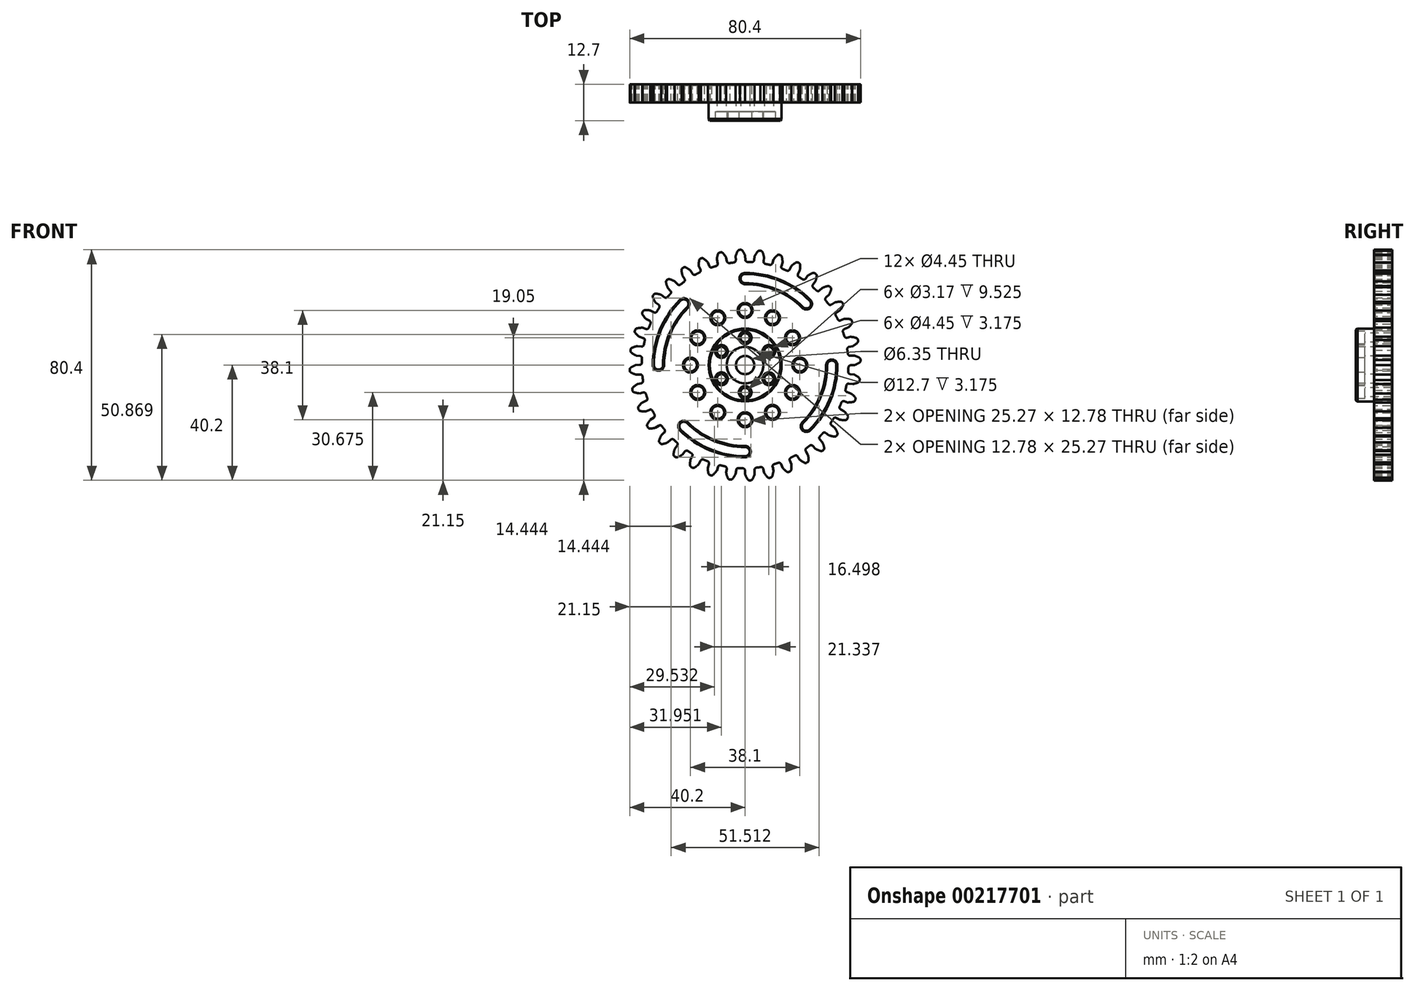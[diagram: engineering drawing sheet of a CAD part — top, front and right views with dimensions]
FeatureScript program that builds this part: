
annotation { "Feature Type Name" : "Feature", "Feature Type Description" : "" }
export const myFeature = defineFeature(function(context is Context, id is Id, definition is map)
    precondition{}
    {
        {
            var Q0;
            Q0=qCreatedBy(makeId("Front.planeOp"),FACE);
            var sketch = newSketch(context, id + "F0", { "sketchPlane" : qUnion([Q0])});
            skArc(sketch, "E0", {"start": v(-3.96, 35.76) * mm, "mid": v(-4.7, 35.68) * mm, "end": v(-5.43, 35.57) * mm});
            skArc(sketch, "E1.trimOffspring", {"start": v(0, 38.1) * mm, "mid": v(-0.4, 39) * mm, "end": v(-0.88, 39.84) * mm});
            skLineSegment(sketch, "E2", {"start": v(0, 38.1) * mm, "end": v(0.06, 36.73) * mm});
            skLineSegment(sketch, "E3", {"start": v(-1.55, 40.2) * mm, "end": v(-1.76, 40.2) * mm});
            skLineSegment(sketch, "E4.MirrorCS", {"start": v(-1.96, 40.18) * mm, "end": v(-1.76, 40.2) * mm});
            skArc(sketch, "E5.MirrorCS", {"start": v(-3.32, 37.96) * mm, "mid": v(-3, 38.88) * mm, "end": v(-2.6, 39.77) * mm});
            skLineSegment(sketch, "E6.MirrorCS", {"start": v(-3.32, 37.96) * mm, "end": v(-3.26, 36.58) * mm});
            skPoint(sketch, "E7.visualSharp", {"position": v(0.1, 35.98) * mm});
            skArc(sketch, "E7.filletArc", {"start": v(0.06, 36.73) * mm, "mid": v(0.3, 36.2) * mm, "end": v(0.83, 35.97) * mm});
            skPoint(sketch, "E8.visualSharp", {"position": v(-1.13, 40.2) * mm});
            skArc(sketch, "E8.filletArc", {"start": v(-0.88, 39.84) * mm, "mid": v(-1.17, 40.1) * mm, "end": v(-1.55, 40.2) * mm});
            skPoint(sketch, "E9.visualSharp", {"position": v(-2.38, 40.15) * mm});
            skArc(sketch, "E9.filletArc", {"start": v(-1.96, 40.18) * mm, "mid": v(-2.33, 40.05) * mm, "end": v(-2.6, 39.77) * mm});
            skPoint(sketch, "E10.visualSharp", {"position": v(-3.23, 35.84) * mm});
            skArc(sketch, "E10.filletArc", {"start": v(-3.96, 35.76) * mm, "mid": v(-3.45, 36.03) * mm, "end": v(-3.26, 36.58) * mm});
            skArc(sketch, "E11.1.0", {"start": v(-10.11, 34.53) * mm, "mid": v(-9.65, 34.89) * mm, "end": v(-9.56, 35.46) * mm});
            skLineSegment(sketch, "E11.1.1", {"start": v(-9.86, 36.8) * mm, "end": v(-9.56, 35.46) * mm});
            skArc(sketch, "E11.1.2", {"start": v(-9.86, 36.8) * mm, "mid": v(-9.7, 37.77) * mm, "end": v(-9.46, 38.71) * mm});
            skArc(sketch, "E11.1.3", {"start": v(-8.91, 39.23) * mm, "mid": v(-9.25, 39.04) * mm, "end": v(-9.46, 38.71) * mm});
            skLineSegment(sketch, "E11.1.4", {"start": v(-8.91, 39.23) * mm, "end": v(-8.7, 39.29) * mm});
            skLineSegment(sketch, "E11.1.5", {"start": v(-8.5, 39.32) * mm, "end": v(-8.7, 39.29) * mm});
            skArc(sketch, "E11.1.6", {"start": v(-7.79, 39.08) * mm, "mid": v(-8.11, 39.3) * mm, "end": v(-8.5, 39.32) * mm});
            skArc(sketch, "E11.1.7", {"start": v(-6.62, 37.52) * mm, "mid": v(-7.16, 38.33) * mm, "end": v(-7.79, 39.08) * mm});
            skLineSegment(sketch, "E11.1.8", {"start": v(-6.62, 37.52) * mm, "end": v(-6.32, 36.18) * mm});
            skArc(sketch, "E11.1.9", {"start": v(-6.32, 36.18) * mm, "mid": v(-6, 35.7) * mm, "end": v(-5.43, 35.57) * mm});
            skArc(sketch, "E11.2.0", {"start": v(-15.95, 32.25) * mm, "mid": v(-15.57, 32.68) * mm, "end": v(-15.58, 33.26) * mm});
            skLineSegment(sketch, "E11.2.1", {"start": v(-16.1, 34.53) * mm, "end": v(-15.58, 33.26) * mm});
            skArc(sketch, "E11.2.2", {"start": v(-16.1, 34.53) * mm, "mid": v(-16.12, 35.5) * mm, "end": v(-16.04, 36.48) * mm});
            skArc(sketch, "E11.2.3", {"start": v(-15.59, 37.09) * mm, "mid": v(-15.9, 36.84) * mm, "end": v(-16.04, 36.48) * mm});
            skLineSegment(sketch, "E11.2.4", {"start": v(-15.59, 37.09) * mm, "end": v(-15.4, 37.18) * mm});
            skLineSegment(sketch, "E11.2.5", {"start": v(-15.2, 37.25) * mm, "end": v(-15.4, 37.18) * mm});
            skArc(sketch, "E11.2.6", {"start": v(-14.46, 37.14) * mm, "mid": v(-14.81, 37.29) * mm, "end": v(-15.2, 37.25) * mm});
            skArc(sketch, "E11.2.7", {"start": v(-13.03, 35.8) * mm, "mid": v(-13.7, 36.5) * mm, "end": v(-14.46, 37.14) * mm});
            skLineSegment(sketch, "E11.2.8", {"start": v(-13.03, 35.8) * mm, "end": v(-12.5, 34.53) * mm});
            skArc(sketch, "E11.2.9", {"start": v(-12.5, 34.53) * mm, "mid": v(-12.1, 34.12) * mm, "end": v(-11.53, 34.09) * mm});
            skArc(sketch, "E12.2.3.0", {"start": v(-21.31, 29) * mm, "mid": v(-21, 29.48) * mm, "end": v(-21.11, 30.05) * mm});
            skLineSegment(sketch, "E12.4.3.0", {"start": v(-21.85, 31.2) * mm, "end": v(-21.11, 30.05) * mm});
            skArc(sketch, "E12.7.3.0", {"start": v(-21.85, 31.2) * mm, "mid": v(-22.04, 32.17) * mm, "end": v(-22.13, 33.14) * mm});
            skArc(sketch, "E12.11.3.0", {"start": v(-21.8, 33.82) * mm, "mid": v(-22.05, 33.52) * mm, "end": v(-22.13, 33.14) * mm});
            skLineSegment(sketch, "E12.15.3.0", {"start": v(-21.8, 33.82) * mm, "end": v(-21.62, 33.94) * mm});
            skLineSegment(sketch, "E12.18.3.0", {"start": v(-21.44, 34.04) * mm, "end": v(-21.62, 33.94) * mm});
            skArc(sketch, "E12.21.3.0", {"start": v(-20.68, 34.06) * mm, "mid": v(-21.06, 34.15) * mm, "end": v(-21.44, 34.04) * mm});
            skArc(sketch, "E12.25.3.0", {"start": v(-19.05, 33) * mm, "mid": v(-19.84, 33.57) * mm, "end": v(-20.68, 34.06) * mm});
            skLineSegment(sketch, "E12.29.3.0", {"start": v(-19.05, 33) * mm, "end": v(-18.31, 31.84) * mm});
            skArc(sketch, "E12.32.3.0", {"start": v(-18.31, 31.84) * mm, "mid": v(-17.84, 31.5) * mm, "end": v(-17.27, 31.57) * mm});
            skArc(sketch, "E12.2.4.0", {"start": v(-26.02, 24.85) * mm, "mid": v(-25.8, 25.39) * mm, "end": v(-26.01, 25.93) * mm});
            skLineSegment(sketch, "E12.4.4.0", {"start": v(-26.94, 26.94) * mm, "end": v(-26.01, 25.93) * mm});
            skArc(sketch, "E12.7.4.0", {"start": v(-26.94, 26.94) * mm, "mid": v(-27.3, 27.85) * mm, "end": v(-27.55, 28.8) * mm});
            skArc(sketch, "E12.11.4.0", {"start": v(-27.33, 29.52) * mm, "mid": v(-27.53, 29.18) * mm, "end": v(-27.55, 28.8) * mm});
            skLineSegment(sketch, "E12.15.4.0", {"start": v(-27.33, 29.52) * mm, "end": v(-27.19, 29.67) * mm});
            skLineSegment(sketch, "E12.18.4.0", {"start": v(-27.02, 29.8) * mm, "end": v(-27.19, 29.67) * mm});
            skArc(sketch, "E12.21.4.0", {"start": v(-26.29, 29.95) * mm, "mid": v(-26.67, 29.97) * mm, "end": v(-27.02, 29.8) * mm});
            skArc(sketch, "E12.25.4.0", {"start": v(-24.5, 29.19) * mm, "mid": v(-25.37, 29.61) * mm, "end": v(-26.29, 29.95) * mm});
            skLineSegment(sketch, "E12.29.4.0", {"start": v(-24.5, 29.19) * mm, "end": v(-23.56, 28.17) * mm});
            skArc(sketch, "E12.32.4.0", {"start": v(-23.56, 28.17) * mm, "mid": v(-23.04, 27.92) * mm, "end": v(-22.49, 28.1) * mm});
            skArc(sketch, "E12.2.5.0", {"start": v(-29.94, 19.96) * mm, "mid": v(-29.82, 20.52) * mm, "end": v(-30.12, 21.02) * mm});
            skLineSegment(sketch, "E12.4.5.0", {"start": v(-31.2, 21.85) * mm, "end": v(-30.12, 21.02) * mm});
            skArc(sketch, "E12.7.5.0", {"start": v(-31.2, 21.85) * mm, "mid": v(-31.71, 22.7) * mm, "end": v(-32.13, 23.57) * mm});
            skArc(sketch, "E12.11.5.0", {"start": v(-32.04, 24.32) * mm, "mid": v(-32.18, 23.96) * mm, "end": v(-32.13, 23.57) * mm});
            skLineSegment(sketch, "E12.15.5.0", {"start": v(-32.04, 24.32) * mm, "end": v(-31.92, 24.5) * mm});
            skLineSegment(sketch, "E12.18.5.0", {"start": v(-31.79, 24.66) * mm, "end": v(-31.92, 24.5) * mm});
            skArc(sketch, "E12.21.5.0", {"start": v(-31.09, 24.93) * mm, "mid": v(-31.47, 24.88) * mm, "end": v(-31.79, 24.66) * mm});
            skArc(sketch, "E12.25.5.0", {"start": v(-29.19, 24.5) * mm, "mid": v(-30.13, 24.76) * mm, "end": v(-31.09, 24.93) * mm});
            skLineSegment(sketch, "E12.29.5.0", {"start": v(-29.19, 24.5) * mm, "end": v(-28.1, 23.65) * mm});
            skArc(sketch, "E12.32.5.0", {"start": v(-28.1, 23.65) * mm, "mid": v(-27.54, 23.5) * mm, "end": v(-27.02, 23.76) * mm});
            skArc(sketch, "E12.2.6.0", {"start": v(-32.95, 14.45) * mm, "mid": v(-32.93, 15.03) * mm, "end": v(-33.31, 15.47) * mm});
            skLineSegment(sketch, "E12.4.6.0", {"start": v(-34.53, 16.1) * mm, "end": v(-33.31, 15.47) * mm});
            skArc(sketch, "E12.7.6.0", {"start": v(-34.53, 16.1) * mm, "mid": v(-35.17, 16.84) * mm, "end": v(-35.73, 17.64) * mm});
            skArc(sketch, "E12.11.6.0", {"start": v(-35.78, 18.4) * mm, "mid": v(-35.85, 18) * mm, "end": v(-35.73, 17.64) * mm});
            skLineSegment(sketch, "E12.15.6.0", {"start": v(-35.78, 18.4) * mm, "end": v(-35.7, 18.58) * mm});
            skLineSegment(sketch, "E12.18.6.0", {"start": v(-35.59, 18.76) * mm, "end": v(-35.7, 18.58) * mm});
            skArc(sketch, "E12.21.6.0", {"start": v(-34.94, 19.16) * mm, "mid": v(-35.32, 19.04) * mm, "end": v(-35.59, 18.76) * mm});
            skArc(sketch, "E12.25.6.0", {"start": v(-33, 19.05) * mm, "mid": v(-33.97, 19.15) * mm, "end": v(-34.94, 19.16) * mm});
            skLineSegment(sketch, "E12.29.6.0", {"start": v(-33, 19.05) * mm, "end": v(-31.78, 18.42) * mm});
            skArc(sketch, "E12.32.6.0", {"start": v(-31.78, 18.42) * mm, "mid": v(-31.2, 18.36) * mm, "end": v(-30.74, 18.7) * mm});
            skArc(sketch, "E12.2.7.0", {"start": v(-34.96, 8.51) * mm, "mid": v(-35.04, 9.08) * mm, "end": v(-35.5, 9.45) * mm});
            skLineSegment(sketch, "E12.4.7.0", {"start": v(-36.8, 9.86) * mm, "end": v(-35.5, 9.45) * mm});
            skArc(sketch, "E12.7.7.0", {"start": v(-36.8, 9.86) * mm, "mid": v(-37.56, 10.48) * mm, "end": v(-38.25, 11.16) * mm});
            skArc(sketch, "E12.11.7.0", {"start": v(-38.43, 11.9) * mm, "mid": v(-38.44, 11.5) * mm, "end": v(-38.25, 11.16) * mm});
            skLineSegment(sketch, "E12.15.7.0", {"start": v(-38.43, 11.9) * mm, "end": v(-38.38, 12.1) * mm});
            skLineSegment(sketch, "E12.18.7.0", {"start": v(-38.3, 12.3) * mm, "end": v(-38.38, 12.1) * mm});
            skArc(sketch, "E12.21.7.0", {"start": v(-37.74, 12.8) * mm, "mid": v(-38.09, 12.62) * mm, "end": v(-38.3, 12.3) * mm});
            skArc(sketch, "E12.25.7.0", {"start": v(-35.8, 13.03) * mm, "mid": v(-36.78, 12.96) * mm, "end": v(-37.74, 12.8) * mm});
            skLineSegment(sketch, "E12.29.7.0", {"start": v(-35.8, 13.03) * mm, "end": v(-34.5, 12.62) * mm});
            skArc(sketch, "E12.32.7.0", {"start": v(-34.5, 12.62) * mm, "mid": v(-33.91, 12.66) * mm, "end": v(-33.52, 13.08) * mm});
            skArc(sketch, "E12.2.8.0", {"start": v(-35.9, 2.3) * mm, "mid": v(-36.09, 2.86) * mm, "end": v(-36.6, 3.14) * mm});
            skLineSegment(sketch, "E12.4.8.0", {"start": v(-37.96, 3.32) * mm, "end": v(-36.6, 3.14) * mm});
            skArc(sketch, "E12.7.8.0", {"start": v(-37.96, 3.32) * mm, "mid": v(-38.8, 3.8) * mm, "end": v(-39.61, 4.35) * mm});
            skArc(sketch, "E12.11.8.0", {"start": v(-39.91, 5.04) * mm, "mid": v(-39.85, 4.66) * mm, "end": v(-39.61, 4.35) * mm});
            skLineSegment(sketch, "E12.15.8.0", {"start": v(-39.91, 5.04) * mm, "end": v(-39.9, 5.25) * mm});
            skLineSegment(sketch, "E12.18.8.0", {"start": v(-39.86, 5.46) * mm, "end": v(-39.9, 5.25) * mm});
            skArc(sketch, "E12.21.8.0", {"start": v(-39.39, 6.05) * mm, "mid": v(-39.7, 5.81) * mm, "end": v(-39.86, 5.46) * mm});
            skArc(sketch, "E12.25.8.0", {"start": v(-37.52, 6.62) * mm, "mid": v(-38.47, 6.38) * mm, "end": v(-39.39, 6.05) * mm});
            skLineSegment(sketch, "E12.29.8.0", {"start": v(-37.52, 6.62) * mm, "end": v(-36.16, 6.44) * mm});
            skArc(sketch, "E12.32.8.0", {"start": v(-36.16, 6.44) * mm, "mid": v(-35.6, 6.58) * mm, "end": v(-35.28, 7.06) * mm});
            skArc(sketch, "E12.2.9.0", {"start": v(-35.76, -3.96) * mm, "mid": v(-36.03, -3.45) * mm, "end": v(-36.58, -3.26) * mm});
            skLineSegment(sketch, "E12.4.9.0", {"start": v(-37.96, -3.32) * mm, "end": v(-36.58, -3.26) * mm});
            skArc(sketch, "E12.7.9.0", {"start": v(-37.96, -3.32) * mm, "mid": v(-38.88, -3) * mm, "end": v(-39.77, -2.6) * mm});
            skArc(sketch, "E12.11.9.0", {"start": v(-40.18, -1.96) * mm, "mid": v(-40.05, -2.33) * mm, "end": v(-39.77, -2.6) * mm});
            skLineSegment(sketch, "E12.15.9.0", {"start": v(-40.18, -1.96) * mm, "end": v(-40.2, -1.76) * mm});
            skLineSegment(sketch, "E12.18.9.0", {"start": v(-40.2, -1.55) * mm, "end": v(-40.2, -1.76) * mm});
            skArc(sketch, "E12.21.9.0", {"start": v(-39.84, -0.88) * mm, "mid": v(-40.1, -1.17) * mm, "end": v(-40.2, -1.55) * mm});
            skArc(sketch, "E12.25.9.0", {"start": v(-38.1, 0) * mm, "mid": v(-39, -0.4) * mm, "end": v(-39.84, -0.88) * mm});
            skLineSegment(sketch, "E12.29.9.0", {"start": v(-38.1, 0) * mm, "end": v(-36.73, 0.06) * mm});
            skArc(sketch, "E12.32.9.0", {"start": v(-36.73, 0.06) * mm, "mid": v(-36.2, 0.3) * mm, "end": v(-35.97, 0.83) * mm});
            skArc(sketch, "E12.2.10.0", {"start": v(-34.53, -10.11) * mm, "mid": v(-34.89, -9.65) * mm, "end": v(-35.46, -9.56) * mm});
            skLineSegment(sketch, "E12.4.10.0", {"start": v(-36.8, -9.86) * mm, "end": v(-35.46, -9.56) * mm});
            skArc(sketch, "E12.7.10.0", {"start": v(-36.8, -9.86) * mm, "mid": v(-37.77, -9.7) * mm, "end": v(-38.71, -9.46) * mm});
            skArc(sketch, "E12.11.10.0", {"start": v(-39.23, -8.91) * mm, "mid": v(-39.04, -9.25) * mm, "end": v(-38.71, -9.46) * mm});
            skLineSegment(sketch, "E12.15.10.0", {"start": v(-39.23, -8.91) * mm, "end": v(-39.29, -8.7) * mm});
            skLineSegment(sketch, "E12.18.10.0", {"start": v(-39.32, -8.5) * mm, "end": v(-39.29, -8.7) * mm});
            skArc(sketch, "E12.21.10.0", {"start": v(-39.08, -7.79) * mm, "mid": v(-39.3, -8.11) * mm, "end": v(-39.32, -8.5) * mm});
            skArc(sketch, "E12.25.10.0", {"start": v(-37.52, -6.62) * mm, "mid": v(-38.33, -7.16) * mm, "end": v(-39.08, -7.79) * mm});
            skLineSegment(sketch, "E12.29.10.0", {"start": v(-37.52, -6.62) * mm, "end": v(-36.18, -6.32) * mm});
            skArc(sketch, "E12.32.10.0", {"start": v(-36.18, -6.32) * mm, "mid": v(-35.7, -6) * mm, "end": v(-35.57, -5.43) * mm});
            skArc(sketch, "E12.2.11.0", {"start": v(-32.25, -15.95) * mm, "mid": v(-32.68, -15.57) * mm, "end": v(-33.26, -15.58) * mm});
            skLineSegment(sketch, "E12.4.11.0", {"start": v(-34.53, -16.1) * mm, "end": v(-33.26, -15.58) * mm});
            skArc(sketch, "E12.7.11.0", {"start": v(-34.53, -16.1) * mm, "mid": v(-35.5, -16.12) * mm, "end": v(-36.48, -16.04) * mm});
            skArc(sketch, "E12.11.11.0", {"start": v(-37.09, -15.59) * mm, "mid": v(-36.84, -15.9) * mm, "end": v(-36.48, -16.04) * mm});
            skLineSegment(sketch, "E12.15.11.0", {"start": v(-37.09, -15.59) * mm, "end": v(-37.18, -15.4) * mm});
            skLineSegment(sketch, "E12.18.11.0", {"start": v(-37.25, -15.2) * mm, "end": v(-37.18, -15.4) * mm});
            skArc(sketch, "E12.21.11.0", {"start": v(-37.14, -14.46) * mm, "mid": v(-37.29, -14.81) * mm, "end": v(-37.25, -15.2) * mm});
            skArc(sketch, "E12.25.11.0", {"start": v(-35.8, -13.03) * mm, "mid": v(-36.5, -13.7) * mm, "end": v(-37.14, -14.46) * mm});
            skLineSegment(sketch, "E12.29.11.0", {"start": v(-35.8, -13.03) * mm, "end": v(-34.53, -12.5) * mm});
            skArc(sketch, "E12.32.11.0", {"start": v(-34.53, -12.5) * mm, "mid": v(-34.12, -12.1) * mm, "end": v(-34.09, -11.53) * mm});
            skArc(sketch, "E12.2.12.0", {"start": v(-29, -21.31) * mm, "mid": v(-29.48, -21) * mm, "end": v(-30.05, -21.11) * mm});
            skLineSegment(sketch, "E12.4.12.0", {"start": v(-31.2, -21.85) * mm, "end": v(-30.05, -21.11) * mm});
            skArc(sketch, "E12.7.12.0", {"start": v(-31.2, -21.85) * mm, "mid": v(-32.17, -22.04) * mm, "end": v(-33.14, -22.13) * mm});
            skArc(sketch, "E12.11.12.0", {"start": v(-33.82, -21.8) * mm, "mid": v(-33.52, -22.05) * mm, "end": v(-33.14, -22.13) * mm});
            skLineSegment(sketch, "E12.15.12.0", {"start": v(-33.82, -21.8) * mm, "end": v(-33.94, -21.62) * mm});
            skLineSegment(sketch, "E12.18.12.0", {"start": v(-34.04, -21.44) * mm, "end": v(-33.94, -21.62) * mm});
            skArc(sketch, "E12.21.12.0", {"start": v(-34.06, -20.68) * mm, "mid": v(-34.15, -21.06) * mm, "end": v(-34.04, -21.44) * mm});
            skArc(sketch, "E12.25.12.0", {"start": v(-33, -19.05) * mm, "mid": v(-33.57, -19.84) * mm, "end": v(-34.06, -20.68) * mm});
            skLineSegment(sketch, "E12.29.12.0", {"start": v(-33, -19.05) * mm, "end": v(-31.84, -18.31) * mm});
            skArc(sketch, "E12.32.12.0", {"start": v(-31.84, -18.31) * mm, "mid": v(-31.5, -17.84) * mm, "end": v(-31.57, -17.27) * mm});
            skArc(sketch, "E12.2.13.0", {"start": v(-24.85, -26.02) * mm, "mid": v(-25.39, -25.8) * mm, "end": v(-25.93, -26.01) * mm});
            skLineSegment(sketch, "E12.4.13.0", {"start": v(-26.94, -26.94) * mm, "end": v(-25.93, -26.01) * mm});
            skArc(sketch, "E12.7.13.0", {"start": v(-26.94, -26.94) * mm, "mid": v(-27.85, -27.3) * mm, "end": v(-28.8, -27.55) * mm});
            skArc(sketch, "E12.11.13.0", {"start": v(-29.52, -27.33) * mm, "mid": v(-29.18, -27.53) * mm, "end": v(-28.8, -27.55) * mm});
            skLineSegment(sketch, "E12.15.13.0", {"start": v(-29.52, -27.33) * mm, "end": v(-29.67, -27.19) * mm});
            skLineSegment(sketch, "E12.18.13.0", {"start": v(-29.8, -27.02) * mm, "end": v(-29.67, -27.19) * mm});
            skArc(sketch, "E12.21.13.0", {"start": v(-29.95, -26.29) * mm, "mid": v(-29.97, -26.67) * mm, "end": v(-29.8, -27.02) * mm});
            skArc(sketch, "E12.25.13.0", {"start": v(-29.19, -24.5) * mm, "mid": v(-29.61, -25.37) * mm, "end": v(-29.95, -26.29) * mm});
            skLineSegment(sketch, "E12.29.13.0", {"start": v(-29.19, -24.5) * mm, "end": v(-28.17, -23.56) * mm});
            skArc(sketch, "E12.32.13.0", {"start": v(-28.17, -23.56) * mm, "mid": v(-27.92, -23.04) * mm, "end": v(-28.1, -22.49) * mm});
            skArc(sketch, "E12.2.14.0", {"start": v(-19.96, -29.94) * mm, "mid": v(-20.52, -29.82) * mm, "end": v(-21.02, -30.12) * mm});
            skLineSegment(sketch, "E12.4.14.0", {"start": v(-21.85, -31.2) * mm, "end": v(-21.02, -30.12) * mm});
            skArc(sketch, "E12.7.14.0", {"start": v(-21.85, -31.2) * mm, "mid": v(-22.7, -31.71) * mm, "end": v(-23.57, -32.13) * mm});
            skArc(sketch, "E12.11.14.0", {"start": v(-24.32, -32.04) * mm, "mid": v(-23.96, -32.18) * mm, "end": v(-23.57, -32.13) * mm});
            skLineSegment(sketch, "E12.15.14.0", {"start": v(-24.32, -32.04) * mm, "end": v(-24.5, -31.92) * mm});
            skLineSegment(sketch, "E12.18.14.0", {"start": v(-24.66, -31.79) * mm, "end": v(-24.5, -31.92) * mm});
            skArc(sketch, "E12.21.14.0", {"start": v(-24.93, -31.09) * mm, "mid": v(-24.88, -31.47) * mm, "end": v(-24.66, -31.79) * mm});
            skArc(sketch, "E12.25.14.0", {"start": v(-24.5, -29.19) * mm, "mid": v(-24.76, -30.13) * mm, "end": v(-24.93, -31.09) * mm});
            skLineSegment(sketch, "E12.29.14.0", {"start": v(-24.5, -29.19) * mm, "end": v(-23.65, -28.1) * mm});
            skArc(sketch, "E12.32.14.0", {"start": v(-23.65, -28.1) * mm, "mid": v(-23.5, -27.54) * mm, "end": v(-23.76, -27.02) * mm});
            skArc(sketch, "E12.2.15.0", {"start": v(-14.45, -32.95) * mm, "mid": v(-15.03, -32.93) * mm, "end": v(-15.47, -33.31) * mm});
            skLineSegment(sketch, "E12.4.15.0", {"start": v(-16.1, -34.53) * mm, "end": v(-15.47, -33.31) * mm});
            skArc(sketch, "E12.7.15.0", {"start": v(-16.1, -34.53) * mm, "mid": v(-16.84, -35.17) * mm, "end": v(-17.64, -35.73) * mm});
            skArc(sketch, "E12.11.15.0", {"start": v(-18.4, -35.78) * mm, "mid": v(-18, -35.85) * mm, "end": v(-17.64, -35.73) * mm});
            skLineSegment(sketch, "E12.15.15.0", {"start": v(-18.4, -35.78) * mm, "end": v(-18.58, -35.7) * mm});
            skLineSegment(sketch, "E12.18.15.0", {"start": v(-18.76, -35.59) * mm, "end": v(-18.58, -35.7) * mm});
            skArc(sketch, "E12.21.15.0", {"start": v(-19.16, -34.94) * mm, "mid": v(-19.04, -35.32) * mm, "end": v(-18.76, -35.59) * mm});
            skArc(sketch, "E12.25.15.0", {"start": v(-19.05, -33) * mm, "mid": v(-19.15, -33.97) * mm, "end": v(-19.16, -34.94) * mm});
            skLineSegment(sketch, "E12.29.15.0", {"start": v(-19.05, -33) * mm, "end": v(-18.42, -31.78) * mm});
            skArc(sketch, "E12.32.15.0", {"start": v(-18.42, -31.78) * mm, "mid": v(-18.36, -31.2) * mm, "end": v(-18.7, -30.74) * mm});
            skArc(sketch, "E12.2.16.0", {"start": v(-8.51, -34.96) * mm, "mid": v(-9.08, -35.04) * mm, "end": v(-9.45, -35.5) * mm});
            skLineSegment(sketch, "E12.4.16.0", {"start": v(-9.86, -36.8) * mm, "end": v(-9.45, -35.5) * mm});
            skArc(sketch, "E12.7.16.0", {"start": v(-9.86, -36.8) * mm, "mid": v(-10.48, -37.56) * mm, "end": v(-11.16, -38.25) * mm});
            skArc(sketch, "E12.11.16.0", {"start": v(-11.9, -38.43) * mm, "mid": v(-11.5, -38.44) * mm, "end": v(-11.16, -38.25) * mm});
            skLineSegment(sketch, "E12.15.16.0", {"start": v(-11.9, -38.43) * mm, "end": v(-12.1, -38.38) * mm});
            skLineSegment(sketch, "E12.18.16.0", {"start": v(-12.3, -38.3) * mm, "end": v(-12.1, -38.38) * mm});
            skArc(sketch, "E12.21.16.0", {"start": v(-12.8, -37.74) * mm, "mid": v(-12.62, -38.09) * mm, "end": v(-12.3, -38.3) * mm});
            skArc(sketch, "E12.25.16.0", {"start": v(-13.03, -35.8) * mm, "mid": v(-12.96, -36.78) * mm, "end": v(-12.8, -37.74) * mm});
            skLineSegment(sketch, "E12.29.16.0", {"start": v(-13.03, -35.8) * mm, "end": v(-12.62, -34.5) * mm});
            skArc(sketch, "E12.32.16.0", {"start": v(-12.62, -34.5) * mm, "mid": v(-12.66, -33.91) * mm, "end": v(-13.08, -33.52) * mm});
            skArc(sketch, "E12.2.17.0", {"start": v(-2.3, -35.9) * mm, "mid": v(-2.86, -36.09) * mm, "end": v(-3.14, -36.6) * mm});
            skLineSegment(sketch, "E12.4.17.0", {"start": v(-3.32, -37.96) * mm, "end": v(-3.14, -36.6) * mm});
            skArc(sketch, "E12.7.17.0", {"start": v(-3.32, -37.96) * mm, "mid": v(-3.8, -38.8) * mm, "end": v(-4.35, -39.61) * mm});
            skArc(sketch, "E12.11.17.0", {"start": v(-5.04, -39.91) * mm, "mid": v(-4.66, -39.85) * mm, "end": v(-4.35, -39.61) * mm});
            skLineSegment(sketch, "E12.15.17.0", {"start": v(-5.04, -39.91) * mm, "end": v(-5.25, -39.9) * mm});
            skLineSegment(sketch, "E12.18.17.0", {"start": v(-5.46, -39.86) * mm, "end": v(-5.25, -39.9) * mm});
            skArc(sketch, "E12.21.17.0", {"start": v(-6.05, -39.39) * mm, "mid": v(-5.81, -39.7) * mm, "end": v(-5.46, -39.86) * mm});
            skArc(sketch, "E12.25.17.0", {"start": v(-6.62, -37.52) * mm, "mid": v(-6.38, -38.47) * mm, "end": v(-6.05, -39.39) * mm});
            skLineSegment(sketch, "E12.29.17.0", {"start": v(-6.62, -37.52) * mm, "end": v(-6.44, -36.16) * mm});
            skArc(sketch, "E12.32.17.0", {"start": v(-6.44, -36.16) * mm, "mid": v(-6.58, -35.6) * mm, "end": v(-7.06, -35.28) * mm});
            skArc(sketch, "E12.2.18.0", {"start": v(3.96, -35.76) * mm, "mid": v(3.45, -36.03) * mm, "end": v(3.26, -36.58) * mm});
            skLineSegment(sketch, "E12.4.18.0", {"start": v(3.32, -37.96) * mm, "end": v(3.26, -36.58) * mm});
            skArc(sketch, "E12.7.18.0", {"start": v(3.32, -37.96) * mm, "mid": v(3, -38.88) * mm, "end": v(2.6, -39.77) * mm});
            skArc(sketch, "E12.11.18.0", {"start": v(1.96, -40.18) * mm, "mid": v(2.33, -40.05) * mm, "end": v(2.6, -39.77) * mm});
            skLineSegment(sketch, "E12.15.18.0", {"start": v(1.96, -40.18) * mm, "end": v(1.76, -40.2) * mm});
            skLineSegment(sketch, "E12.18.18.0", {"start": v(1.55, -40.2) * mm, "end": v(1.76, -40.2) * mm});
            skArc(sketch, "E12.21.18.0", {"start": v(0.88, -39.84) * mm, "mid": v(1.17, -40.1) * mm, "end": v(1.55, -40.2) * mm});
            skArc(sketch, "E12.25.18.0", {"start": v(0, -38.1) * mm, "mid": v(0.4, -39) * mm, "end": v(0.88, -39.84) * mm});
            skLineSegment(sketch, "E12.29.18.0", {"start": v(0, -38.1) * mm, "end": v(-0.06, -36.73) * mm});
            skArc(sketch, "E12.32.18.0", {"start": v(-0.06, -36.73) * mm, "mid": v(-0.3, -36.2) * mm, "end": v(-0.83, -35.97) * mm});
            skArc(sketch, "E12.2.19.0", {"start": v(10.11, -34.53) * mm, "mid": v(9.65, -34.89) * mm, "end": v(9.56, -35.46) * mm});
            skLineSegment(sketch, "E12.4.19.0", {"start": v(9.86, -36.8) * mm, "end": v(9.56, -35.46) * mm});
            skArc(sketch, "E12.7.19.0", {"start": v(9.86, -36.8) * mm, "mid": v(9.7, -37.77) * mm, "end": v(9.46, -38.71) * mm});
            skArc(sketch, "E12.11.19.0", {"start": v(8.91, -39.23) * mm, "mid": v(9.25, -39.04) * mm, "end": v(9.46, -38.71) * mm});
            skLineSegment(sketch, "E12.15.19.0", {"start": v(8.91, -39.23) * mm, "end": v(8.7, -39.29) * mm});
            skLineSegment(sketch, "E12.18.19.0", {"start": v(8.5, -39.32) * mm, "end": v(8.7, -39.29) * mm});
            skArc(sketch, "E12.21.19.0", {"start": v(7.79, -39.08) * mm, "mid": v(8.11, -39.3) * mm, "end": v(8.5, -39.32) * mm});
            skArc(sketch, "E12.25.19.0", {"start": v(6.62, -37.52) * mm, "mid": v(7.16, -38.33) * mm, "end": v(7.79, -39.08) * mm});
            skLineSegment(sketch, "E12.29.19.0", {"start": v(6.62, -37.52) * mm, "end": v(6.32, -36.18) * mm});
            skArc(sketch, "E12.32.19.0", {"start": v(6.32, -36.18) * mm, "mid": v(6, -35.7) * mm, "end": v(5.43, -35.57) * mm});
            skArc(sketch, "E12.2.20.0", {"start": v(15.95, -32.25) * mm, "mid": v(15.57, -32.68) * mm, "end": v(15.58, -33.26) * mm});
            skLineSegment(sketch, "E12.4.20.0", {"start": v(16.1, -34.53) * mm, "end": v(15.58, -33.26) * mm});
            skArc(sketch, "E12.7.20.0", {"start": v(16.1, -34.53) * mm, "mid": v(16.12, -35.5) * mm, "end": v(16.04, -36.48) * mm});
            skArc(sketch, "E12.11.20.0", {"start": v(15.59, -37.09) * mm, "mid": v(15.9, -36.84) * mm, "end": v(16.04, -36.48) * mm});
            skLineSegment(sketch, "E12.15.20.0", {"start": v(15.59, -37.09) * mm, "end": v(15.4, -37.18) * mm});
            skLineSegment(sketch, "E12.18.20.0", {"start": v(15.2, -37.25) * mm, "end": v(15.4, -37.18) * mm});
            skArc(sketch, "E12.21.20.0", {"start": v(14.46, -37.14) * mm, "mid": v(14.81, -37.29) * mm, "end": v(15.2, -37.25) * mm});
            skArc(sketch, "E12.25.20.0", {"start": v(13.03, -35.8) * mm, "mid": v(13.7, -36.5) * mm, "end": v(14.46, -37.14) * mm});
            skLineSegment(sketch, "E12.29.20.0", {"start": v(13.03, -35.8) * mm, "end": v(12.5, -34.53) * mm});
            skArc(sketch, "E12.32.20.0", {"start": v(12.5, -34.53) * mm, "mid": v(12.1, -34.12) * mm, "end": v(11.53, -34.09) * mm});
            skArc(sketch, "E12.2.21.0", {"start": v(21.31, -29) * mm, "mid": v(21, -29.48) * mm, "end": v(21.11, -30.05) * mm});
            skLineSegment(sketch, "E12.4.21.0", {"start": v(21.85, -31.2) * mm, "end": v(21.11, -30.05) * mm});
            skArc(sketch, "E12.7.21.0", {"start": v(21.85, -31.2) * mm, "mid": v(22.04, -32.17) * mm, "end": v(22.13, -33.14) * mm});
            skArc(sketch, "E12.11.21.0", {"start": v(21.8, -33.82) * mm, "mid": v(22.05, -33.52) * mm, "end": v(22.13, -33.14) * mm});
            skLineSegment(sketch, "E12.15.21.0", {"start": v(21.8, -33.82) * mm, "end": v(21.62, -33.94) * mm});
            skLineSegment(sketch, "E12.18.21.0", {"start": v(21.44, -34.04) * mm, "end": v(21.62, -33.94) * mm});
            skArc(sketch, "E12.21.21.0", {"start": v(20.68, -34.06) * mm, "mid": v(21.06, -34.15) * mm, "end": v(21.44, -34.04) * mm});
            skArc(sketch, "E12.25.21.0", {"start": v(19.05, -33) * mm, "mid": v(19.84, -33.57) * mm, "end": v(20.68, -34.06) * mm});
            skLineSegment(sketch, "E12.29.21.0", {"start": v(19.05, -33) * mm, "end": v(18.31, -31.84) * mm});
            skArc(sketch, "E12.32.21.0", {"start": v(18.31, -31.84) * mm, "mid": v(17.84, -31.5) * mm, "end": v(17.27, -31.57) * mm});
            skArc(sketch, "E12.2.22.0", {"start": v(26.02, -24.85) * mm, "mid": v(25.8, -25.39) * mm, "end": v(26.01, -25.93) * mm});
            skLineSegment(sketch, "E12.4.22.0", {"start": v(26.94, -26.94) * mm, "end": v(26.01, -25.93) * mm});
            skArc(sketch, "E12.7.22.0", {"start": v(26.94, -26.94) * mm, "mid": v(27.3, -27.85) * mm, "end": v(27.55, -28.8) * mm});
            skArc(sketch, "E12.11.22.0", {"start": v(27.33, -29.52) * mm, "mid": v(27.53, -29.18) * mm, "end": v(27.55, -28.8) * mm});
            skLineSegment(sketch, "E12.15.22.0", {"start": v(27.33, -29.52) * mm, "end": v(27.19, -29.67) * mm});
            skLineSegment(sketch, "E12.18.22.0", {"start": v(27.02, -29.8) * mm, "end": v(27.19, -29.67) * mm});
            skArc(sketch, "E12.21.22.0", {"start": v(26.29, -29.95) * mm, "mid": v(26.67, -29.97) * mm, "end": v(27.02, -29.8) * mm});
            skArc(sketch, "E12.25.22.0", {"start": v(24.5, -29.19) * mm, "mid": v(25.37, -29.61) * mm, "end": v(26.29, -29.95) * mm});
            skLineSegment(sketch, "E12.29.22.0", {"start": v(24.5, -29.19) * mm, "end": v(23.56, -28.17) * mm});
            skArc(sketch, "E12.32.22.0", {"start": v(23.56, -28.17) * mm, "mid": v(23.04, -27.92) * mm, "end": v(22.49, -28.1) * mm});
            skArc(sketch, "E12.2.23.0", {"start": v(29.94, -19.96) * mm, "mid": v(29.82, -20.52) * mm, "end": v(30.12, -21.02) * mm});
            skLineSegment(sketch, "E12.4.23.0", {"start": v(31.2, -21.85) * mm, "end": v(30.12, -21.02) * mm});
            skArc(sketch, "E12.7.23.0", {"start": v(31.2, -21.85) * mm, "mid": v(31.71, -22.7) * mm, "end": v(32.13, -23.57) * mm});
            skArc(sketch, "E12.11.23.0", {"start": v(32.04, -24.32) * mm, "mid": v(32.18, -23.96) * mm, "end": v(32.13, -23.57) * mm});
            skLineSegment(sketch, "E12.15.23.0", {"start": v(32.04, -24.32) * mm, "end": v(31.92, -24.5) * mm});
            skLineSegment(sketch, "E12.18.23.0", {"start": v(31.79, -24.66) * mm, "end": v(31.92, -24.5) * mm});
            skArc(sketch, "E12.21.23.0", {"start": v(31.09, -24.93) * mm, "mid": v(31.47, -24.88) * mm, "end": v(31.79, -24.66) * mm});
            skArc(sketch, "E12.25.23.0", {"start": v(29.19, -24.5) * mm, "mid": v(30.13, -24.76) * mm, "end": v(31.09, -24.93) * mm});
            skLineSegment(sketch, "E12.29.23.0", {"start": v(29.19, -24.5) * mm, "end": v(28.1, -23.65) * mm});
            skArc(sketch, "E12.32.23.0", {"start": v(28.1, -23.65) * mm, "mid": v(27.54, -23.5) * mm, "end": v(27.02, -23.76) * mm});
            skArc(sketch, "E12.2.24.0", {"start": v(32.95, -14.45) * mm, "mid": v(32.93, -15.03) * mm, "end": v(33.31, -15.47) * mm});
            skLineSegment(sketch, "E12.4.24.0", {"start": v(34.53, -16.1) * mm, "end": v(33.31, -15.47) * mm});
            skArc(sketch, "E12.7.24.0", {"start": v(34.53, -16.1) * mm, "mid": v(35.17, -16.84) * mm, "end": v(35.73, -17.64) * mm});
            skArc(sketch, "E12.11.24.0", {"start": v(35.78, -18.4) * mm, "mid": v(35.85, -18) * mm, "end": v(35.73, -17.64) * mm});
            skLineSegment(sketch, "E12.15.24.0", {"start": v(35.78, -18.4) * mm, "end": v(35.7, -18.58) * mm});
            skLineSegment(sketch, "E12.18.24.0", {"start": v(35.59, -18.76) * mm, "end": v(35.7, -18.58) * mm});
            skArc(sketch, "E12.21.24.0", {"start": v(34.94, -19.16) * mm, "mid": v(35.32, -19.04) * mm, "end": v(35.59, -18.76) * mm});
            skArc(sketch, "E12.25.24.0", {"start": v(33, -19.05) * mm, "mid": v(33.97, -19.15) * mm, "end": v(34.94, -19.16) * mm});
            skLineSegment(sketch, "E12.29.24.0", {"start": v(33, -19.05) * mm, "end": v(31.78, -18.42) * mm});
            skArc(sketch, "E12.32.24.0", {"start": v(31.78, -18.42) * mm, "mid": v(31.2, -18.36) * mm, "end": v(30.74, -18.7) * mm});
            skArc(sketch, "E12.2.25.0", {"start": v(34.96, -8.51) * mm, "mid": v(35.04, -9.08) * mm, "end": v(35.5, -9.45) * mm});
            skLineSegment(sketch, "E12.4.25.0", {"start": v(36.8, -9.86) * mm, "end": v(35.5, -9.45) * mm});
            skArc(sketch, "E12.7.25.0", {"start": v(36.8, -9.86) * mm, "mid": v(37.56, -10.48) * mm, "end": v(38.25, -11.16) * mm});
            skArc(sketch, "E12.11.25.0", {"start": v(38.43, -11.9) * mm, "mid": v(38.44, -11.5) * mm, "end": v(38.25, -11.16) * mm});
            skLineSegment(sketch, "E12.15.25.0", {"start": v(38.43, -11.9) * mm, "end": v(38.38, -12.1) * mm});
            skLineSegment(sketch, "E12.18.25.0", {"start": v(38.3, -12.3) * mm, "end": v(38.38, -12.1) * mm});
            skArc(sketch, "E12.21.25.0", {"start": v(37.74, -12.8) * mm, "mid": v(38.09, -12.62) * mm, "end": v(38.3, -12.3) * mm});
            skArc(sketch, "E12.25.25.0", {"start": v(35.8, -13.03) * mm, "mid": v(36.78, -12.96) * mm, "end": v(37.74, -12.8) * mm});
            skLineSegment(sketch, "E12.29.25.0", {"start": v(35.8, -13.03) * mm, "end": v(34.5, -12.62) * mm});
            skArc(sketch, "E12.32.25.0", {"start": v(34.5, -12.62) * mm, "mid": v(33.91, -12.66) * mm, "end": v(33.52, -13.08) * mm});
            skArc(sketch, "E12.2.26.0", {"start": v(35.9, -2.3) * mm, "mid": v(36.09, -2.86) * mm, "end": v(36.6, -3.14) * mm});
            skLineSegment(sketch, "E12.4.26.0", {"start": v(37.96, -3.32) * mm, "end": v(36.6, -3.14) * mm});
            skArc(sketch, "E12.7.26.0", {"start": v(37.96, -3.32) * mm, "mid": v(38.8, -3.8) * mm, "end": v(39.61, -4.35) * mm});
            skArc(sketch, "E12.11.26.0", {"start": v(39.91, -5.04) * mm, "mid": v(39.85, -4.66) * mm, "end": v(39.61, -4.35) * mm});
            skLineSegment(sketch, "E12.15.26.0", {"start": v(39.91, -5.04) * mm, "end": v(39.9, -5.25) * mm});
            skLineSegment(sketch, "E12.18.26.0", {"start": v(39.86, -5.46) * mm, "end": v(39.9, -5.25) * mm});
            skArc(sketch, "E12.21.26.0", {"start": v(39.39, -6.05) * mm, "mid": v(39.7, -5.81) * mm, "end": v(39.86, -5.46) * mm});
            skArc(sketch, "E12.25.26.0", {"start": v(37.52, -6.62) * mm, "mid": v(38.47, -6.38) * mm, "end": v(39.39, -6.05) * mm});
            skLineSegment(sketch, "E12.29.26.0", {"start": v(37.52, -6.62) * mm, "end": v(36.16, -6.44) * mm});
            skArc(sketch, "E12.32.26.0", {"start": v(36.16, -6.44) * mm, "mid": v(35.6, -6.58) * mm, "end": v(35.28, -7.06) * mm});
            skArc(sketch, "E12.2.27.0", {"start": v(35.76, 3.96) * mm, "mid": v(36.03, 3.45) * mm, "end": v(36.58, 3.26) * mm});
            skLineSegment(sketch, "E12.4.27.0", {"start": v(37.96, 3.32) * mm, "end": v(36.58, 3.26) * mm});
            skArc(sketch, "E12.7.27.0", {"start": v(37.96, 3.32) * mm, "mid": v(38.88, 3) * mm, "end": v(39.77, 2.6) * mm});
            skArc(sketch, "E12.11.27.0", {"start": v(40.18, 1.96) * mm, "mid": v(40.05, 2.33) * mm, "end": v(39.77, 2.6) * mm});
            skLineSegment(sketch, "E12.15.27.0", {"start": v(40.18, 1.96) * mm, "end": v(40.2, 1.76) * mm});
            skLineSegment(sketch, "E12.18.27.0", {"start": v(40.2, 1.55) * mm, "end": v(40.2, 1.76) * mm});
            skArc(sketch, "E12.21.27.0", {"start": v(39.84, 0.88) * mm, "mid": v(40.1, 1.17) * mm, "end": v(40.2, 1.55) * mm});
            skArc(sketch, "E12.25.27.0", {"start": v(38.1, 0) * mm, "mid": v(39, 0.4) * mm, "end": v(39.84, 0.88) * mm});
            skLineSegment(sketch, "E12.29.27.0", {"start": v(38.1, 0) * mm, "end": v(36.73, -0.06) * mm});
            skArc(sketch, "E12.32.27.0", {"start": v(36.73, -0.06) * mm, "mid": v(36.2, -0.3) * mm, "end": v(35.97, -0.83) * mm});
            skArc(sketch, "E12.2.28.0", {"start": v(34.53, 10.11) * mm, "mid": v(34.89, 9.65) * mm, "end": v(35.46, 9.56) * mm});
            skLineSegment(sketch, "E12.4.28.0", {"start": v(36.8, 9.86) * mm, "end": v(35.46, 9.56) * mm});
            skArc(sketch, "E12.7.28.0", {"start": v(36.8, 9.86) * mm, "mid": v(37.77, 9.7) * mm, "end": v(38.71, 9.46) * mm});
            skArc(sketch, "E12.11.28.0", {"start": v(39.23, 8.91) * mm, "mid": v(39.04, 9.25) * mm, "end": v(38.71, 9.46) * mm});
            skLineSegment(sketch, "E12.15.28.0", {"start": v(39.23, 8.91) * mm, "end": v(39.29, 8.7) * mm});
            skLineSegment(sketch, "E12.18.28.0", {"start": v(39.32, 8.5) * mm, "end": v(39.29, 8.7) * mm});
            skArc(sketch, "E12.21.28.0", {"start": v(39.08, 7.79) * mm, "mid": v(39.3, 8.11) * mm, "end": v(39.32, 8.5) * mm});
            skArc(sketch, "E12.25.28.0", {"start": v(37.52, 6.62) * mm, "mid": v(38.33, 7.16) * mm, "end": v(39.08, 7.79) * mm});
            skLineSegment(sketch, "E12.29.28.0", {"start": v(37.52, 6.62) * mm, "end": v(36.18, 6.32) * mm});
            skArc(sketch, "E12.32.28.0", {"start": v(36.18, 6.32) * mm, "mid": v(35.7, 6) * mm, "end": v(35.57, 5.43) * mm});
            skArc(sketch, "E12.2.29.0", {"start": v(32.25, 15.95) * mm, "mid": v(32.68, 15.57) * mm, "end": v(33.26, 15.58) * mm});
            skLineSegment(sketch, "E12.4.29.0", {"start": v(34.53, 16.1) * mm, "end": v(33.26, 15.58) * mm});
            skArc(sketch, "E12.7.29.0", {"start": v(34.53, 16.1) * mm, "mid": v(35.5, 16.12) * mm, "end": v(36.48, 16.04) * mm});
            skArc(sketch, "E12.11.29.0", {"start": v(37.09, 15.59) * mm, "mid": v(36.84, 15.9) * mm, "end": v(36.48, 16.04) * mm});
            skLineSegment(sketch, "E12.15.29.0", {"start": v(37.09, 15.59) * mm, "end": v(37.18, 15.4) * mm});
            skLineSegment(sketch, "E12.18.29.0", {"start": v(37.25, 15.2) * mm, "end": v(37.18, 15.4) * mm});
            skArc(sketch, "E12.21.29.0", {"start": v(37.14, 14.46) * mm, "mid": v(37.29, 14.81) * mm, "end": v(37.25, 15.2) * mm});
            skArc(sketch, "E12.25.29.0", {"start": v(35.8, 13.03) * mm, "mid": v(36.5, 13.7) * mm, "end": v(37.14, 14.46) * mm});
            skLineSegment(sketch, "E12.29.29.0", {"start": v(35.8, 13.03) * mm, "end": v(34.53, 12.5) * mm});
            skArc(sketch, "E12.32.29.0", {"start": v(34.53, 12.5) * mm, "mid": v(34.12, 12.1) * mm, "end": v(34.09, 11.53) * mm});
            skArc(sketch, "E12.2.30.0", {"start": v(29, 21.31) * mm, "mid": v(29.48, 21) * mm, "end": v(30.05, 21.11) * mm});
            skLineSegment(sketch, "E12.4.30.0", {"start": v(31.2, 21.85) * mm, "end": v(30.05, 21.11) * mm});
            skArc(sketch, "E12.7.30.0", {"start": v(31.2, 21.85) * mm, "mid": v(32.17, 22.04) * mm, "end": v(33.14, 22.13) * mm});
            skArc(sketch, "E12.11.30.0", {"start": v(33.82, 21.8) * mm, "mid": v(33.52, 22.05) * mm, "end": v(33.14, 22.13) * mm});
            skLineSegment(sketch, "E12.15.30.0", {"start": v(33.82, 21.8) * mm, "end": v(33.94, 21.62) * mm});
            skLineSegment(sketch, "E12.18.30.0", {"start": v(34.04, 21.44) * mm, "end": v(33.94, 21.62) * mm});
            skArc(sketch, "E12.21.30.0", {"start": v(34.06, 20.68) * mm, "mid": v(34.15, 21.06) * mm, "end": v(34.04, 21.44) * mm});
            skArc(sketch, "E12.25.30.0", {"start": v(33, 19.05) * mm, "mid": v(33.57, 19.84) * mm, "end": v(34.06, 20.68) * mm});
            skLineSegment(sketch, "E12.29.30.0", {"start": v(33, 19.05) * mm, "end": v(31.84, 18.31) * mm});
            skArc(sketch, "E12.32.30.0", {"start": v(31.84, 18.31) * mm, "mid": v(31.5, 17.84) * mm, "end": v(31.57, 17.27) * mm});
            skArc(sketch, "E12.2.31.0", {"start": v(24.85, 26.02) * mm, "mid": v(25.39, 25.8) * mm, "end": v(25.93, 26.01) * mm});
            skLineSegment(sketch, "E12.4.31.0", {"start": v(26.94, 26.94) * mm, "end": v(25.93, 26.01) * mm});
            skArc(sketch, "E12.7.31.0", {"start": v(26.94, 26.94) * mm, "mid": v(27.85, 27.3) * mm, "end": v(28.8, 27.55) * mm});
            skArc(sketch, "E12.11.31.0", {"start": v(29.52, 27.33) * mm, "mid": v(29.18, 27.53) * mm, "end": v(28.8, 27.55) * mm});
            skLineSegment(sketch, "E12.15.31.0", {"start": v(29.52, 27.33) * mm, "end": v(29.67, 27.19) * mm});
            skLineSegment(sketch, "E12.18.31.0", {"start": v(29.8, 27.02) * mm, "end": v(29.67, 27.19) * mm});
            skArc(sketch, "E12.21.31.0", {"start": v(29.95, 26.29) * mm, "mid": v(29.97, 26.67) * mm, "end": v(29.8, 27.02) * mm});
            skArc(sketch, "E12.25.31.0", {"start": v(29.19, 24.5) * mm, "mid": v(29.61, 25.37) * mm, "end": v(29.95, 26.29) * mm});
            skLineSegment(sketch, "E12.29.31.0", {"start": v(29.19, 24.5) * mm, "end": v(28.17, 23.56) * mm});
            skArc(sketch, "E12.32.31.0", {"start": v(28.17, 23.56) * mm, "mid": v(27.92, 23.04) * mm, "end": v(28.1, 22.49) * mm});
            skArc(sketch, "E12.2.32.0", {"start": v(19.96, 29.94) * mm, "mid": v(20.52, 29.82) * mm, "end": v(21.02, 30.12) * mm});
            skLineSegment(sketch, "E12.4.32.0", {"start": v(21.85, 31.2) * mm, "end": v(21.02, 30.12) * mm});
            skArc(sketch, "E12.7.32.0", {"start": v(21.85, 31.2) * mm, "mid": v(22.7, 31.71) * mm, "end": v(23.57, 32.13) * mm});
            skArc(sketch, "E12.11.32.0", {"start": v(24.32, 32.04) * mm, "mid": v(23.96, 32.18) * mm, "end": v(23.57, 32.13) * mm});
            skLineSegment(sketch, "E12.15.32.0", {"start": v(24.32, 32.04) * mm, "end": v(24.5, 31.92) * mm});
            skLineSegment(sketch, "E12.18.32.0", {"start": v(24.66, 31.79) * mm, "end": v(24.5, 31.92) * mm});
            skArc(sketch, "E12.21.32.0", {"start": v(24.93, 31.09) * mm, "mid": v(24.88, 31.47) * mm, "end": v(24.66, 31.79) * mm});
            skArc(sketch, "E12.25.32.0", {"start": v(24.5, 29.19) * mm, "mid": v(24.76, 30.13) * mm, "end": v(24.93, 31.09) * mm});
            skLineSegment(sketch, "E12.29.32.0", {"start": v(24.5, 29.19) * mm, "end": v(23.65, 28.1) * mm});
            skArc(sketch, "E12.32.32.0", {"start": v(23.65, 28.1) * mm, "mid": v(23.5, 27.54) * mm, "end": v(23.76, 27.02) * mm});
            skArc(sketch, "E12.2.33.0", {"start": v(14.45, 32.95) * mm, "mid": v(15.03, 32.93) * mm, "end": v(15.47, 33.31) * mm});
            skLineSegment(sketch, "E12.4.33.0", {"start": v(16.1, 34.53) * mm, "end": v(15.47, 33.31) * mm});
            skArc(sketch, "E12.7.33.0", {"start": v(16.1, 34.53) * mm, "mid": v(16.84, 35.17) * mm, "end": v(17.64, 35.73) * mm});
            skArc(sketch, "E12.11.33.0", {"start": v(18.4, 35.78) * mm, "mid": v(18, 35.85) * mm, "end": v(17.64, 35.73) * mm});
            skLineSegment(sketch, "E12.15.33.0", {"start": v(18.4, 35.78) * mm, "end": v(18.58, 35.7) * mm});
            skLineSegment(sketch, "E12.18.33.0", {"start": v(18.76, 35.59) * mm, "end": v(18.58, 35.7) * mm});
            skArc(sketch, "E12.21.33.0", {"start": v(19.16, 34.94) * mm, "mid": v(19.04, 35.32) * mm, "end": v(18.76, 35.59) * mm});
            skArc(sketch, "E12.25.33.0", {"start": v(19.05, 33) * mm, "mid": v(19.15, 33.97) * mm, "end": v(19.16, 34.94) * mm});
            skLineSegment(sketch, "E12.29.33.0", {"start": v(19.05, 33) * mm, "end": v(18.42, 31.78) * mm});
            skArc(sketch, "E12.32.33.0", {"start": v(18.42, 31.78) * mm, "mid": v(18.36, 31.2) * mm, "end": v(18.7, 30.74) * mm});
            skArc(sketch, "E12.2.34.0", {"start": v(8.51, 34.96) * mm, "mid": v(9.08, 35.04) * mm, "end": v(9.45, 35.5) * mm});
            skLineSegment(sketch, "E12.4.34.0", {"start": v(9.86, 36.8) * mm, "end": v(9.45, 35.5) * mm});
            skArc(sketch, "E12.7.34.0", {"start": v(9.86, 36.8) * mm, "mid": v(10.48, 37.56) * mm, "end": v(11.16, 38.25) * mm});
            skArc(sketch, "E12.11.34.0", {"start": v(11.9, 38.43) * mm, "mid": v(11.5, 38.44) * mm, "end": v(11.16, 38.25) * mm});
            skLineSegment(sketch, "E12.15.34.0", {"start": v(11.9, 38.43) * mm, "end": v(12.1, 38.38) * mm});
            skLineSegment(sketch, "E12.18.34.0", {"start": v(12.3, 38.3) * mm, "end": v(12.1, 38.38) * mm});
            skArc(sketch, "E12.21.34.0", {"start": v(12.8, 37.74) * mm, "mid": v(12.62, 38.09) * mm, "end": v(12.3, 38.3) * mm});
            skArc(sketch, "E12.25.34.0", {"start": v(13.03, 35.8) * mm, "mid": v(12.96, 36.78) * mm, "end": v(12.8, 37.74) * mm});
            skLineSegment(sketch, "E12.29.34.0", {"start": v(13.03, 35.8) * mm, "end": v(12.62, 34.5) * mm});
            skArc(sketch, "E12.32.34.0", {"start": v(12.62, 34.5) * mm, "mid": v(12.66, 33.91) * mm, "end": v(13.08, 33.52) * mm});
            skArc(sketch, "E12.2.35.0", {"start": v(2.3, 35.9) * mm, "mid": v(2.86, 36.09) * mm, "end": v(3.14, 36.6) * mm});
            skLineSegment(sketch, "E12.4.35.0", {"start": v(3.32, 37.96) * mm, "end": v(3.14, 36.6) * mm});
            skArc(sketch, "E12.7.35.0", {"start": v(3.32, 37.96) * mm, "mid": v(3.8, 38.8) * mm, "end": v(4.35, 39.61) * mm});
            skArc(sketch, "E12.11.35.0", {"start": v(5.04, 39.91) * mm, "mid": v(4.66, 39.85) * mm, "end": v(4.35, 39.61) * mm});
            skLineSegment(sketch, "E12.15.35.0", {"start": v(5.04, 39.91) * mm, "end": v(5.25, 39.9) * mm});
            skLineSegment(sketch, "E12.18.35.0", {"start": v(5.46, 39.86) * mm, "end": v(5.25, 39.9) * mm});
            skArc(sketch, "E12.21.35.0", {"start": v(6.05, 39.39) * mm, "mid": v(5.81, 39.7) * mm, "end": v(5.46, 39.86) * mm});
            skArc(sketch, "E12.25.35.0", {"start": v(6.62, 37.52) * mm, "mid": v(6.38, 38.47) * mm, "end": v(6.05, 39.39) * mm});
            skLineSegment(sketch, "E12.29.35.0", {"start": v(6.62, 37.52) * mm, "end": v(6.44, 36.16) * mm});
            skArc(sketch, "E12.32.35.0", {"start": v(6.44, 36.16) * mm, "mid": v(6.58, 35.6) * mm, "end": v(7.06, 35.28) * mm});
            skArc(sketch, "E13.trimOffspring", {"start": v(-10.11, 34.53) * mm, "mid": v(-10.82, 34.32) * mm, "end": v(-11.53, 34.09) * mm});
            skArc(sketch, "E14.trimOffspring", {"start": v(-15.95, 32.25) * mm, "mid": v(-16.62, 31.92) * mm, "end": v(-17.27, 31.57) * mm});
            skArc(sketch, "E15.trimOffspring", {"start": v(2.3, 35.9) * mm, "mid": v(1.57, 35.95) * mm, "end": v(0.83, 35.97) * mm});
            skArc(sketch, "E16.trimOffspring", {"start": v(8.51, 34.96) * mm, "mid": v(7.79, 35.13) * mm, "end": v(7.06, 35.28) * mm});
            skArc(sketch, "E17.trimOffspring", {"start": v(14.45, 32.95) * mm, "mid": v(13.77, 33.24) * mm, "end": v(13.08, 33.52) * mm});
            skArc(sketch, "E18.trimOffspring", {"start": v(19.96, 29.94) * mm, "mid": v(19.33, 30.35) * mm, "end": v(18.7, 30.74) * mm});
            skArc(sketch, "E19.trimOffspring", {"start": v(24.85, 26.02) * mm, "mid": v(24.3, 26.53) * mm, "end": v(23.76, 27.02) * mm});
            skArc(sketch, "E20.trimOffspring", {"start": v(29, 21.31) * mm, "mid": v(28.55, 21.9) * mm, "end": v(28.1, 22.49) * mm});
            skArc(sketch, "E21.trimOffspring", {"start": v(32.25, 15.95) * mm, "mid": v(31.92, 16.62) * mm, "end": v(31.57, 17.27) * mm});
            skArc(sketch, "E22.trimOffspring", {"start": v(34.53, 10.11) * mm, "mid": v(34.32, 10.82) * mm, "end": v(34.09, 11.53) * mm});
            skArc(sketch, "E23.trimOffspring", {"start": v(35.76, 3.96) * mm, "mid": v(35.68, 4.7) * mm, "end": v(35.57, 5.43) * mm});
            skArc(sketch, "E24.trimOffspring", {"start": v(-21.31, 29) * mm, "mid": v(-21.9, 28.55) * mm, "end": v(-22.49, 28.1) * mm});
            skArc(sketch, "E25.trimOffspring", {"start": v(-26.02, 24.85) * mm, "mid": v(-26.53, 24.3) * mm, "end": v(-27.02, 23.76) * mm});
            skArc(sketch, "E26.trimOffspring", {"start": v(-29.94, 19.96) * mm, "mid": v(-30.35, 19.33) * mm, "end": v(-30.74, 18.7) * mm});
            skArc(sketch, "E27.trimOffspring", {"start": v(-32.95, 14.45) * mm, "mid": v(-33.24, 13.77) * mm, "end": v(-33.52, 13.08) * mm});
            skArc(sketch, "E28.trimOffspring", {"start": v(-34.96, 8.51) * mm, "mid": v(-35.13, 7.79) * mm, "end": v(-35.28, 7.06) * mm});
            skArc(sketch, "E29.trimOffspring", {"start": v(-35.9, 2.3) * mm, "mid": v(-35.95, 1.57) * mm, "end": v(-35.97, 0.83) * mm});
            skArc(sketch, "E30.trimOffspring", {"start": v(-35.76, -3.96) * mm, "mid": v(-35.68, -4.7) * mm, "end": v(-35.57, -5.43) * mm});
            skArc(sketch, "E31.trimOffspring", {"start": v(-34.53, -10.11) * mm, "mid": v(-34.32, -10.82) * mm, "end": v(-34.09, -11.53) * mm});
            skArc(sketch, "E32.trimOffspring", {"start": v(-32.25, -15.95) * mm, "mid": v(-31.92, -16.62) * mm, "end": v(-31.57, -17.27) * mm});
            skArc(sketch, "E33.trimOffspring", {"start": v(-29, -21.31) * mm, "mid": v(-28.55, -21.9) * mm, "end": v(-28.1, -22.49) * mm});
            skArc(sketch, "E34.trimOffspring", {"start": v(-24.85, -26.02) * mm, "mid": v(-24.3, -26.53) * mm, "end": v(-23.76, -27.02) * mm});
            skArc(sketch, "E35.trimOffspring", {"start": v(-19.96, -29.94) * mm, "mid": v(-19.33, -30.35) * mm, "end": v(-18.7, -30.74) * mm});
            skArc(sketch, "E36.trimOffspring", {"start": v(-14.45, -32.95) * mm, "mid": v(-13.77, -33.24) * mm, "end": v(-13.08, -33.52) * mm});
            skArc(sketch, "E37.trimOffspring", {"start": v(-8.51, -34.96) * mm, "mid": v(-7.79, -35.13) * mm, "end": v(-7.06, -35.28) * mm});
            skArc(sketch, "E38.trimOffspring", {"start": v(-2.3, -35.9) * mm, "mid": v(-1.57, -35.95) * mm, "end": v(-0.83, -35.97) * mm});
            skArc(sketch, "E39.trimOffspring", {"start": v(3.96, -35.76) * mm, "mid": v(4.7, -35.68) * mm, "end": v(5.43, -35.57) * mm});
            skArc(sketch, "E40.trimOffspring", {"start": v(10.11, -34.53) * mm, "mid": v(10.82, -34.32) * mm, "end": v(11.53, -34.09) * mm});
            skArc(sketch, "E41.trimOffspring", {"start": v(15.95, -32.25) * mm, "mid": v(16.62, -31.92) * mm, "end": v(17.27, -31.57) * mm});
            skArc(sketch, "E42.trimOffspring", {"start": v(21.31, -29) * mm, "mid": v(21.9, -28.55) * mm, "end": v(22.49, -28.1) * mm});
            skArc(sketch, "E43.trimOffspring", {"start": v(26.02, -24.85) * mm, "mid": v(26.53, -24.3) * mm, "end": v(27.02, -23.76) * mm});
            skArc(sketch, "E44.trimOffspring", {"start": v(29.94, -19.96) * mm, "mid": v(30.35, -19.33) * mm, "end": v(30.74, -18.7) * mm});
            skArc(sketch, "E45.trimOffspring", {"start": v(32.95, -14.45) * mm, "mid": v(33.24, -13.77) * mm, "end": v(33.52, -13.08) * mm});
            skArc(sketch, "E46.trimOffspring", {"start": v(34.96, -8.51) * mm, "mid": v(35.13, -7.79) * mm, "end": v(35.28, -7.06) * mm});
            skArc(sketch, "E47.trimOffspring", {"start": v(35.9, -2.3) * mm, "mid": v(35.95, -1.57) * mm, "end": v(35.97, -0.83) * mm});
            skSolve(sketch);
        }
        {
            var Q0;
            Q0=makeQuery(id+"F0.imprint","IMPRINT",FACE,{"disambiguationData":[TD([[makeQuery(id+"F0.imprint","IMPRINT",EDGE,{"derivedFrom":sQuery(id+"F0.wireOp",EDGE,"E0")}),1.0]])]});
            extrude(context, id + "F1", {"entities" : qUnion([Q0]), "depth" : 6.35 * mm});
        }
        {
            var Q0;
            Q0=makeQuery(id+"F1.opExtrude","CAP_FACE",FACE,{"disambiguationData":[OSD([sQuery(id+"F0.wireOp",EDGE,"E0"),sQuery(id+"F0.wireOp",EDGE,"E1.trimOffspring"),sQuery(id+"F0.wireOp",EDGE,"E2"),sQuery(id+"F0.wireOp",EDGE,"E3"),sQuery(id+"F0.wireOp",EDGE,"E4.MirrorCS"),sQuery(id+"F0.wireOp",EDGE,"E5.MirrorCS"),sQuery(id+"F0.wireOp",EDGE,"E6.MirrorCS"),sQuery(id+"F0.wireOp",EDGE,"E7.filletArc"),sQuery(id+"F0.wireOp",EDGE,"E8.filletArc"),sQuery(id+"F0.wireOp",EDGE,"E9.filletArc"),sQuery(id+"F0.wireOp",EDGE,"E10.filletArc"),sQuery(id+"F0.wireOp",EDGE,"E11.1.0"),sQuery(id+"F0.wireOp",EDGE,"E11.1.1"),sQuery(id+"F0.wireOp",EDGE,"E11.1.2"),sQuery(id+"F0.wireOp",EDGE,"E11.1.3"),sQuery(id+"F0.wireOp",EDGE,"E11.1.4"),sQuery(id+"F0.wireOp",EDGE,"E11.1.5"),sQuery(id+"F0.wireOp",EDGE,"E11.1.6"),sQuery(id+"F0.wireOp",EDGE,"E11.1.7"),sQuery(id+"F0.wireOp",EDGE,"E11.1.8"),sQuery(id+"F0.wireOp",EDGE,"E11.1.9"),sQuery(id+"F0.wireOp",EDGE,"E11.2.0"),sQuery(id+"F0.wireOp",EDGE,"E11.2.1"),sQuery(id+"F0.wireOp",EDGE,"E11.2.2"),sQuery(id+"F0.wireOp",EDGE,"E11.2.3"),sQuery(id+"F0.wireOp",EDGE,"E11.2.4"),sQuery(id+"F0.wireOp",EDGE,"E11.2.5"),sQuery(id+"F0.wireOp",EDGE,"E11.2.6"),sQuery(id+"F0.wireOp",EDGE,"E11.2.7"),sQuery(id+"F0.wireOp",EDGE,"E11.2.8"),sQuery(id+"F0.wireOp",EDGE,"E11.2.9"),sQuery(id+"F0.wireOp",EDGE,"E12.2.3.0"),sQuery(id+"F0.wireOp",EDGE,"E12.4.3.0"),sQuery(id+"F0.wireOp",EDGE,"E12.7.3.0"),sQuery(id+"F0.wireOp",EDGE,"E12.11.3.0"),sQuery(id+"F0.wireOp",EDGE,"E12.15.3.0"),sQuery(id+"F0.wireOp",EDGE,"E12.18.3.0"),sQuery(id+"F0.wireOp",EDGE,"E12.21.3.0"),sQuery(id+"F0.wireOp",EDGE,"E12.25.3.0"),sQuery(id+"F0.wireOp",EDGE,"E12.29.3.0"),sQuery(id+"F0.wireOp",EDGE,"E12.32.3.0"),sQuery(id+"F0.wireOp",EDGE,"E12.2.4.0"),sQuery(id+"F0.wireOp",EDGE,"E12.4.4.0"),sQuery(id+"F0.wireOp",EDGE,"E12.7.4.0"),sQuery(id+"F0.wireOp",EDGE,"E12.11.4.0"),sQuery(id+"F0.wireOp",EDGE,"E12.15.4.0"),sQuery(id+"F0.wireOp",EDGE,"E12.18.4.0"),sQuery(id+"F0.wireOp",EDGE,"E12.21.4.0"),sQuery(id+"F0.wireOp",EDGE,"E12.25.4.0"),sQuery(id+"F0.wireOp",EDGE,"E12.29.4.0"),sQuery(id+"F0.wireOp",EDGE,"E12.32.4.0"),sQuery(id+"F0.wireOp",EDGE,"E12.2.5.0"),sQuery(id+"F0.wireOp",EDGE,"E12.4.5.0"),sQuery(id+"F0.wireOp",EDGE,"E12.7.5.0"),sQuery(id+"F0.wireOp",EDGE,"E12.11.5.0"),sQuery(id+"F0.wireOp",EDGE,"E12.15.5.0"),sQuery(id+"F0.wireOp",EDGE,"E12.18.5.0"),sQuery(id+"F0.wireOp",EDGE,"E12.21.5.0"),sQuery(id+"F0.wireOp",EDGE,"E12.25.5.0"),sQuery(id+"F0.wireOp",EDGE,"E12.29.5.0"),sQuery(id+"F0.wireOp",EDGE,"E12.32.5.0"),sQuery(id+"F0.wireOp",EDGE,"E12.2.6.0"),sQuery(id+"F0.wireOp",EDGE,"E12.4.6.0"),sQuery(id+"F0.wireOp",EDGE,"E12.7.6.0"),sQuery(id+"F0.wireOp",EDGE,"E12.11.6.0"),sQuery(id+"F0.wireOp",EDGE,"E12.15.6.0"),sQuery(id+"F0.wireOp",EDGE,"E12.18.6.0"),sQuery(id+"F0.wireOp",EDGE,"E12.21.6.0"),sQuery(id+"F0.wireOp",EDGE,"E12.25.6.0"),sQuery(id+"F0.wireOp",EDGE,"E12.29.6.0"),sQuery(id+"F0.wireOp",EDGE,"E12.32.6.0"),sQuery(id+"F0.wireOp",EDGE,"E12.2.7.0"),sQuery(id+"F0.wireOp",EDGE,"E12.4.7.0"),sQuery(id+"F0.wireOp",EDGE,"E12.7.7.0"),sQuery(id+"F0.wireOp",EDGE,"E12.11.7.0"),sQuery(id+"F0.wireOp",EDGE,"E12.15.7.0"),sQuery(id+"F0.wireOp",EDGE,"E12.18.7.0"),sQuery(id+"F0.wireOp",EDGE,"E12.21.7.0"),sQuery(id+"F0.wireOp",EDGE,"E12.25.7.0"),sQuery(id+"F0.wireOp",EDGE,"E12.29.7.0"),sQuery(id+"F0.wireOp",EDGE,"E12.32.7.0"),sQuery(id+"F0.wireOp",EDGE,"E12.2.8.0"),sQuery(id+"F0.wireOp",EDGE,"E12.4.8.0"),sQuery(id+"F0.wireOp",EDGE,"E12.7.8.0"),sQuery(id+"F0.wireOp",EDGE,"E12.11.8.0"),sQuery(id+"F0.wireOp",EDGE,"E12.15.8.0"),sQuery(id+"F0.wireOp",EDGE,"E12.18.8.0"),sQuery(id+"F0.wireOp",EDGE,"E12.21.8.0"),sQuery(id+"F0.wireOp",EDGE,"E12.25.8.0"),sQuery(id+"F0.wireOp",EDGE,"E12.29.8.0"),sQuery(id+"F0.wireOp",EDGE,"E12.32.8.0"),sQuery(id+"F0.wireOp",EDGE,"E12.2.9.0"),sQuery(id+"F0.wireOp",EDGE,"E12.4.9.0"),sQuery(id+"F0.wireOp",EDGE,"E12.7.9.0"),sQuery(id+"F0.wireOp",EDGE,"E12.11.9.0"),sQuery(id+"F0.wireOp",EDGE,"E12.15.9.0"),sQuery(id+"F0.wireOp",EDGE,"E12.18.9.0"),sQuery(id+"F0.wireOp",EDGE,"E12.21.9.0"),sQuery(id+"F0.wireOp",EDGE,"E12.25.9.0"),sQuery(id+"F0.wireOp",EDGE,"E12.29.9.0"),sQuery(id+"F0.wireOp",EDGE,"E12.32.9.0"),sQuery(id+"F0.wireOp",EDGE,"E12.2.10.0"),sQuery(id+"F0.wireOp",EDGE,"E12.4.10.0"),sQuery(id+"F0.wireOp",EDGE,"E12.7.10.0"),sQuery(id+"F0.wireOp",EDGE,"E12.11.10.0"),sQuery(id+"F0.wireOp",EDGE,"E12.15.10.0"),sQuery(id+"F0.wireOp",EDGE,"E12.18.10.0"),sQuery(id+"F0.wireOp",EDGE,"E12.21.10.0"),sQuery(id+"F0.wireOp",EDGE,"E12.25.10.0"),sQuery(id+"F0.wireOp",EDGE,"E12.29.10.0"),sQuery(id+"F0.wireOp",EDGE,"E12.32.10.0"),sQuery(id+"F0.wireOp",EDGE,"E12.2.11.0"),sQuery(id+"F0.wireOp",EDGE,"E12.4.11.0"),sQuery(id+"F0.wireOp",EDGE,"E12.7.11.0"),sQuery(id+"F0.wireOp",EDGE,"E12.11.11.0"),sQuery(id+"F0.wireOp",EDGE,"E12.15.11.0"),sQuery(id+"F0.wireOp",EDGE,"E12.18.11.0"),sQuery(id+"F0.wireOp",EDGE,"E12.21.11.0"),sQuery(id+"F0.wireOp",EDGE,"E12.25.11.0"),sQuery(id+"F0.wireOp",EDGE,"E12.29.11.0"),sQuery(id+"F0.wireOp",EDGE,"E12.32.11.0"),sQuery(id+"F0.wireOp",EDGE,"E12.2.12.0"),sQuery(id+"F0.wireOp",EDGE,"E12.4.12.0"),sQuery(id+"F0.wireOp",EDGE,"E12.7.12.0"),sQuery(id+"F0.wireOp",EDGE,"E12.11.12.0"),sQuery(id+"F0.wireOp",EDGE,"E12.15.12.0"),sQuery(id+"F0.wireOp",EDGE,"E12.18.12.0"),sQuery(id+"F0.wireOp",EDGE,"E12.21.12.0"),sQuery(id+"F0.wireOp",EDGE,"E12.25.12.0"),sQuery(id+"F0.wireOp",EDGE,"E12.29.12.0"),sQuery(id+"F0.wireOp",EDGE,"E12.32.12.0"),sQuery(id+"F0.wireOp",EDGE,"E12.2.13.0"),sQuery(id+"F0.wireOp",EDGE,"E12.4.13.0"),sQuery(id+"F0.wireOp",EDGE,"E12.7.13.0"),sQuery(id+"F0.wireOp",EDGE,"E12.11.13.0"),sQuery(id+"F0.wireOp",EDGE,"E12.15.13.0"),sQuery(id+"F0.wireOp",EDGE,"E12.18.13.0"),sQuery(id+"F0.wireOp",EDGE,"E12.21.13.0"),sQuery(id+"F0.wireOp",EDGE,"E12.25.13.0"),sQuery(id+"F0.wireOp",EDGE,"E12.29.13.0"),sQuery(id+"F0.wireOp",EDGE,"E12.32.13.0"),sQuery(id+"F0.wireOp",EDGE,"E12.2.14.0"),sQuery(id+"F0.wireOp",EDGE,"E12.4.14.0"),sQuery(id+"F0.wireOp",EDGE,"E12.7.14.0"),sQuery(id+"F0.wireOp",EDGE,"E12.11.14.0"),sQuery(id+"F0.wireOp",EDGE,"E12.15.14.0"),sQuery(id+"F0.wireOp",EDGE,"E12.18.14.0"),sQuery(id+"F0.wireOp",EDGE,"E12.21.14.0"),sQuery(id+"F0.wireOp",EDGE,"E12.25.14.0"),sQuery(id+"F0.wireOp",EDGE,"E12.29.14.0"),sQuery(id+"F0.wireOp",EDGE,"E12.32.14.0"),sQuery(id+"F0.wireOp",EDGE,"E12.2.15.0"),sQuery(id+"F0.wireOp",EDGE,"E12.4.15.0"),sQuery(id+"F0.wireOp",EDGE,"E12.7.15.0"),sQuery(id+"F0.wireOp",EDGE,"E12.11.15.0"),sQuery(id+"F0.wireOp",EDGE,"E12.15.15.0"),sQuery(id+"F0.wireOp",EDGE,"E12.18.15.0"),sQuery(id+"F0.wireOp",EDGE,"E12.21.15.0"),sQuery(id+"F0.wireOp",EDGE,"E12.25.15.0"),sQuery(id+"F0.wireOp",EDGE,"E12.29.15.0"),sQuery(id+"F0.wireOp",EDGE,"E12.32.15.0"),sQuery(id+"F0.wireOp",EDGE,"E12.2.16.0"),sQuery(id+"F0.wireOp",EDGE,"E12.4.16.0"),sQuery(id+"F0.wireOp",EDGE,"E12.7.16.0"),sQuery(id+"F0.wireOp",EDGE,"E12.11.16.0"),sQuery(id+"F0.wireOp",EDGE,"E12.15.16.0"),sQuery(id+"F0.wireOp",EDGE,"E12.18.16.0"),sQuery(id+"F0.wireOp",EDGE,"E12.21.16.0"),sQuery(id+"F0.wireOp",EDGE,"E12.25.16.0"),sQuery(id+"F0.wireOp",EDGE,"E12.29.16.0"),sQuery(id+"F0.wireOp",EDGE,"E12.32.16.0"),sQuery(id+"F0.wireOp",EDGE,"E12.2.17.0"),sQuery(id+"F0.wireOp",EDGE,"E12.4.17.0"),sQuery(id+"F0.wireOp",EDGE,"E12.7.17.0"),sQuery(id+"F0.wireOp",EDGE,"E12.11.17.0"),sQuery(id+"F0.wireOp",EDGE,"E12.15.17.0"),sQuery(id+"F0.wireOp",EDGE,"E12.18.17.0"),sQuery(id+"F0.wireOp",EDGE,"E12.21.17.0"),sQuery(id+"F0.wireOp",EDGE,"E12.25.17.0"),sQuery(id+"F0.wireOp",EDGE,"E12.29.17.0"),sQuery(id+"F0.wireOp",EDGE,"E12.32.17.0"),sQuery(id+"F0.wireOp",EDGE,"E12.2.18.0"),sQuery(id+"F0.wireOp",EDGE,"E12.4.18.0"),sQuery(id+"F0.wireOp",EDGE,"E12.7.18.0"),sQuery(id+"F0.wireOp",EDGE,"E12.11.18.0"),sQuery(id+"F0.wireOp",EDGE,"E12.15.18.0"),sQuery(id+"F0.wireOp",EDGE,"E12.18.18.0"),sQuery(id+"F0.wireOp",EDGE,"E12.21.18.0"),sQuery(id+"F0.wireOp",EDGE,"E12.25.18.0"),sQuery(id+"F0.wireOp",EDGE,"E12.29.18.0"),sQuery(id+"F0.wireOp",EDGE,"E12.32.18.0"),sQuery(id+"F0.wireOp",EDGE,"E12.2.19.0"),sQuery(id+"F0.wireOp",EDGE,"E12.4.19.0"),sQuery(id+"F0.wireOp",EDGE,"E12.7.19.0"),sQuery(id+"F0.wireOp",EDGE,"E12.11.19.0"),sQuery(id+"F0.wireOp",EDGE,"E12.15.19.0"),sQuery(id+"F0.wireOp",EDGE,"E12.18.19.0"),sQuery(id+"F0.wireOp",EDGE,"E12.21.19.0"),sQuery(id+"F0.wireOp",EDGE,"E12.25.19.0"),sQuery(id+"F0.wireOp",EDGE,"E12.29.19.0"),sQuery(id+"F0.wireOp",EDGE,"E12.32.19.0"),sQuery(id+"F0.wireOp",EDGE,"E12.2.20.0"),sQuery(id+"F0.wireOp",EDGE,"E12.4.20.0"),sQuery(id+"F0.wireOp",EDGE,"E12.7.20.0"),sQuery(id+"F0.wireOp",EDGE,"E12.11.20.0"),sQuery(id+"F0.wireOp",EDGE,"E12.15.20.0"),sQuery(id+"F0.wireOp",EDGE,"E12.18.20.0"),sQuery(id+"F0.wireOp",EDGE,"E12.21.20.0"),sQuery(id+"F0.wireOp",EDGE,"E12.25.20.0"),sQuery(id+"F0.wireOp",EDGE,"E12.29.20.0"),sQuery(id+"F0.wireOp",EDGE,"E12.32.20.0"),sQuery(id+"F0.wireOp",EDGE,"E12.2.21.0"),sQuery(id+"F0.wireOp",EDGE,"E12.4.21.0"),sQuery(id+"F0.wireOp",EDGE,"E12.7.21.0"),sQuery(id+"F0.wireOp",EDGE,"E12.11.21.0"),sQuery(id+"F0.wireOp",EDGE,"E12.15.21.0"),sQuery(id+"F0.wireOp",EDGE,"E12.18.21.0"),sQuery(id+"F0.wireOp",EDGE,"E12.21.21.0"),sQuery(id+"F0.wireOp",EDGE,"E12.25.21.0"),sQuery(id+"F0.wireOp",EDGE,"E12.29.21.0"),sQuery(id+"F0.wireOp",EDGE,"E12.32.21.0"),sQuery(id+"F0.wireOp",EDGE,"E12.2.22.0"),sQuery(id+"F0.wireOp",EDGE,"E12.4.22.0"),sQuery(id+"F0.wireOp",EDGE,"E12.7.22.0"),sQuery(id+"F0.wireOp",EDGE,"E12.11.22.0"),sQuery(id+"F0.wireOp",EDGE,"E12.15.22.0"),sQuery(id+"F0.wireOp",EDGE,"E12.18.22.0"),sQuery(id+"F0.wireOp",EDGE,"E12.21.22.0"),sQuery(id+"F0.wireOp",EDGE,"E12.25.22.0"),sQuery(id+"F0.wireOp",EDGE,"E12.29.22.0"),sQuery(id+"F0.wireOp",EDGE,"E12.32.22.0"),sQuery(id+"F0.wireOp",EDGE,"E12.2.23.0"),sQuery(id+"F0.wireOp",EDGE,"E12.4.23.0"),sQuery(id+"F0.wireOp",EDGE,"E12.7.23.0"),sQuery(id+"F0.wireOp",EDGE,"E12.11.23.0"),sQuery(id+"F0.wireOp",EDGE,"E12.15.23.0"),sQuery(id+"F0.wireOp",EDGE,"E12.18.23.0"),sQuery(id+"F0.wireOp",EDGE,"E12.21.23.0"),sQuery(id+"F0.wireOp",EDGE,"E12.25.23.0"),sQuery(id+"F0.wireOp",EDGE,"E12.29.23.0"),sQuery(id+"F0.wireOp",EDGE,"E12.32.23.0"),sQuery(id+"F0.wireOp",EDGE,"E12.2.24.0"),sQuery(id+"F0.wireOp",EDGE,"E12.4.24.0"),sQuery(id+"F0.wireOp",EDGE,"E12.7.24.0"),sQuery(id+"F0.wireOp",EDGE,"E12.11.24.0"),sQuery(id+"F0.wireOp",EDGE,"E12.15.24.0"),sQuery(id+"F0.wireOp",EDGE,"E12.18.24.0"),sQuery(id+"F0.wireOp",EDGE,"E12.21.24.0"),sQuery(id+"F0.wireOp",EDGE,"E12.25.24.0"),sQuery(id+"F0.wireOp",EDGE,"E12.29.24.0"),sQuery(id+"F0.wireOp",EDGE,"E12.32.24.0"),sQuery(id+"F0.wireOp",EDGE,"E12.2.25.0"),sQuery(id+"F0.wireOp",EDGE,"E12.4.25.0"),sQuery(id+"F0.wireOp",EDGE,"E12.7.25.0"),sQuery(id+"F0.wireOp",EDGE,"E12.11.25.0"),sQuery(id+"F0.wireOp",EDGE,"E12.15.25.0"),sQuery(id+"F0.wireOp",EDGE,"E12.18.25.0"),sQuery(id+"F0.wireOp",EDGE,"E12.21.25.0"),sQuery(id+"F0.wireOp",EDGE,"E12.25.25.0"),sQuery(id+"F0.wireOp",EDGE,"E12.29.25.0"),sQuery(id+"F0.wireOp",EDGE,"E12.32.25.0"),sQuery(id+"F0.wireOp",EDGE,"E12.2.26.0"),sQuery(id+"F0.wireOp",EDGE,"E12.4.26.0"),sQuery(id+"F0.wireOp",EDGE,"E12.7.26.0"),sQuery(id+"F0.wireOp",EDGE,"E12.11.26.0"),sQuery(id+"F0.wireOp",EDGE,"E12.15.26.0"),sQuery(id+"F0.wireOp",EDGE,"E12.18.26.0"),sQuery(id+"F0.wireOp",EDGE,"E12.21.26.0"),sQuery(id+"F0.wireOp",EDGE,"E12.25.26.0"),sQuery(id+"F0.wireOp",EDGE,"E12.29.26.0"),sQuery(id+"F0.wireOp",EDGE,"E12.32.26.0"),sQuery(id+"F0.wireOp",EDGE,"E12.2.27.0"),sQuery(id+"F0.wireOp",EDGE,"E12.4.27.0"),sQuery(id+"F0.wireOp",EDGE,"E12.7.27.0"),sQuery(id+"F0.wireOp",EDGE,"E12.11.27.0"),sQuery(id+"F0.wireOp",EDGE,"E12.15.27.0"),sQuery(id+"F0.wireOp",EDGE,"E12.18.27.0"),sQuery(id+"F0.wireOp",EDGE,"E12.21.27.0"),sQuery(id+"F0.wireOp",EDGE,"E12.25.27.0"),sQuery(id+"F0.wireOp",EDGE,"E12.29.27.0"),sQuery(id+"F0.wireOp",EDGE,"E12.32.27.0"),sQuery(id+"F0.wireOp",EDGE,"E12.2.28.0"),sQuery(id+"F0.wireOp",EDGE,"E12.4.28.0"),sQuery(id+"F0.wireOp",EDGE,"E12.7.28.0"),sQuery(id+"F0.wireOp",EDGE,"E12.11.28.0"),sQuery(id+"F0.wireOp",EDGE,"E12.15.28.0"),sQuery(id+"F0.wireOp",EDGE,"E12.18.28.0"),sQuery(id+"F0.wireOp",EDGE,"E12.21.28.0"),sQuery(id+"F0.wireOp",EDGE,"E12.25.28.0"),sQuery(id+"F0.wireOp",EDGE,"E12.29.28.0"),sQuery(id+"F0.wireOp",EDGE,"E12.32.28.0"),sQuery(id+"F0.wireOp",EDGE,"E12.2.29.0"),sQuery(id+"F0.wireOp",EDGE,"E12.4.29.0"),sQuery(id+"F0.wireOp",EDGE,"E12.7.29.0"),sQuery(id+"F0.wireOp",EDGE,"E12.11.29.0"),sQuery(id+"F0.wireOp",EDGE,"E12.15.29.0"),sQuery(id+"F0.wireOp",EDGE,"E12.18.29.0"),sQuery(id+"F0.wireOp",EDGE,"E12.21.29.0"),sQuery(id+"F0.wireOp",EDGE,"E12.25.29.0"),sQuery(id+"F0.wireOp",EDGE,"E12.29.29.0"),sQuery(id+"F0.wireOp",EDGE,"E12.32.29.0"),sQuery(id+"F0.wireOp",EDGE,"E12.2.30.0"),sQuery(id+"F0.wireOp",EDGE,"E12.4.30.0"),sQuery(id+"F0.wireOp",EDGE,"E12.7.30.0"),sQuery(id+"F0.wireOp",EDGE,"E12.11.30.0"),sQuery(id+"F0.wireOp",EDGE,"E12.15.30.0"),sQuery(id+"F0.wireOp",EDGE,"E12.18.30.0"),sQuery(id+"F0.wireOp",EDGE,"E12.21.30.0"),sQuery(id+"F0.wireOp",EDGE,"E12.25.30.0"),sQuery(id+"F0.wireOp",EDGE,"E12.29.30.0"),sQuery(id+"F0.wireOp",EDGE,"E12.32.30.0"),sQuery(id+"F0.wireOp",EDGE,"E12.2.31.0"),sQuery(id+"F0.wireOp",EDGE,"E12.4.31.0"),sQuery(id+"F0.wireOp",EDGE,"E12.7.31.0"),sQuery(id+"F0.wireOp",EDGE,"E12.11.31.0"),sQuery(id+"F0.wireOp",EDGE,"E12.15.31.0"),sQuery(id+"F0.wireOp",EDGE,"E12.18.31.0"),sQuery(id+"F0.wireOp",EDGE,"E12.21.31.0"),sQuery(id+"F0.wireOp",EDGE,"E12.25.31.0"),sQuery(id+"F0.wireOp",EDGE,"E12.29.31.0"),sQuery(id+"F0.wireOp",EDGE,"E12.32.31.0"),sQuery(id+"F0.wireOp",EDGE,"E12.2.32.0"),sQuery(id+"F0.wireOp",EDGE,"E12.4.32.0"),sQuery(id+"F0.wireOp",EDGE,"E12.7.32.0"),sQuery(id+"F0.wireOp",EDGE,"E12.11.32.0"),sQuery(id+"F0.wireOp",EDGE,"E12.15.32.0"),sQuery(id+"F0.wireOp",EDGE,"E12.18.32.0"),sQuery(id+"F0.wireOp",EDGE,"E12.21.32.0"),sQuery(id+"F0.wireOp",EDGE,"E12.25.32.0"),sQuery(id+"F0.wireOp",EDGE,"E12.29.32.0"),sQuery(id+"F0.wireOp",EDGE,"E12.32.32.0"),sQuery(id+"F0.wireOp",EDGE,"E12.2.33.0"),sQuery(id+"F0.wireOp",EDGE,"E12.4.33.0"),sQuery(id+"F0.wireOp",EDGE,"E12.7.33.0"),sQuery(id+"F0.wireOp",EDGE,"E12.11.33.0"),sQuery(id+"F0.wireOp",EDGE,"E12.15.33.0"),sQuery(id+"F0.wireOp",EDGE,"E12.18.33.0"),sQuery(id+"F0.wireOp",EDGE,"E12.21.33.0"),sQuery(id+"F0.wireOp",EDGE,"E12.25.33.0"),sQuery(id+"F0.wireOp",EDGE,"E12.29.33.0"),sQuery(id+"F0.wireOp",EDGE,"E12.32.33.0"),sQuery(id+"F0.wireOp",EDGE,"E12.2.34.0"),sQuery(id+"F0.wireOp",EDGE,"E12.4.34.0"),sQuery(id+"F0.wireOp",EDGE,"E12.7.34.0"),sQuery(id+"F0.wireOp",EDGE,"E12.11.34.0"),sQuery(id+"F0.wireOp",EDGE,"E12.15.34.0"),sQuery(id+"F0.wireOp",EDGE,"E12.18.34.0"),sQuery(id+"F0.wireOp",EDGE,"E12.21.34.0"),sQuery(id+"F0.wireOp",EDGE,"E12.25.34.0"),sQuery(id+"F0.wireOp",EDGE,"E12.29.34.0"),sQuery(id+"F0.wireOp",EDGE,"E12.32.34.0"),sQuery(id+"F0.wireOp",EDGE,"E12.2.35.0"),sQuery(id+"F0.wireOp",EDGE,"E12.4.35.0"),sQuery(id+"F0.wireOp",EDGE,"E12.7.35.0"),sQuery(id+"F0.wireOp",EDGE,"E12.11.35.0"),sQuery(id+"F0.wireOp",EDGE,"E12.15.35.0"),sQuery(id+"F0.wireOp",EDGE,"E12.18.35.0"),sQuery(id+"F0.wireOp",EDGE,"E12.21.35.0"),sQuery(id+"F0.wireOp",EDGE,"E12.25.35.0"),sQuery(id+"F0.wireOp",EDGE,"E12.29.35.0"),sQuery(id+"F0.wireOp",EDGE,"E12.32.35.0"),sQuery(id+"F0.wireOp",EDGE,"E13.trimOffspring"),sQuery(id+"F0.wireOp",EDGE,"E14.trimOffspring"),sQuery(id+"F0.wireOp",EDGE,"E15.trimOffspring"),sQuery(id+"F0.wireOp",EDGE,"E16.trimOffspring"),sQuery(id+"F0.wireOp",EDGE,"E17.trimOffspring"),sQuery(id+"F0.wireOp",EDGE,"E18.trimOffspring"),sQuery(id+"F0.wireOp",EDGE,"E19.trimOffspring"),sQuery(id+"F0.wireOp",EDGE,"E20.trimOffspring"),sQuery(id+"F0.wireOp",EDGE,"E21.trimOffspring"),sQuery(id+"F0.wireOp",EDGE,"E22.trimOffspring"),sQuery(id+"F0.wireOp",EDGE,"E23.trimOffspring"),sQuery(id+"F0.wireOp",EDGE,"E24.trimOffspring"),sQuery(id+"F0.wireOp",EDGE,"E25.trimOffspring"),sQuery(id+"F0.wireOp",EDGE,"E26.trimOffspring"),sQuery(id+"F0.wireOp",EDGE,"E27.trimOffspring"),sQuery(id+"F0.wireOp",EDGE,"E28.trimOffspring"),sQuery(id+"F0.wireOp",EDGE,"E29.trimOffspring"),sQuery(id+"F0.wireOp",EDGE,"E30.trimOffspring"),sQuery(id+"F0.wireOp",EDGE,"E31.trimOffspring"),sQuery(id+"F0.wireOp",EDGE,"E32.trimOffspring"),sQuery(id+"F0.wireOp",EDGE,"E33.trimOffspring"),sQuery(id+"F0.wireOp",EDGE,"E34.trimOffspring"),sQuery(id+"F0.wireOp",EDGE,"E35.trimOffspring"),sQuery(id+"F0.wireOp",EDGE,"E36.trimOffspring"),sQuery(id+"F0.wireOp",EDGE,"E37.trimOffspring"),sQuery(id+"F0.wireOp",EDGE,"E38.trimOffspring"),sQuery(id+"F0.wireOp",EDGE,"E39.trimOffspring"),sQuery(id+"F0.wireOp",EDGE,"E40.trimOffspring"),sQuery(id+"F0.wireOp",EDGE,"E41.trimOffspring"),sQuery(id+"F0.wireOp",EDGE,"E42.trimOffspring"),sQuery(id+"F0.wireOp",EDGE,"E43.trimOffspring"),sQuery(id+"F0.wireOp",EDGE,"E44.trimOffspring"),sQuery(id+"F0.wireOp",EDGE,"E45.trimOffspring"),sQuery(id+"F0.wireOp",EDGE,"E46.trimOffspring"),sQuery(id+"F0.wireOp",EDGE,"E47.trimOffspring")])],"isStart":false});
            var sketch = newSketch(context, id + "F2", { "sketchPlane" : qUnion([Q0])});
            skPoint(sketch, "E48", {"position": v(0, 0) * mm});
            skPoint(sketch, "E49", {"position": v(0, 9.53) * mm});
            skPoint(sketch, "E50", {"position": v(0, 30.18) * mm});
            skPoint(sketch, "E51", {"position": v(0, 12.7) * mm});
            skPoint(sketch, "E52", {"position": v(0, 19.05) * mm});
            skArc(sketch, "E53", {"start": v(0, 31.76) * mm, "mid": v(-1.59, 30.18) * mm, "end": v(0, 28.59) * mm});
            skArc(sketch, "E54.1.0", {"start": v(-20.21, 20.21) * mm, "mid": v(-20.21, 22.46) * mm, "end": v(-22.46, 22.46) * mm});
            skArc(sketch, "E54.2.0", {"start": v(-31.76, 0) * mm, "mid": v(-30.18, -1.59) * mm, "end": v(-28.59, 0) * mm});
            skArc(sketch, "E54.3.0", {"start": v(-20.21, -20.21) * mm, "mid": v(-22.46, -20.21) * mm, "end": v(-22.46, -22.46) * mm});
            skArc(sketch, "E54.4.0", {"start": v(0, -31.76) * mm, "mid": v(1.59, -30.18) * mm, "end": v(0, -28.59) * mm});
            skArc(sketch, "E54.5.0", {"start": v(20.21, -20.21) * mm, "mid": v(20.21, -22.46) * mm, "end": v(22.46, -22.46) * mm});
            skArc(sketch, "E54.6.0", {"start": v(31.76, 0) * mm, "mid": v(30.18, 1.59) * mm, "end": v(28.59, 0) * mm});
            skArc(sketch, "E54.7.0", {"start": v(20.21, 20.21) * mm, "mid": v(22.46, 20.21) * mm, "end": v(22.46, 22.46) * mm});
            skArc(sketch, "E55", {"start": v(-22.46, 22.46) * mm, "mid": v(-29.34, 12.16) * mm, "end": v(-31.76, 0) * mm});
            skArc(sketch, "E56", {"start": v(-20.21, 20.21) * mm, "mid": v(-26.41, 10.94) * mm, "end": v(-28.59, 0) * mm});
            skArc(sketch, "E57.trimOffspring", {"start": v(20.21, 20.21) * mm, "mid": v(10.94, 26.41) * mm, "end": v(0, 28.59) * mm});
            skArc(sketch, "E58.trimOffspring", {"start": v(22.46, 22.46) * mm, "mid": v(12.16, 29.34) * mm, "end": v(0, 31.76) * mm});
            skArc(sketch, "E59.trimOffspring", {"start": v(-20.21, -20.21) * mm, "mid": v(-10.94, -26.41) * mm, "end": v(0, -28.59) * mm});
            skArc(sketch, "E60.trimOffspring", {"start": v(-22.46, -22.46) * mm, "mid": v(-12.16, -29.34) * mm, "end": v(0, -31.76) * mm});
            skArc(sketch, "E61.trimOffspring", {"start": v(20.21, -20.21) * mm, "mid": v(26.41, -10.94) * mm, "end": v(28.59, 0) * mm});
            skArc(sketch, "E62.trimOffspring", {"start": v(22.46, -22.46) * mm, "mid": v(29.34, -12.16) * mm, "end": v(31.76, 0) * mm});
            skLineSegment(sketch, "E63", {"start": v(0, 0) * mm, "end": v(0.03, 47.97) * mm, "construction": true});
            skPoint(sketch, "E63.endSnap0", {"position": v(0.03, 37.41) * mm});
            skCircle(sketch, "E64", {"center": v(0, 19.05) * mm, "radius": 2.22 * mm});
            skCircle(sketch, "E65.1.0", {"center": v(-9.52, 16.5) * mm, "radius": 2.22 * mm});
            skCircle(sketch, "E65.2.0", {"center": v(-16.5, 9.53) * mm, "radius": 2.22 * mm});
            skCircle(sketch, "E65.3.0", {"center": v(-19.05, 0) * mm, "radius": 2.22 * mm});
            skCircle(sketch, "E65.4.0", {"center": v(-16.5, -9.52) * mm, "radius": 2.22 * mm});
            skCircle(sketch, "E65.5.0", {"center": v(-9.52, -16.5) * mm, "radius": 2.22 * mm});
            skCircle(sketch, "E65.6.0", {"center": v(0, -19.05) * mm, "radius": 2.22 * mm});
            skCircle(sketch, "E65.7.0", {"center": v(9.52, -16.5) * mm, "radius": 2.22 * mm});
            skCircle(sketch, "E65.8.0", {"center": v(16.5, -9.53) * mm, "radius": 2.22 * mm});
            skCircle(sketch, "E65.9.0", {"center": v(19.05, 0) * mm, "radius": 2.22 * mm});
            skCircle(sketch, "E65.10.0", {"center": v(16.5, 9.53) * mm, "radius": 2.22 * mm});
            skCircle(sketch, "E65.11.0", {"center": v(9.53, 16.5) * mm, "radius": 2.22 * mm});
            skSolve(sketch);
        }
        {
            var Q0;
            Q0 = qSketchRegion(id + "F2", true);
            extrude(context, id + "F3", {"entities" : qUnion([Q0]), "operationType" : NewBodyOperationType.REMOVE, "oppositeDirection" : true, "depth" : 25.4 * mm});
        }
        {
            var Q0;
            Q0=makeQuery(id+"F2.imprint","IMPRINT",FACE,{"disambiguationData":[TD([[makeQuery(id+"F2.imprint","IMPRINT",EDGE,{"derivedFrom":sQuery(id+"F2.wireOp",EDGE,"E53")}),-1.0]])]});
            var sketch = newSketch(context, id + "F4", { "sketchPlane" : qUnion([Q0])});
            skCircle(sketch, "E66", {"center": v(0, 0) * mm, "radius": 12.7 * mm});
            skSolve(sketch);
        }
        {
            var Q0;
            Q0 = qSketchRegion(id + "F4", true);
            extrude(context, id + "F5", {"entities" : qUnion([Q0]), "operationType" : NewBodyOperationType.ADD, "depth" : 6.35 * mm});
        }
        {
            var Q0;
            Q0=makeQuery(id+"F5.opExtrude","CAP_FACE",FACE,{"disambiguationData":[OSD([sQuery(id+"F4.wireOp",EDGE,"E66")])],"isStart":false});
            var sketch = newSketch(context, id + "F6", { "sketchPlane" : qUnion([Q0])});
            skPoint(sketch, "E67", {"position": v(0, 9.53) * mm});
            skPoint(sketch, "E68.1.0", {"position": v(-8.25, 4.76) * mm});
            skPoint(sketch, "E68.2.0", {"position": v(-8.25, -4.76) * mm});
            skPoint(sketch, "E68.3.0", {"position": v(0, -9.53) * mm});
            skPoint(sketch, "E68.4.0", {"position": v(8.25, -4.76) * mm});
            skPoint(sketch, "E68.5.0", {"position": v(8.25, 4.76) * mm});
            skPoint(sketch, "E68.center", {"position": v(0, 0) * mm});
            skSolve(sketch);
        }
        {
            var Q0;
            Q0=sQuery(id+"F6.wireOp",VERTEX,"E67");
            var Q1;
            Q1=sQuery(id+"F6.wireOp",VERTEX,"E68.5.0");
            var Q2;
            Q2=sQuery(id+"F6.wireOp",VERTEX,"E68.4.0");
            var Q3;
            Q3=sQuery(id+"F6.wireOp",VERTEX,"E68.3.0");
            var Q4;
            Q4=sQuery(id+"F6.wireOp",VERTEX,"E68.2.0");
            var Q5;
            Q5=sQuery(id+"F6.wireOp",VERTEX,"E68.1.0");
            var Q6;
            Q6=makeQuery(id+"F1.opExtrude","SWEPT_BODY",BODY,{"disambiguationData":[OSD([sQuery(id+"F0.wireOp",EDGE,"E0"),sQuery(id+"F0.wireOp",EDGE,"E1.trimOffspring"),sQuery(id+"F0.wireOp",EDGE,"E2"),sQuery(id+"F0.wireOp",EDGE,"E3"),sQuery(id+"F0.wireOp",EDGE,"E4.MirrorCS"),sQuery(id+"F0.wireOp",EDGE,"E5.MirrorCS"),sQuery(id+"F0.wireOp",EDGE,"E6.MirrorCS"),sQuery(id+"F0.wireOp",EDGE,"E7.filletArc"),sQuery(id+"F0.wireOp",EDGE,"E8.filletArc"),sQuery(id+"F0.wireOp",EDGE,"E9.filletArc"),sQuery(id+"F0.wireOp",EDGE,"E10.filletArc"),sQuery(id+"F0.wireOp",EDGE,"E11.1.0"),sQuery(id+"F0.wireOp",EDGE,"E11.1.1"),sQuery(id+"F0.wireOp",EDGE,"E11.1.2"),sQuery(id+"F0.wireOp",EDGE,"E11.1.3"),sQuery(id+"F0.wireOp",EDGE,"E11.1.4"),sQuery(id+"F0.wireOp",EDGE,"E11.1.5"),sQuery(id+"F0.wireOp",EDGE,"E11.1.6"),sQuery(id+"F0.wireOp",EDGE,"E11.1.7"),sQuery(id+"F0.wireOp",EDGE,"E11.1.8"),sQuery(id+"F0.wireOp",EDGE,"E11.1.9"),sQuery(id+"F0.wireOp",EDGE,"E11.2.0"),sQuery(id+"F0.wireOp",EDGE,"E11.2.1"),sQuery(id+"F0.wireOp",EDGE,"E11.2.2"),sQuery(id+"F0.wireOp",EDGE,"E11.2.3"),sQuery(id+"F0.wireOp",EDGE,"E11.2.4"),sQuery(id+"F0.wireOp",EDGE,"E11.2.5"),sQuery(id+"F0.wireOp",EDGE,"E11.2.6"),sQuery(id+"F0.wireOp",EDGE,"E11.2.7"),sQuery(id+"F0.wireOp",EDGE,"E11.2.8"),sQuery(id+"F0.wireOp",EDGE,"E11.2.9"),sQuery(id+"F0.wireOp",EDGE,"E12.2.3.0"),sQuery(id+"F0.wireOp",EDGE,"E12.4.3.0"),sQuery(id+"F0.wireOp",EDGE,"E12.7.3.0"),sQuery(id+"F0.wireOp",EDGE,"E12.11.3.0"),sQuery(id+"F0.wireOp",EDGE,"E12.15.3.0"),sQuery(id+"F0.wireOp",EDGE,"E12.18.3.0"),sQuery(id+"F0.wireOp",EDGE,"E12.21.3.0"),sQuery(id+"F0.wireOp",EDGE,"E12.25.3.0"),sQuery(id+"F0.wireOp",EDGE,"E12.29.3.0"),sQuery(id+"F0.wireOp",EDGE,"E12.32.3.0"),sQuery(id+"F0.wireOp",EDGE,"E12.2.4.0"),sQuery(id+"F0.wireOp",EDGE,"E12.4.4.0"),sQuery(id+"F0.wireOp",EDGE,"E12.7.4.0"),sQuery(id+"F0.wireOp",EDGE,"E12.11.4.0"),sQuery(id+"F0.wireOp",EDGE,"E12.15.4.0"),sQuery(id+"F0.wireOp",EDGE,"E12.18.4.0"),sQuery(id+"F0.wireOp",EDGE,"E12.21.4.0"),sQuery(id+"F0.wireOp",EDGE,"E12.25.4.0"),sQuery(id+"F0.wireOp",EDGE,"E12.29.4.0"),sQuery(id+"F0.wireOp",EDGE,"E12.32.4.0"),sQuery(id+"F0.wireOp",EDGE,"E12.2.5.0"),sQuery(id+"F0.wireOp",EDGE,"E12.4.5.0"),sQuery(id+"F0.wireOp",EDGE,"E12.7.5.0"),sQuery(id+"F0.wireOp",EDGE,"E12.11.5.0"),sQuery(id+"F0.wireOp",EDGE,"E12.15.5.0"),sQuery(id+"F0.wireOp",EDGE,"E12.18.5.0"),sQuery(id+"F0.wireOp",EDGE,"E12.21.5.0"),sQuery(id+"F0.wireOp",EDGE,"E12.25.5.0"),sQuery(id+"F0.wireOp",EDGE,"E12.29.5.0"),sQuery(id+"F0.wireOp",EDGE,"E12.32.5.0"),sQuery(id+"F0.wireOp",EDGE,"E12.2.6.0"),sQuery(id+"F0.wireOp",EDGE,"E12.4.6.0"),sQuery(id+"F0.wireOp",EDGE,"E12.7.6.0"),sQuery(id+"F0.wireOp",EDGE,"E12.11.6.0"),sQuery(id+"F0.wireOp",EDGE,"E12.15.6.0"),sQuery(id+"F0.wireOp",EDGE,"E12.18.6.0"),sQuery(id+"F0.wireOp",EDGE,"E12.21.6.0"),sQuery(id+"F0.wireOp",EDGE,"E12.25.6.0"),sQuery(id+"F0.wireOp",EDGE,"E12.29.6.0"),sQuery(id+"F0.wireOp",EDGE,"E12.32.6.0"),sQuery(id+"F0.wireOp",EDGE,"E12.2.7.0"),sQuery(id+"F0.wireOp",EDGE,"E12.4.7.0"),sQuery(id+"F0.wireOp",EDGE,"E12.7.7.0"),sQuery(id+"F0.wireOp",EDGE,"E12.11.7.0"),sQuery(id+"F0.wireOp",EDGE,"E12.15.7.0"),sQuery(id+"F0.wireOp",EDGE,"E12.18.7.0"),sQuery(id+"F0.wireOp",EDGE,"E12.21.7.0"),sQuery(id+"F0.wireOp",EDGE,"E12.25.7.0"),sQuery(id+"F0.wireOp",EDGE,"E12.29.7.0"),sQuery(id+"F0.wireOp",EDGE,"E12.32.7.0"),sQuery(id+"F0.wireOp",EDGE,"E12.2.8.0"),sQuery(id+"F0.wireOp",EDGE,"E12.4.8.0"),sQuery(id+"F0.wireOp",EDGE,"E12.7.8.0"),sQuery(id+"F0.wireOp",EDGE,"E12.11.8.0"),sQuery(id+"F0.wireOp",EDGE,"E12.15.8.0"),sQuery(id+"F0.wireOp",EDGE,"E12.18.8.0"),sQuery(id+"F0.wireOp",EDGE,"E12.21.8.0"),sQuery(id+"F0.wireOp",EDGE,"E12.25.8.0"),sQuery(id+"F0.wireOp",EDGE,"E12.29.8.0"),sQuery(id+"F0.wireOp",EDGE,"E12.32.8.0"),sQuery(id+"F0.wireOp",EDGE,"E12.2.9.0"),sQuery(id+"F0.wireOp",EDGE,"E12.4.9.0"),sQuery(id+"F0.wireOp",EDGE,"E12.7.9.0"),sQuery(id+"F0.wireOp",EDGE,"E12.11.9.0"),sQuery(id+"F0.wireOp",EDGE,"E12.15.9.0"),sQuery(id+"F0.wireOp",EDGE,"E12.18.9.0"),sQuery(id+"F0.wireOp",EDGE,"E12.21.9.0"),sQuery(id+"F0.wireOp",EDGE,"E12.25.9.0"),sQuery(id+"F0.wireOp",EDGE,"E12.29.9.0"),sQuery(id+"F0.wireOp",EDGE,"E12.32.9.0"),sQuery(id+"F0.wireOp",EDGE,"E12.2.10.0"),sQuery(id+"F0.wireOp",EDGE,"E12.4.10.0"),sQuery(id+"F0.wireOp",EDGE,"E12.7.10.0"),sQuery(id+"F0.wireOp",EDGE,"E12.11.10.0"),sQuery(id+"F0.wireOp",EDGE,"E12.15.10.0"),sQuery(id+"F0.wireOp",EDGE,"E12.18.10.0"),sQuery(id+"F0.wireOp",EDGE,"E12.21.10.0"),sQuery(id+"F0.wireOp",EDGE,"E12.25.10.0"),sQuery(id+"F0.wireOp",EDGE,"E12.29.10.0"),sQuery(id+"F0.wireOp",EDGE,"E12.32.10.0"),sQuery(id+"F0.wireOp",EDGE,"E12.2.11.0"),sQuery(id+"F0.wireOp",EDGE,"E12.4.11.0"),sQuery(id+"F0.wireOp",EDGE,"E12.7.11.0"),sQuery(id+"F0.wireOp",EDGE,"E12.11.11.0"),sQuery(id+"F0.wireOp",EDGE,"E12.15.11.0"),sQuery(id+"F0.wireOp",EDGE,"E12.18.11.0"),sQuery(id+"F0.wireOp",EDGE,"E12.21.11.0"),sQuery(id+"F0.wireOp",EDGE,"E12.25.11.0"),sQuery(id+"F0.wireOp",EDGE,"E12.29.11.0"),sQuery(id+"F0.wireOp",EDGE,"E12.32.11.0"),sQuery(id+"F0.wireOp",EDGE,"E12.2.12.0"),sQuery(id+"F0.wireOp",EDGE,"E12.4.12.0"),sQuery(id+"F0.wireOp",EDGE,"E12.7.12.0"),sQuery(id+"F0.wireOp",EDGE,"E12.11.12.0"),sQuery(id+"F0.wireOp",EDGE,"E12.15.12.0"),sQuery(id+"F0.wireOp",EDGE,"E12.18.12.0"),sQuery(id+"F0.wireOp",EDGE,"E12.21.12.0"),sQuery(id+"F0.wireOp",EDGE,"E12.25.12.0"),sQuery(id+"F0.wireOp",EDGE,"E12.29.12.0"),sQuery(id+"F0.wireOp",EDGE,"E12.32.12.0"),sQuery(id+"F0.wireOp",EDGE,"E12.2.13.0"),sQuery(id+"F0.wireOp",EDGE,"E12.4.13.0"),sQuery(id+"F0.wireOp",EDGE,"E12.7.13.0"),sQuery(id+"F0.wireOp",EDGE,"E12.11.13.0"),sQuery(id+"F0.wireOp",EDGE,"E12.15.13.0"),sQuery(id+"F0.wireOp",EDGE,"E12.18.13.0"),sQuery(id+"F0.wireOp",EDGE,"E12.21.13.0"),sQuery(id+"F0.wireOp",EDGE,"E12.25.13.0"),sQuery(id+"F0.wireOp",EDGE,"E12.29.13.0"),sQuery(id+"F0.wireOp",EDGE,"E12.32.13.0"),sQuery(id+"F0.wireOp",EDGE,"E12.2.14.0"),sQuery(id+"F0.wireOp",EDGE,"E12.4.14.0"),sQuery(id+"F0.wireOp",EDGE,"E12.7.14.0"),sQuery(id+"F0.wireOp",EDGE,"E12.11.14.0"),sQuery(id+"F0.wireOp",EDGE,"E12.15.14.0"),sQuery(id+"F0.wireOp",EDGE,"E12.18.14.0"),sQuery(id+"F0.wireOp",EDGE,"E12.21.14.0"),sQuery(id+"F0.wireOp",EDGE,"E12.25.14.0"),sQuery(id+"F0.wireOp",EDGE,"E12.29.14.0"),sQuery(id+"F0.wireOp",EDGE,"E12.32.14.0"),sQuery(id+"F0.wireOp",EDGE,"E12.2.15.0"),sQuery(id+"F0.wireOp",EDGE,"E12.4.15.0"),sQuery(id+"F0.wireOp",EDGE,"E12.7.15.0"),sQuery(id+"F0.wireOp",EDGE,"E12.11.15.0"),sQuery(id+"F0.wireOp",EDGE,"E12.15.15.0"),sQuery(id+"F0.wireOp",EDGE,"E12.18.15.0"),sQuery(id+"F0.wireOp",EDGE,"E12.21.15.0"),sQuery(id+"F0.wireOp",EDGE,"E12.25.15.0"),sQuery(id+"F0.wireOp",EDGE,"E12.29.15.0"),sQuery(id+"F0.wireOp",EDGE,"E12.32.15.0"),sQuery(id+"F0.wireOp",EDGE,"E12.2.16.0"),sQuery(id+"F0.wireOp",EDGE,"E12.4.16.0"),sQuery(id+"F0.wireOp",EDGE,"E12.7.16.0"),sQuery(id+"F0.wireOp",EDGE,"E12.11.16.0"),sQuery(id+"F0.wireOp",EDGE,"E12.15.16.0"),sQuery(id+"F0.wireOp",EDGE,"E12.18.16.0"),sQuery(id+"F0.wireOp",EDGE,"E12.21.16.0"),sQuery(id+"F0.wireOp",EDGE,"E12.25.16.0"),sQuery(id+"F0.wireOp",EDGE,"E12.29.16.0"),sQuery(id+"F0.wireOp",EDGE,"E12.32.16.0"),sQuery(id+"F0.wireOp",EDGE,"E12.2.17.0"),sQuery(id+"F0.wireOp",EDGE,"E12.4.17.0"),sQuery(id+"F0.wireOp",EDGE,"E12.7.17.0"),sQuery(id+"F0.wireOp",EDGE,"E12.11.17.0"),sQuery(id+"F0.wireOp",EDGE,"E12.15.17.0"),sQuery(id+"F0.wireOp",EDGE,"E12.18.17.0"),sQuery(id+"F0.wireOp",EDGE,"E12.21.17.0"),sQuery(id+"F0.wireOp",EDGE,"E12.25.17.0"),sQuery(id+"F0.wireOp",EDGE,"E12.29.17.0"),sQuery(id+"F0.wireOp",EDGE,"E12.32.17.0"),sQuery(id+"F0.wireOp",EDGE,"E12.2.18.0"),sQuery(id+"F0.wireOp",EDGE,"E12.4.18.0"),sQuery(id+"F0.wireOp",EDGE,"E12.7.18.0"),sQuery(id+"F0.wireOp",EDGE,"E12.11.18.0"),sQuery(id+"F0.wireOp",EDGE,"E12.15.18.0"),sQuery(id+"F0.wireOp",EDGE,"E12.18.18.0"),sQuery(id+"F0.wireOp",EDGE,"E12.21.18.0"),sQuery(id+"F0.wireOp",EDGE,"E12.25.18.0"),sQuery(id+"F0.wireOp",EDGE,"E12.29.18.0"),sQuery(id+"F0.wireOp",EDGE,"E12.32.18.0"),sQuery(id+"F0.wireOp",EDGE,"E12.2.19.0"),sQuery(id+"F0.wireOp",EDGE,"E12.4.19.0"),sQuery(id+"F0.wireOp",EDGE,"E12.7.19.0"),sQuery(id+"F0.wireOp",EDGE,"E12.11.19.0"),sQuery(id+"F0.wireOp",EDGE,"E12.15.19.0"),sQuery(id+"F0.wireOp",EDGE,"E12.18.19.0"),sQuery(id+"F0.wireOp",EDGE,"E12.21.19.0"),sQuery(id+"F0.wireOp",EDGE,"E12.25.19.0"),sQuery(id+"F0.wireOp",EDGE,"E12.29.19.0"),sQuery(id+"F0.wireOp",EDGE,"E12.32.19.0"),sQuery(id+"F0.wireOp",EDGE,"E12.2.20.0"),sQuery(id+"F0.wireOp",EDGE,"E12.4.20.0"),sQuery(id+"F0.wireOp",EDGE,"E12.7.20.0"),sQuery(id+"F0.wireOp",EDGE,"E12.11.20.0"),sQuery(id+"F0.wireOp",EDGE,"E12.15.20.0"),sQuery(id+"F0.wireOp",EDGE,"E12.18.20.0"),sQuery(id+"F0.wireOp",EDGE,"E12.21.20.0"),sQuery(id+"F0.wireOp",EDGE,"E12.25.20.0"),sQuery(id+"F0.wireOp",EDGE,"E12.29.20.0"),sQuery(id+"F0.wireOp",EDGE,"E12.32.20.0"),sQuery(id+"F0.wireOp",EDGE,"E12.2.21.0"),sQuery(id+"F0.wireOp",EDGE,"E12.4.21.0"),sQuery(id+"F0.wireOp",EDGE,"E12.7.21.0"),sQuery(id+"F0.wireOp",EDGE,"E12.11.21.0"),sQuery(id+"F0.wireOp",EDGE,"E12.15.21.0"),sQuery(id+"F0.wireOp",EDGE,"E12.18.21.0"),sQuery(id+"F0.wireOp",EDGE,"E12.21.21.0"),sQuery(id+"F0.wireOp",EDGE,"E12.25.21.0"),sQuery(id+"F0.wireOp",EDGE,"E12.29.21.0"),sQuery(id+"F0.wireOp",EDGE,"E12.32.21.0"),sQuery(id+"F0.wireOp",EDGE,"E12.2.22.0"),sQuery(id+"F0.wireOp",EDGE,"E12.4.22.0"),sQuery(id+"F0.wireOp",EDGE,"E12.7.22.0"),sQuery(id+"F0.wireOp",EDGE,"E12.11.22.0"),sQuery(id+"F0.wireOp",EDGE,"E12.15.22.0"),sQuery(id+"F0.wireOp",EDGE,"E12.18.22.0"),sQuery(id+"F0.wireOp",EDGE,"E12.21.22.0"),sQuery(id+"F0.wireOp",EDGE,"E12.25.22.0"),sQuery(id+"F0.wireOp",EDGE,"E12.29.22.0"),sQuery(id+"F0.wireOp",EDGE,"E12.32.22.0"),sQuery(id+"F0.wireOp",EDGE,"E12.2.23.0"),sQuery(id+"F0.wireOp",EDGE,"E12.4.23.0"),sQuery(id+"F0.wireOp",EDGE,"E12.7.23.0"),sQuery(id+"F0.wireOp",EDGE,"E12.11.23.0"),sQuery(id+"F0.wireOp",EDGE,"E12.15.23.0"),sQuery(id+"F0.wireOp",EDGE,"E12.18.23.0"),sQuery(id+"F0.wireOp",EDGE,"E12.21.23.0"),sQuery(id+"F0.wireOp",EDGE,"E12.25.23.0"),sQuery(id+"F0.wireOp",EDGE,"E12.29.23.0"),sQuery(id+"F0.wireOp",EDGE,"E12.32.23.0"),sQuery(id+"F0.wireOp",EDGE,"E12.2.24.0"),sQuery(id+"F0.wireOp",EDGE,"E12.4.24.0"),sQuery(id+"F0.wireOp",EDGE,"E12.7.24.0"),sQuery(id+"F0.wireOp",EDGE,"E12.11.24.0"),sQuery(id+"F0.wireOp",EDGE,"E12.15.24.0"),sQuery(id+"F0.wireOp",EDGE,"E12.18.24.0"),sQuery(id+"F0.wireOp",EDGE,"E12.21.24.0"),sQuery(id+"F0.wireOp",EDGE,"E12.25.24.0"),sQuery(id+"F0.wireOp",EDGE,"E12.29.24.0"),sQuery(id+"F0.wireOp",EDGE,"E12.32.24.0"),sQuery(id+"F0.wireOp",EDGE,"E12.2.25.0"),sQuery(id+"F0.wireOp",EDGE,"E12.4.25.0"),sQuery(id+"F0.wireOp",EDGE,"E12.7.25.0"),sQuery(id+"F0.wireOp",EDGE,"E12.11.25.0"),sQuery(id+"F0.wireOp",EDGE,"E12.15.25.0"),sQuery(id+"F0.wireOp",EDGE,"E12.18.25.0"),sQuery(id+"F0.wireOp",EDGE,"E12.21.25.0"),sQuery(id+"F0.wireOp",EDGE,"E12.25.25.0"),sQuery(id+"F0.wireOp",EDGE,"E12.29.25.0"),sQuery(id+"F0.wireOp",EDGE,"E12.32.25.0"),sQuery(id+"F0.wireOp",EDGE,"E12.2.26.0"),sQuery(id+"F0.wireOp",EDGE,"E12.4.26.0"),sQuery(id+"F0.wireOp",EDGE,"E12.7.26.0"),sQuery(id+"F0.wireOp",EDGE,"E12.11.26.0"),sQuery(id+"F0.wireOp",EDGE,"E12.15.26.0"),sQuery(id+"F0.wireOp",EDGE,"E12.18.26.0"),sQuery(id+"F0.wireOp",EDGE,"E12.21.26.0"),sQuery(id+"F0.wireOp",EDGE,"E12.25.26.0"),sQuery(id+"F0.wireOp",EDGE,"E12.29.26.0"),sQuery(id+"F0.wireOp",EDGE,"E12.32.26.0"),sQuery(id+"F0.wireOp",EDGE,"E12.2.27.0"),sQuery(id+"F0.wireOp",EDGE,"E12.4.27.0"),sQuery(id+"F0.wireOp",EDGE,"E12.7.27.0"),sQuery(id+"F0.wireOp",EDGE,"E12.11.27.0"),sQuery(id+"F0.wireOp",EDGE,"E12.15.27.0"),sQuery(id+"F0.wireOp",EDGE,"E12.18.27.0"),sQuery(id+"F0.wireOp",EDGE,"E12.21.27.0"),sQuery(id+"F0.wireOp",EDGE,"E12.25.27.0"),sQuery(id+"F0.wireOp",EDGE,"E12.29.27.0"),sQuery(id+"F0.wireOp",EDGE,"E12.32.27.0"),sQuery(id+"F0.wireOp",EDGE,"E12.2.28.0"),sQuery(id+"F0.wireOp",EDGE,"E12.4.28.0"),sQuery(id+"F0.wireOp",EDGE,"E12.7.28.0"),sQuery(id+"F0.wireOp",EDGE,"E12.11.28.0"),sQuery(id+"F0.wireOp",EDGE,"E12.15.28.0"),sQuery(id+"F0.wireOp",EDGE,"E12.18.28.0"),sQuery(id+"F0.wireOp",EDGE,"E12.21.28.0"),sQuery(id+"F0.wireOp",EDGE,"E12.25.28.0"),sQuery(id+"F0.wireOp",EDGE,"E12.29.28.0"),sQuery(id+"F0.wireOp",EDGE,"E12.32.28.0"),sQuery(id+"F0.wireOp",EDGE,"E12.2.29.0"),sQuery(id+"F0.wireOp",EDGE,"E12.4.29.0"),sQuery(id+"F0.wireOp",EDGE,"E12.7.29.0"),sQuery(id+"F0.wireOp",EDGE,"E12.11.29.0"),sQuery(id+"F0.wireOp",EDGE,"E12.15.29.0"),sQuery(id+"F0.wireOp",EDGE,"E12.18.29.0"),sQuery(id+"F0.wireOp",EDGE,"E12.21.29.0"),sQuery(id+"F0.wireOp",EDGE,"E12.25.29.0"),sQuery(id+"F0.wireOp",EDGE,"E12.29.29.0"),sQuery(id+"F0.wireOp",EDGE,"E12.32.29.0"),sQuery(id+"F0.wireOp",EDGE,"E12.2.30.0"),sQuery(id+"F0.wireOp",EDGE,"E12.4.30.0"),sQuery(id+"F0.wireOp",EDGE,"E12.7.30.0"),sQuery(id+"F0.wireOp",EDGE,"E12.11.30.0"),sQuery(id+"F0.wireOp",EDGE,"E12.15.30.0"),sQuery(id+"F0.wireOp",EDGE,"E12.18.30.0"),sQuery(id+"F0.wireOp",EDGE,"E12.21.30.0"),sQuery(id+"F0.wireOp",EDGE,"E12.25.30.0"),sQuery(id+"F0.wireOp",EDGE,"E12.29.30.0"),sQuery(id+"F0.wireOp",EDGE,"E12.32.30.0"),sQuery(id+"F0.wireOp",EDGE,"E12.2.31.0"),sQuery(id+"F0.wireOp",EDGE,"E12.4.31.0"),sQuery(id+"F0.wireOp",EDGE,"E12.7.31.0"),sQuery(id+"F0.wireOp",EDGE,"E12.11.31.0"),sQuery(id+"F0.wireOp",EDGE,"E12.15.31.0"),sQuery(id+"F0.wireOp",EDGE,"E12.18.31.0"),sQuery(id+"F0.wireOp",EDGE,"E12.21.31.0"),sQuery(id+"F0.wireOp",EDGE,"E12.25.31.0"),sQuery(id+"F0.wireOp",EDGE,"E12.29.31.0"),sQuery(id+"F0.wireOp",EDGE,"E12.32.31.0"),sQuery(id+"F0.wireOp",EDGE,"E12.2.32.0"),sQuery(id+"F0.wireOp",EDGE,"E12.4.32.0"),sQuery(id+"F0.wireOp",EDGE,"E12.7.32.0"),sQuery(id+"F0.wireOp",EDGE,"E12.11.32.0"),sQuery(id+"F0.wireOp",EDGE,"E12.15.32.0"),sQuery(id+"F0.wireOp",EDGE,"E12.18.32.0"),sQuery(id+"F0.wireOp",EDGE,"E12.21.32.0"),sQuery(id+"F0.wireOp",EDGE,"E12.25.32.0"),sQuery(id+"F0.wireOp",EDGE,"E12.29.32.0"),sQuery(id+"F0.wireOp",EDGE,"E12.32.32.0"),sQuery(id+"F0.wireOp",EDGE,"E12.2.33.0"),sQuery(id+"F0.wireOp",EDGE,"E12.4.33.0"),sQuery(id+"F0.wireOp",EDGE,"E12.7.33.0"),sQuery(id+"F0.wireOp",EDGE,"E12.11.33.0"),sQuery(id+"F0.wireOp",EDGE,"E12.15.33.0"),sQuery(id+"F0.wireOp",EDGE,"E12.18.33.0"),sQuery(id+"F0.wireOp",EDGE,"E12.21.33.0"),sQuery(id+"F0.wireOp",EDGE,"E12.25.33.0"),sQuery(id+"F0.wireOp",EDGE,"E12.29.33.0"),sQuery(id+"F0.wireOp",EDGE,"E12.32.33.0"),sQuery(id+"F0.wireOp",EDGE,"E12.2.34.0"),sQuery(id+"F0.wireOp",EDGE,"E12.4.34.0"),sQuery(id+"F0.wireOp",EDGE,"E12.7.34.0"),sQuery(id+"F0.wireOp",EDGE,"E12.11.34.0"),sQuery(id+"F0.wireOp",EDGE,"E12.15.34.0"),sQuery(id+"F0.wireOp",EDGE,"E12.18.34.0"),sQuery(id+"F0.wireOp",EDGE,"E12.21.34.0"),sQuery(id+"F0.wireOp",EDGE,"E12.25.34.0"),sQuery(id+"F0.wireOp",EDGE,"E12.29.34.0"),sQuery(id+"F0.wireOp",EDGE,"E12.32.34.0"),sQuery(id+"F0.wireOp",EDGE,"E12.2.35.0"),sQuery(id+"F0.wireOp",EDGE,"E12.4.35.0"),sQuery(id+"F0.wireOp",EDGE,"E12.7.35.0"),sQuery(id+"F0.wireOp",EDGE,"E12.11.35.0"),sQuery(id+"F0.wireOp",EDGE,"E12.15.35.0"),sQuery(id+"F0.wireOp",EDGE,"E12.18.35.0"),sQuery(id+"F0.wireOp",EDGE,"E12.21.35.0"),sQuery(id+"F0.wireOp",EDGE,"E12.25.35.0"),sQuery(id+"F0.wireOp",EDGE,"E12.29.35.0"),sQuery(id+"F0.wireOp",EDGE,"E12.32.35.0"),sQuery(id+"F0.wireOp",EDGE,"E13.trimOffspring"),sQuery(id+"F0.wireOp",EDGE,"E14.trimOffspring"),sQuery(id+"F0.wireOp",EDGE,"E15.trimOffspring"),sQuery(id+"F0.wireOp",EDGE,"E16.trimOffspring"),sQuery(id+"F0.wireOp",EDGE,"E17.trimOffspring"),sQuery(id+"F0.wireOp",EDGE,"E18.trimOffspring"),sQuery(id+"F0.wireOp",EDGE,"E19.trimOffspring"),sQuery(id+"F0.wireOp",EDGE,"E20.trimOffspring"),sQuery(id+"F0.wireOp",EDGE,"E21.trimOffspring"),sQuery(id+"F0.wireOp",EDGE,"E22.trimOffspring"),sQuery(id+"F0.wireOp",EDGE,"E23.trimOffspring"),sQuery(id+"F0.wireOp",EDGE,"E24.trimOffspring"),sQuery(id+"F0.wireOp",EDGE,"E25.trimOffspring"),sQuery(id+"F0.wireOp",EDGE,"E26.trimOffspring"),sQuery(id+"F0.wireOp",EDGE,"E27.trimOffspring"),sQuery(id+"F0.wireOp",EDGE,"E28.trimOffspring"),sQuery(id+"F0.wireOp",EDGE,"E29.trimOffspring"),sQuery(id+"F0.wireOp",EDGE,"E30.trimOffspring"),sQuery(id+"F0.wireOp",EDGE,"E31.trimOffspring"),sQuery(id+"F0.wireOp",EDGE,"E32.trimOffspring"),sQuery(id+"F0.wireOp",EDGE,"E33.trimOffspring"),sQuery(id+"F0.wireOp",EDGE,"E34.trimOffspring"),sQuery(id+"F0.wireOp",EDGE,"E35.trimOffspring"),sQuery(id+"F0.wireOp",EDGE,"E36.trimOffspring"),sQuery(id+"F0.wireOp",EDGE,"E37.trimOffspring"),sQuery(id+"F0.wireOp",EDGE,"E38.trimOffspring"),sQuery(id+"F0.wireOp",EDGE,"E39.trimOffspring"),sQuery(id+"F0.wireOp",EDGE,"E40.trimOffspring"),sQuery(id+"F0.wireOp",EDGE,"E41.trimOffspring"),sQuery(id+"F0.wireOp",EDGE,"E42.trimOffspring"),sQuery(id+"F0.wireOp",EDGE,"E43.trimOffspring"),sQuery(id+"F0.wireOp",EDGE,"E44.trimOffspring"),sQuery(id+"F0.wireOp",EDGE,"E45.trimOffspring"),sQuery(id+"F0.wireOp",EDGE,"E46.trimOffspring"),sQuery(id+"F0.wireOp",EDGE,"E47.trimOffspring")])]});
            hole(context, id + "F7", {"style" : HoleStyle.C_BORE, "endStyle" : HoleEndStyle.THROUGH, "holeDiameter" : 3.17 * mm, "cBoreDiameter" : 4.44 * mm, "cBoreDepth" : 3.17 * mm, "locations" : qUnion([Q0, Q1, Q2, Q3, Q4, Q5]), "scope" : qUnion([Q6]), "isTappedThrough" : true});
        }
        {
            var Q0;
            Q0=sQuery(id+"F6.wireOp",VERTEX,"E68.center");
            var Q1;
            Q1=makeQuery(id+"F1.opExtrude","SWEPT_BODY",BODY,{"disambiguationData":[OSD([sQuery(id+"F0.wireOp",EDGE,"E0"),sQuery(id+"F0.wireOp",EDGE,"E1.trimOffspring"),sQuery(id+"F0.wireOp",EDGE,"E2"),sQuery(id+"F0.wireOp",EDGE,"E3"),sQuery(id+"F0.wireOp",EDGE,"E4.MirrorCS"),sQuery(id+"F0.wireOp",EDGE,"E5.MirrorCS"),sQuery(id+"F0.wireOp",EDGE,"E6.MirrorCS"),sQuery(id+"F0.wireOp",EDGE,"E7.filletArc"),sQuery(id+"F0.wireOp",EDGE,"E8.filletArc"),sQuery(id+"F0.wireOp",EDGE,"E9.filletArc"),sQuery(id+"F0.wireOp",EDGE,"E10.filletArc"),sQuery(id+"F0.wireOp",EDGE,"E11.1.0"),sQuery(id+"F0.wireOp",EDGE,"E11.1.1"),sQuery(id+"F0.wireOp",EDGE,"E11.1.2"),sQuery(id+"F0.wireOp",EDGE,"E11.1.3"),sQuery(id+"F0.wireOp",EDGE,"E11.1.4"),sQuery(id+"F0.wireOp",EDGE,"E11.1.5"),sQuery(id+"F0.wireOp",EDGE,"E11.1.6"),sQuery(id+"F0.wireOp",EDGE,"E11.1.7"),sQuery(id+"F0.wireOp",EDGE,"E11.1.8"),sQuery(id+"F0.wireOp",EDGE,"E11.1.9"),sQuery(id+"F0.wireOp",EDGE,"E11.2.0"),sQuery(id+"F0.wireOp",EDGE,"E11.2.1"),sQuery(id+"F0.wireOp",EDGE,"E11.2.2"),sQuery(id+"F0.wireOp",EDGE,"E11.2.3"),sQuery(id+"F0.wireOp",EDGE,"E11.2.4"),sQuery(id+"F0.wireOp",EDGE,"E11.2.5"),sQuery(id+"F0.wireOp",EDGE,"E11.2.6"),sQuery(id+"F0.wireOp",EDGE,"E11.2.7"),sQuery(id+"F0.wireOp",EDGE,"E11.2.8"),sQuery(id+"F0.wireOp",EDGE,"E11.2.9"),sQuery(id+"F0.wireOp",EDGE,"E12.2.3.0"),sQuery(id+"F0.wireOp",EDGE,"E12.4.3.0"),sQuery(id+"F0.wireOp",EDGE,"E12.7.3.0"),sQuery(id+"F0.wireOp",EDGE,"E12.11.3.0"),sQuery(id+"F0.wireOp",EDGE,"E12.15.3.0"),sQuery(id+"F0.wireOp",EDGE,"E12.18.3.0"),sQuery(id+"F0.wireOp",EDGE,"E12.21.3.0"),sQuery(id+"F0.wireOp",EDGE,"E12.25.3.0"),sQuery(id+"F0.wireOp",EDGE,"E12.29.3.0"),sQuery(id+"F0.wireOp",EDGE,"E12.32.3.0"),sQuery(id+"F0.wireOp",EDGE,"E12.2.4.0"),sQuery(id+"F0.wireOp",EDGE,"E12.4.4.0"),sQuery(id+"F0.wireOp",EDGE,"E12.7.4.0"),sQuery(id+"F0.wireOp",EDGE,"E12.11.4.0"),sQuery(id+"F0.wireOp",EDGE,"E12.15.4.0"),sQuery(id+"F0.wireOp",EDGE,"E12.18.4.0"),sQuery(id+"F0.wireOp",EDGE,"E12.21.4.0"),sQuery(id+"F0.wireOp",EDGE,"E12.25.4.0"),sQuery(id+"F0.wireOp",EDGE,"E12.29.4.0"),sQuery(id+"F0.wireOp",EDGE,"E12.32.4.0"),sQuery(id+"F0.wireOp",EDGE,"E12.2.5.0"),sQuery(id+"F0.wireOp",EDGE,"E12.4.5.0"),sQuery(id+"F0.wireOp",EDGE,"E12.7.5.0"),sQuery(id+"F0.wireOp",EDGE,"E12.11.5.0"),sQuery(id+"F0.wireOp",EDGE,"E12.15.5.0"),sQuery(id+"F0.wireOp",EDGE,"E12.18.5.0"),sQuery(id+"F0.wireOp",EDGE,"E12.21.5.0"),sQuery(id+"F0.wireOp",EDGE,"E12.25.5.0"),sQuery(id+"F0.wireOp",EDGE,"E12.29.5.0"),sQuery(id+"F0.wireOp",EDGE,"E12.32.5.0"),sQuery(id+"F0.wireOp",EDGE,"E12.2.6.0"),sQuery(id+"F0.wireOp",EDGE,"E12.4.6.0"),sQuery(id+"F0.wireOp",EDGE,"E12.7.6.0"),sQuery(id+"F0.wireOp",EDGE,"E12.11.6.0"),sQuery(id+"F0.wireOp",EDGE,"E12.15.6.0"),sQuery(id+"F0.wireOp",EDGE,"E12.18.6.0"),sQuery(id+"F0.wireOp",EDGE,"E12.21.6.0"),sQuery(id+"F0.wireOp",EDGE,"E12.25.6.0"),sQuery(id+"F0.wireOp",EDGE,"E12.29.6.0"),sQuery(id+"F0.wireOp",EDGE,"E12.32.6.0"),sQuery(id+"F0.wireOp",EDGE,"E12.2.7.0"),sQuery(id+"F0.wireOp",EDGE,"E12.4.7.0"),sQuery(id+"F0.wireOp",EDGE,"E12.7.7.0"),sQuery(id+"F0.wireOp",EDGE,"E12.11.7.0"),sQuery(id+"F0.wireOp",EDGE,"E12.15.7.0"),sQuery(id+"F0.wireOp",EDGE,"E12.18.7.0"),sQuery(id+"F0.wireOp",EDGE,"E12.21.7.0"),sQuery(id+"F0.wireOp",EDGE,"E12.25.7.0"),sQuery(id+"F0.wireOp",EDGE,"E12.29.7.0"),sQuery(id+"F0.wireOp",EDGE,"E12.32.7.0"),sQuery(id+"F0.wireOp",EDGE,"E12.2.8.0"),sQuery(id+"F0.wireOp",EDGE,"E12.4.8.0"),sQuery(id+"F0.wireOp",EDGE,"E12.7.8.0"),sQuery(id+"F0.wireOp",EDGE,"E12.11.8.0"),sQuery(id+"F0.wireOp",EDGE,"E12.15.8.0"),sQuery(id+"F0.wireOp",EDGE,"E12.18.8.0"),sQuery(id+"F0.wireOp",EDGE,"E12.21.8.0"),sQuery(id+"F0.wireOp",EDGE,"E12.25.8.0"),sQuery(id+"F0.wireOp",EDGE,"E12.29.8.0"),sQuery(id+"F0.wireOp",EDGE,"E12.32.8.0"),sQuery(id+"F0.wireOp",EDGE,"E12.2.9.0"),sQuery(id+"F0.wireOp",EDGE,"E12.4.9.0"),sQuery(id+"F0.wireOp",EDGE,"E12.7.9.0"),sQuery(id+"F0.wireOp",EDGE,"E12.11.9.0"),sQuery(id+"F0.wireOp",EDGE,"E12.15.9.0"),sQuery(id+"F0.wireOp",EDGE,"E12.18.9.0"),sQuery(id+"F0.wireOp",EDGE,"E12.21.9.0"),sQuery(id+"F0.wireOp",EDGE,"E12.25.9.0"),sQuery(id+"F0.wireOp",EDGE,"E12.29.9.0"),sQuery(id+"F0.wireOp",EDGE,"E12.32.9.0"),sQuery(id+"F0.wireOp",EDGE,"E12.2.10.0"),sQuery(id+"F0.wireOp",EDGE,"E12.4.10.0"),sQuery(id+"F0.wireOp",EDGE,"E12.7.10.0"),sQuery(id+"F0.wireOp",EDGE,"E12.11.10.0"),sQuery(id+"F0.wireOp",EDGE,"E12.15.10.0"),sQuery(id+"F0.wireOp",EDGE,"E12.18.10.0"),sQuery(id+"F0.wireOp",EDGE,"E12.21.10.0"),sQuery(id+"F0.wireOp",EDGE,"E12.25.10.0"),sQuery(id+"F0.wireOp",EDGE,"E12.29.10.0"),sQuery(id+"F0.wireOp",EDGE,"E12.32.10.0"),sQuery(id+"F0.wireOp",EDGE,"E12.2.11.0"),sQuery(id+"F0.wireOp",EDGE,"E12.4.11.0"),sQuery(id+"F0.wireOp",EDGE,"E12.7.11.0"),sQuery(id+"F0.wireOp",EDGE,"E12.11.11.0"),sQuery(id+"F0.wireOp",EDGE,"E12.15.11.0"),sQuery(id+"F0.wireOp",EDGE,"E12.18.11.0"),sQuery(id+"F0.wireOp",EDGE,"E12.21.11.0"),sQuery(id+"F0.wireOp",EDGE,"E12.25.11.0"),sQuery(id+"F0.wireOp",EDGE,"E12.29.11.0"),sQuery(id+"F0.wireOp",EDGE,"E12.32.11.0"),sQuery(id+"F0.wireOp",EDGE,"E12.2.12.0"),sQuery(id+"F0.wireOp",EDGE,"E12.4.12.0"),sQuery(id+"F0.wireOp",EDGE,"E12.7.12.0"),sQuery(id+"F0.wireOp",EDGE,"E12.11.12.0"),sQuery(id+"F0.wireOp",EDGE,"E12.15.12.0"),sQuery(id+"F0.wireOp",EDGE,"E12.18.12.0"),sQuery(id+"F0.wireOp",EDGE,"E12.21.12.0"),sQuery(id+"F0.wireOp",EDGE,"E12.25.12.0"),sQuery(id+"F0.wireOp",EDGE,"E12.29.12.0"),sQuery(id+"F0.wireOp",EDGE,"E12.32.12.0"),sQuery(id+"F0.wireOp",EDGE,"E12.2.13.0"),sQuery(id+"F0.wireOp",EDGE,"E12.4.13.0"),sQuery(id+"F0.wireOp",EDGE,"E12.7.13.0"),sQuery(id+"F0.wireOp",EDGE,"E12.11.13.0"),sQuery(id+"F0.wireOp",EDGE,"E12.15.13.0"),sQuery(id+"F0.wireOp",EDGE,"E12.18.13.0"),sQuery(id+"F0.wireOp",EDGE,"E12.21.13.0"),sQuery(id+"F0.wireOp",EDGE,"E12.25.13.0"),sQuery(id+"F0.wireOp",EDGE,"E12.29.13.0"),sQuery(id+"F0.wireOp",EDGE,"E12.32.13.0"),sQuery(id+"F0.wireOp",EDGE,"E12.2.14.0"),sQuery(id+"F0.wireOp",EDGE,"E12.4.14.0"),sQuery(id+"F0.wireOp",EDGE,"E12.7.14.0"),sQuery(id+"F0.wireOp",EDGE,"E12.11.14.0"),sQuery(id+"F0.wireOp",EDGE,"E12.15.14.0"),sQuery(id+"F0.wireOp",EDGE,"E12.18.14.0"),sQuery(id+"F0.wireOp",EDGE,"E12.21.14.0"),sQuery(id+"F0.wireOp",EDGE,"E12.25.14.0"),sQuery(id+"F0.wireOp",EDGE,"E12.29.14.0"),sQuery(id+"F0.wireOp",EDGE,"E12.32.14.0"),sQuery(id+"F0.wireOp",EDGE,"E12.2.15.0"),sQuery(id+"F0.wireOp",EDGE,"E12.4.15.0"),sQuery(id+"F0.wireOp",EDGE,"E12.7.15.0"),sQuery(id+"F0.wireOp",EDGE,"E12.11.15.0"),sQuery(id+"F0.wireOp",EDGE,"E12.15.15.0"),sQuery(id+"F0.wireOp",EDGE,"E12.18.15.0"),sQuery(id+"F0.wireOp",EDGE,"E12.21.15.0"),sQuery(id+"F0.wireOp",EDGE,"E12.25.15.0"),sQuery(id+"F0.wireOp",EDGE,"E12.29.15.0"),sQuery(id+"F0.wireOp",EDGE,"E12.32.15.0"),sQuery(id+"F0.wireOp",EDGE,"E12.2.16.0"),sQuery(id+"F0.wireOp",EDGE,"E12.4.16.0"),sQuery(id+"F0.wireOp",EDGE,"E12.7.16.0"),sQuery(id+"F0.wireOp",EDGE,"E12.11.16.0"),sQuery(id+"F0.wireOp",EDGE,"E12.15.16.0"),sQuery(id+"F0.wireOp",EDGE,"E12.18.16.0"),sQuery(id+"F0.wireOp",EDGE,"E12.21.16.0"),sQuery(id+"F0.wireOp",EDGE,"E12.25.16.0"),sQuery(id+"F0.wireOp",EDGE,"E12.29.16.0"),sQuery(id+"F0.wireOp",EDGE,"E12.32.16.0"),sQuery(id+"F0.wireOp",EDGE,"E12.2.17.0"),sQuery(id+"F0.wireOp",EDGE,"E12.4.17.0"),sQuery(id+"F0.wireOp",EDGE,"E12.7.17.0"),sQuery(id+"F0.wireOp",EDGE,"E12.11.17.0"),sQuery(id+"F0.wireOp",EDGE,"E12.15.17.0"),sQuery(id+"F0.wireOp",EDGE,"E12.18.17.0"),sQuery(id+"F0.wireOp",EDGE,"E12.21.17.0"),sQuery(id+"F0.wireOp",EDGE,"E12.25.17.0"),sQuery(id+"F0.wireOp",EDGE,"E12.29.17.0"),sQuery(id+"F0.wireOp",EDGE,"E12.32.17.0"),sQuery(id+"F0.wireOp",EDGE,"E12.2.18.0"),sQuery(id+"F0.wireOp",EDGE,"E12.4.18.0"),sQuery(id+"F0.wireOp",EDGE,"E12.7.18.0"),sQuery(id+"F0.wireOp",EDGE,"E12.11.18.0"),sQuery(id+"F0.wireOp",EDGE,"E12.15.18.0"),sQuery(id+"F0.wireOp",EDGE,"E12.18.18.0"),sQuery(id+"F0.wireOp",EDGE,"E12.21.18.0"),sQuery(id+"F0.wireOp",EDGE,"E12.25.18.0"),sQuery(id+"F0.wireOp",EDGE,"E12.29.18.0"),sQuery(id+"F0.wireOp",EDGE,"E12.32.18.0"),sQuery(id+"F0.wireOp",EDGE,"E12.2.19.0"),sQuery(id+"F0.wireOp",EDGE,"E12.4.19.0"),sQuery(id+"F0.wireOp",EDGE,"E12.7.19.0"),sQuery(id+"F0.wireOp",EDGE,"E12.11.19.0"),sQuery(id+"F0.wireOp",EDGE,"E12.15.19.0"),sQuery(id+"F0.wireOp",EDGE,"E12.18.19.0"),sQuery(id+"F0.wireOp",EDGE,"E12.21.19.0"),sQuery(id+"F0.wireOp",EDGE,"E12.25.19.0"),sQuery(id+"F0.wireOp",EDGE,"E12.29.19.0"),sQuery(id+"F0.wireOp",EDGE,"E12.32.19.0"),sQuery(id+"F0.wireOp",EDGE,"E12.2.20.0"),sQuery(id+"F0.wireOp",EDGE,"E12.4.20.0"),sQuery(id+"F0.wireOp",EDGE,"E12.7.20.0"),sQuery(id+"F0.wireOp",EDGE,"E12.11.20.0"),sQuery(id+"F0.wireOp",EDGE,"E12.15.20.0"),sQuery(id+"F0.wireOp",EDGE,"E12.18.20.0"),sQuery(id+"F0.wireOp",EDGE,"E12.21.20.0"),sQuery(id+"F0.wireOp",EDGE,"E12.25.20.0"),sQuery(id+"F0.wireOp",EDGE,"E12.29.20.0"),sQuery(id+"F0.wireOp",EDGE,"E12.32.20.0"),sQuery(id+"F0.wireOp",EDGE,"E12.2.21.0"),sQuery(id+"F0.wireOp",EDGE,"E12.4.21.0"),sQuery(id+"F0.wireOp",EDGE,"E12.7.21.0"),sQuery(id+"F0.wireOp",EDGE,"E12.11.21.0"),sQuery(id+"F0.wireOp",EDGE,"E12.15.21.0"),sQuery(id+"F0.wireOp",EDGE,"E12.18.21.0"),sQuery(id+"F0.wireOp",EDGE,"E12.21.21.0"),sQuery(id+"F0.wireOp",EDGE,"E12.25.21.0"),sQuery(id+"F0.wireOp",EDGE,"E12.29.21.0"),sQuery(id+"F0.wireOp",EDGE,"E12.32.21.0"),sQuery(id+"F0.wireOp",EDGE,"E12.2.22.0"),sQuery(id+"F0.wireOp",EDGE,"E12.4.22.0"),sQuery(id+"F0.wireOp",EDGE,"E12.7.22.0"),sQuery(id+"F0.wireOp",EDGE,"E12.11.22.0"),sQuery(id+"F0.wireOp",EDGE,"E12.15.22.0"),sQuery(id+"F0.wireOp",EDGE,"E12.18.22.0"),sQuery(id+"F0.wireOp",EDGE,"E12.21.22.0"),sQuery(id+"F0.wireOp",EDGE,"E12.25.22.0"),sQuery(id+"F0.wireOp",EDGE,"E12.29.22.0"),sQuery(id+"F0.wireOp",EDGE,"E12.32.22.0"),sQuery(id+"F0.wireOp",EDGE,"E12.2.23.0"),sQuery(id+"F0.wireOp",EDGE,"E12.4.23.0"),sQuery(id+"F0.wireOp",EDGE,"E12.7.23.0"),sQuery(id+"F0.wireOp",EDGE,"E12.11.23.0"),sQuery(id+"F0.wireOp",EDGE,"E12.15.23.0"),sQuery(id+"F0.wireOp",EDGE,"E12.18.23.0"),sQuery(id+"F0.wireOp",EDGE,"E12.21.23.0"),sQuery(id+"F0.wireOp",EDGE,"E12.25.23.0"),sQuery(id+"F0.wireOp",EDGE,"E12.29.23.0"),sQuery(id+"F0.wireOp",EDGE,"E12.32.23.0"),sQuery(id+"F0.wireOp",EDGE,"E12.2.24.0"),sQuery(id+"F0.wireOp",EDGE,"E12.4.24.0"),sQuery(id+"F0.wireOp",EDGE,"E12.7.24.0"),sQuery(id+"F0.wireOp",EDGE,"E12.11.24.0"),sQuery(id+"F0.wireOp",EDGE,"E12.15.24.0"),sQuery(id+"F0.wireOp",EDGE,"E12.18.24.0"),sQuery(id+"F0.wireOp",EDGE,"E12.21.24.0"),sQuery(id+"F0.wireOp",EDGE,"E12.25.24.0"),sQuery(id+"F0.wireOp",EDGE,"E12.29.24.0"),sQuery(id+"F0.wireOp",EDGE,"E12.32.24.0"),sQuery(id+"F0.wireOp",EDGE,"E12.2.25.0"),sQuery(id+"F0.wireOp",EDGE,"E12.4.25.0"),sQuery(id+"F0.wireOp",EDGE,"E12.7.25.0"),sQuery(id+"F0.wireOp",EDGE,"E12.11.25.0"),sQuery(id+"F0.wireOp",EDGE,"E12.15.25.0"),sQuery(id+"F0.wireOp",EDGE,"E12.18.25.0"),sQuery(id+"F0.wireOp",EDGE,"E12.21.25.0"),sQuery(id+"F0.wireOp",EDGE,"E12.25.25.0"),sQuery(id+"F0.wireOp",EDGE,"E12.29.25.0"),sQuery(id+"F0.wireOp",EDGE,"E12.32.25.0"),sQuery(id+"F0.wireOp",EDGE,"E12.2.26.0"),sQuery(id+"F0.wireOp",EDGE,"E12.4.26.0"),sQuery(id+"F0.wireOp",EDGE,"E12.7.26.0"),sQuery(id+"F0.wireOp",EDGE,"E12.11.26.0"),sQuery(id+"F0.wireOp",EDGE,"E12.15.26.0"),sQuery(id+"F0.wireOp",EDGE,"E12.18.26.0"),sQuery(id+"F0.wireOp",EDGE,"E12.21.26.0"),sQuery(id+"F0.wireOp",EDGE,"E12.25.26.0"),sQuery(id+"F0.wireOp",EDGE,"E12.29.26.0"),sQuery(id+"F0.wireOp",EDGE,"E12.32.26.0"),sQuery(id+"F0.wireOp",EDGE,"E12.2.27.0"),sQuery(id+"F0.wireOp",EDGE,"E12.4.27.0"),sQuery(id+"F0.wireOp",EDGE,"E12.7.27.0"),sQuery(id+"F0.wireOp",EDGE,"E12.11.27.0"),sQuery(id+"F0.wireOp",EDGE,"E12.15.27.0"),sQuery(id+"F0.wireOp",EDGE,"E12.18.27.0"),sQuery(id+"F0.wireOp",EDGE,"E12.21.27.0"),sQuery(id+"F0.wireOp",EDGE,"E12.25.27.0"),sQuery(id+"F0.wireOp",EDGE,"E12.29.27.0"),sQuery(id+"F0.wireOp",EDGE,"E12.32.27.0"),sQuery(id+"F0.wireOp",EDGE,"E12.2.28.0"),sQuery(id+"F0.wireOp",EDGE,"E12.4.28.0"),sQuery(id+"F0.wireOp",EDGE,"E12.7.28.0"),sQuery(id+"F0.wireOp",EDGE,"E12.11.28.0"),sQuery(id+"F0.wireOp",EDGE,"E12.15.28.0"),sQuery(id+"F0.wireOp",EDGE,"E12.18.28.0"),sQuery(id+"F0.wireOp",EDGE,"E12.21.28.0"),sQuery(id+"F0.wireOp",EDGE,"E12.25.28.0"),sQuery(id+"F0.wireOp",EDGE,"E12.29.28.0"),sQuery(id+"F0.wireOp",EDGE,"E12.32.28.0"),sQuery(id+"F0.wireOp",EDGE,"E12.2.29.0"),sQuery(id+"F0.wireOp",EDGE,"E12.4.29.0"),sQuery(id+"F0.wireOp",EDGE,"E12.7.29.0"),sQuery(id+"F0.wireOp",EDGE,"E12.11.29.0"),sQuery(id+"F0.wireOp",EDGE,"E12.15.29.0"),sQuery(id+"F0.wireOp",EDGE,"E12.18.29.0"),sQuery(id+"F0.wireOp",EDGE,"E12.21.29.0"),sQuery(id+"F0.wireOp",EDGE,"E12.25.29.0"),sQuery(id+"F0.wireOp",EDGE,"E12.29.29.0"),sQuery(id+"F0.wireOp",EDGE,"E12.32.29.0"),sQuery(id+"F0.wireOp",EDGE,"E12.2.30.0"),sQuery(id+"F0.wireOp",EDGE,"E12.4.30.0"),sQuery(id+"F0.wireOp",EDGE,"E12.7.30.0"),sQuery(id+"F0.wireOp",EDGE,"E12.11.30.0"),sQuery(id+"F0.wireOp",EDGE,"E12.15.30.0"),sQuery(id+"F0.wireOp",EDGE,"E12.18.30.0"),sQuery(id+"F0.wireOp",EDGE,"E12.21.30.0"),sQuery(id+"F0.wireOp",EDGE,"E12.25.30.0"),sQuery(id+"F0.wireOp",EDGE,"E12.29.30.0"),sQuery(id+"F0.wireOp",EDGE,"E12.32.30.0"),sQuery(id+"F0.wireOp",EDGE,"E12.2.31.0"),sQuery(id+"F0.wireOp",EDGE,"E12.4.31.0"),sQuery(id+"F0.wireOp",EDGE,"E12.7.31.0"),sQuery(id+"F0.wireOp",EDGE,"E12.11.31.0"),sQuery(id+"F0.wireOp",EDGE,"E12.15.31.0"),sQuery(id+"F0.wireOp",EDGE,"E12.18.31.0"),sQuery(id+"F0.wireOp",EDGE,"E12.21.31.0"),sQuery(id+"F0.wireOp",EDGE,"E12.25.31.0"),sQuery(id+"F0.wireOp",EDGE,"E12.29.31.0"),sQuery(id+"F0.wireOp",EDGE,"E12.32.31.0"),sQuery(id+"F0.wireOp",EDGE,"E12.2.32.0"),sQuery(id+"F0.wireOp",EDGE,"E12.4.32.0"),sQuery(id+"F0.wireOp",EDGE,"E12.7.32.0"),sQuery(id+"F0.wireOp",EDGE,"E12.11.32.0"),sQuery(id+"F0.wireOp",EDGE,"E12.15.32.0"),sQuery(id+"F0.wireOp",EDGE,"E12.18.32.0"),sQuery(id+"F0.wireOp",EDGE,"E12.21.32.0"),sQuery(id+"F0.wireOp",EDGE,"E12.25.32.0"),sQuery(id+"F0.wireOp",EDGE,"E12.29.32.0"),sQuery(id+"F0.wireOp",EDGE,"E12.32.32.0"),sQuery(id+"F0.wireOp",EDGE,"E12.2.33.0"),sQuery(id+"F0.wireOp",EDGE,"E12.4.33.0"),sQuery(id+"F0.wireOp",EDGE,"E12.7.33.0"),sQuery(id+"F0.wireOp",EDGE,"E12.11.33.0"),sQuery(id+"F0.wireOp",EDGE,"E12.15.33.0"),sQuery(id+"F0.wireOp",EDGE,"E12.18.33.0"),sQuery(id+"F0.wireOp",EDGE,"E12.21.33.0"),sQuery(id+"F0.wireOp",EDGE,"E12.25.33.0"),sQuery(id+"F0.wireOp",EDGE,"E12.29.33.0"),sQuery(id+"F0.wireOp",EDGE,"E12.32.33.0"),sQuery(id+"F0.wireOp",EDGE,"E12.2.34.0"),sQuery(id+"F0.wireOp",EDGE,"E12.4.34.0"),sQuery(id+"F0.wireOp",EDGE,"E12.7.34.0"),sQuery(id+"F0.wireOp",EDGE,"E12.11.34.0"),sQuery(id+"F0.wireOp",EDGE,"E12.15.34.0"),sQuery(id+"F0.wireOp",EDGE,"E12.18.34.0"),sQuery(id+"F0.wireOp",EDGE,"E12.21.34.0"),sQuery(id+"F0.wireOp",EDGE,"E12.25.34.0"),sQuery(id+"F0.wireOp",EDGE,"E12.29.34.0"),sQuery(id+"F0.wireOp",EDGE,"E12.32.34.0"),sQuery(id+"F0.wireOp",EDGE,"E12.2.35.0"),sQuery(id+"F0.wireOp",EDGE,"E12.4.35.0"),sQuery(id+"F0.wireOp",EDGE,"E12.7.35.0"),sQuery(id+"F0.wireOp",EDGE,"E12.11.35.0"),sQuery(id+"F0.wireOp",EDGE,"E12.15.35.0"),sQuery(id+"F0.wireOp",EDGE,"E12.18.35.0"),sQuery(id+"F0.wireOp",EDGE,"E12.21.35.0"),sQuery(id+"F0.wireOp",EDGE,"E12.25.35.0"),sQuery(id+"F0.wireOp",EDGE,"E12.29.35.0"),sQuery(id+"F0.wireOp",EDGE,"E12.32.35.0"),sQuery(id+"F0.wireOp",EDGE,"E13.trimOffspring"),sQuery(id+"F0.wireOp",EDGE,"E14.trimOffspring"),sQuery(id+"F0.wireOp",EDGE,"E15.trimOffspring"),sQuery(id+"F0.wireOp",EDGE,"E16.trimOffspring"),sQuery(id+"F0.wireOp",EDGE,"E17.trimOffspring"),sQuery(id+"F0.wireOp",EDGE,"E18.trimOffspring"),sQuery(id+"F0.wireOp",EDGE,"E19.trimOffspring"),sQuery(id+"F0.wireOp",EDGE,"E20.trimOffspring"),sQuery(id+"F0.wireOp",EDGE,"E21.trimOffspring"),sQuery(id+"F0.wireOp",EDGE,"E22.trimOffspring"),sQuery(id+"F0.wireOp",EDGE,"E23.trimOffspring"),sQuery(id+"F0.wireOp",EDGE,"E24.trimOffspring"),sQuery(id+"F0.wireOp",EDGE,"E25.trimOffspring"),sQuery(id+"F0.wireOp",EDGE,"E26.trimOffspring"),sQuery(id+"F0.wireOp",EDGE,"E27.trimOffspring"),sQuery(id+"F0.wireOp",EDGE,"E28.trimOffspring"),sQuery(id+"F0.wireOp",EDGE,"E29.trimOffspring"),sQuery(id+"F0.wireOp",EDGE,"E30.trimOffspring"),sQuery(id+"F0.wireOp",EDGE,"E31.trimOffspring"),sQuery(id+"F0.wireOp",EDGE,"E32.trimOffspring"),sQuery(id+"F0.wireOp",EDGE,"E33.trimOffspring"),sQuery(id+"F0.wireOp",EDGE,"E34.trimOffspring"),sQuery(id+"F0.wireOp",EDGE,"E35.trimOffspring"),sQuery(id+"F0.wireOp",EDGE,"E36.trimOffspring"),sQuery(id+"F0.wireOp",EDGE,"E37.trimOffspring"),sQuery(id+"F0.wireOp",EDGE,"E38.trimOffspring"),sQuery(id+"F0.wireOp",EDGE,"E39.trimOffspring"),sQuery(id+"F0.wireOp",EDGE,"E40.trimOffspring"),sQuery(id+"F0.wireOp",EDGE,"E41.trimOffspring"),sQuery(id+"F0.wireOp",EDGE,"E42.trimOffspring"),sQuery(id+"F0.wireOp",EDGE,"E43.trimOffspring"),sQuery(id+"F0.wireOp",EDGE,"E44.trimOffspring"),sQuery(id+"F0.wireOp",EDGE,"E45.trimOffspring"),sQuery(id+"F0.wireOp",EDGE,"E46.trimOffspring"),sQuery(id+"F0.wireOp",EDGE,"E47.trimOffspring")])]});
            hole(context, id + "F8", {"style" : HoleStyle.C_BORE, "endStyle" : HoleEndStyle.THROUGH, "holeDiameter" : 6.35 * mm, "cBoreDiameter" : 12.7 * mm, "cBoreDepth" : 3.17 * mm, "locations" : qUnion([Q0]), "scope" : qUnion([Q1]), "isTappedThrough" : true});
        }
        {
            var Q0;
            Q0=makeQuery(id+"F5.opExtrude","CAP_EDGE",EDGE,{"disambiguationData":[OSD([sQuery(id+"F4.wireOp",EDGE,"E66")])],"isStart":false});
            chamfer(context, id + "F9", {"entities" : qUnion([Q0]), "chamferType" : ChamferType.OFFSET_ANGLE, "width" : 0.38 * mm, "oppositeDirection" : false, "angle" : 60 * degree, "tangentPropagation" : true});
        }
        {
            var Q0;
            Q0=makeQuery(id+"F3.boolean.opBoolean","COPY",FACE,{"derivedFrom":makeQuery(id+"F3.opExtrude","SWEPT_FACE",FACE,{"disambiguationData":[OSD([sQuery(id+"F2.wireOp",EDGE,"E65.1.0")])]})});
            var Q1;
            Q1=makeQuery(id+"F3.boolean.opBoolean","COPY",FACE,{"derivedFrom":makeQuery(id+"F3.opExtrude","SWEPT_FACE",FACE,{"disambiguationData":[OSD([sQuery(id+"F2.wireOp",EDGE,"E64")])]})});
            var Q2;
            Q2=makeQuery(id+"F3.boolean.opBoolean","COPY",FACE,{"derivedFrom":makeQuery(id+"F3.opExtrude","SWEPT_FACE",FACE,{"disambiguationData":[OSD([sQuery(id+"F2.wireOp",EDGE,"E65.11.0")])]})});
            var Q3;
            Q3=makeQuery(id+"F3.boolean.opBoolean","COPY",FACE,{"derivedFrom":makeQuery(id+"F3.opExtrude","SWEPT_FACE",FACE,{"disambiguationData":[OSD([sQuery(id+"F2.wireOp",EDGE,"E65.10.0")])]})});
            var Q4;
            Q4=makeQuery(id+"F3.boolean.opBoolean","COPY",FACE,{"derivedFrom":makeQuery(id+"F3.opExtrude","SWEPT_FACE",FACE,{"disambiguationData":[OSD([sQuery(id+"F2.wireOp",EDGE,"E65.9.0")])]})});
            var Q5;
            Q5=makeQuery(id+"F3.boolean.opBoolean","COPY",FACE,{"derivedFrom":makeQuery(id+"F3.opExtrude","SWEPT_FACE",FACE,{"disambiguationData":[OSD([sQuery(id+"F2.wireOp",EDGE,"E65.8.0")])]})});
            var Q6;
            Q6=makeQuery(id+"F3.boolean.opBoolean","COPY",FACE,{"derivedFrom":makeQuery(id+"F3.opExtrude","SWEPT_FACE",FACE,{"disambiguationData":[OSD([sQuery(id+"F2.wireOp",EDGE,"E65.7.0")])]})});
            var Q7;
            Q7=makeQuery(id+"F3.boolean.opBoolean","COPY",FACE,{"derivedFrom":makeQuery(id+"F3.opExtrude","SWEPT_FACE",FACE,{"disambiguationData":[OSD([sQuery(id+"F2.wireOp",EDGE,"E65.6.0")])]})});
            var Q8;
            Q8=makeQuery(id+"F3.boolean.opBoolean","COPY",FACE,{"derivedFrom":makeQuery(id+"F3.opExtrude","SWEPT_FACE",FACE,{"disambiguationData":[OSD([sQuery(id+"F2.wireOp",EDGE,"E65.5.0")])]})});
            var Q9;
            Q9=makeQuery(id+"F3.boolean.opBoolean","COPY",FACE,{"derivedFrom":makeQuery(id+"F3.opExtrude","SWEPT_FACE",FACE,{"disambiguationData":[OSD([sQuery(id+"F2.wireOp",EDGE,"E65.4.0")])]})});
            var Q10;
            Q10=makeQuery(id+"F3.boolean.opBoolean","COPY",FACE,{"derivedFrom":makeQuery(id+"F3.opExtrude","SWEPT_FACE",FACE,{"disambiguationData":[OSD([sQuery(id+"F2.wireOp",EDGE,"E65.3.0")])]})});
            var Q11;
            Q11=makeQuery(id+"F3.boolean.opBoolean","COPY",FACE,{"derivedFrom":makeQuery(id+"F3.opExtrude","SWEPT_FACE",FACE,{"disambiguationData":[OSD([sQuery(id+"F2.wireOp",EDGE,"E65.2.0")])]})});
            var Q12;
            Q12=makeQuery(id+"F3.boolean.opBoolean","COPY",FACE,{"derivedFrom":makeQuery(id+"F3.opExtrude","SWEPT_FACE",FACE,{"disambiguationData":[OSD([sQuery(id+"F2.wireOp",EDGE,"E56")])]})});
            var Q13;
            Q13=makeQuery(id+"F3.boolean.opBoolean","COPY",FACE,{"derivedFrom":makeQuery(id+"F3.opExtrude","SWEPT_FACE",FACE,{"disambiguationData":[OSD([sQuery(id+"F2.wireOp",EDGE,"E62.trimOffspring")])]})});
            var Q14;
            Q14=makeQuery(id+"F3.boolean.opBoolean","COPY",FACE,{"derivedFrom":makeQuery(id+"F3.opExtrude","SWEPT_FACE",FACE,{"disambiguationData":[OSD([sQuery(id+"F2.wireOp",EDGE,"E58.trimOffspring")])]})});
            var Q15;
            Q15=makeQuery(id+"F3.boolean.opBoolean","COPY",FACE,{"derivedFrom":makeQuery(id+"F3.opExtrude","SWEPT_FACE",FACE,{"disambiguationData":[OSD([sQuery(id+"F2.wireOp",EDGE,"E54.4.0")])]})});
            var Q16;
            Q16=makeQuery(id+"F8.hole-0.boolean.opBoolean","INTERSECT",EDGE,{"derivedFrom":[makeQuery(id+"F1.opExtrude","CAP_FACE",FACE,{"disambiguationData":[OSD([sQuery(id+"F0.wireOp",EDGE,"E0"),sQuery(id+"F0.wireOp",EDGE,"E1.trimOffspring"),sQuery(id+"F0.wireOp",EDGE,"E2"),sQuery(id+"F0.wireOp",EDGE,"E3"),sQuery(id+"F0.wireOp",EDGE,"E4.MirrorCS"),sQuery(id+"F0.wireOp",EDGE,"E5.MirrorCS"),sQuery(id+"F0.wireOp",EDGE,"E6.MirrorCS"),sQuery(id+"F0.wireOp",EDGE,"E7.filletArc"),sQuery(id+"F0.wireOp",EDGE,"E8.filletArc"),sQuery(id+"F0.wireOp",EDGE,"E9.filletArc"),sQuery(id+"F0.wireOp",EDGE,"E10.filletArc"),sQuery(id+"F0.wireOp",EDGE,"E11.1.0"),sQuery(id+"F0.wireOp",EDGE,"E11.1.1"),sQuery(id+"F0.wireOp",EDGE,"E11.1.2"),sQuery(id+"F0.wireOp",EDGE,"E11.1.3"),sQuery(id+"F0.wireOp",EDGE,"E11.1.4"),sQuery(id+"F0.wireOp",EDGE,"E11.1.5"),sQuery(id+"F0.wireOp",EDGE,"E11.1.6"),sQuery(id+"F0.wireOp",EDGE,"E11.1.7"),sQuery(id+"F0.wireOp",EDGE,"E11.1.8"),sQuery(id+"F0.wireOp",EDGE,"E11.1.9"),sQuery(id+"F0.wireOp",EDGE,"E11.2.0"),sQuery(id+"F0.wireOp",EDGE,"E11.2.1"),sQuery(id+"F0.wireOp",EDGE,"E11.2.2"),sQuery(id+"F0.wireOp",EDGE,"E11.2.3"),sQuery(id+"F0.wireOp",EDGE,"E11.2.4"),sQuery(id+"F0.wireOp",EDGE,"E11.2.5"),sQuery(id+"F0.wireOp",EDGE,"E11.2.6"),sQuery(id+"F0.wireOp",EDGE,"E11.2.7"),sQuery(id+"F0.wireOp",EDGE,"E11.2.8"),sQuery(id+"F0.wireOp",EDGE,"E11.2.9"),sQuery(id+"F0.wireOp",EDGE,"E12.2.3.0"),sQuery(id+"F0.wireOp",EDGE,"E12.4.3.0"),sQuery(id+"F0.wireOp",EDGE,"E12.7.3.0"),sQuery(id+"F0.wireOp",EDGE,"E12.11.3.0"),sQuery(id+"F0.wireOp",EDGE,"E12.15.3.0"),sQuery(id+"F0.wireOp",EDGE,"E12.18.3.0"),sQuery(id+"F0.wireOp",EDGE,"E12.21.3.0"),sQuery(id+"F0.wireOp",EDGE,"E12.25.3.0"),sQuery(id+"F0.wireOp",EDGE,"E12.29.3.0"),sQuery(id+"F0.wireOp",EDGE,"E12.32.3.0"),sQuery(id+"F0.wireOp",EDGE,"E12.2.4.0"),sQuery(id+"F0.wireOp",EDGE,"E12.4.4.0"),sQuery(id+"F0.wireOp",EDGE,"E12.7.4.0"),sQuery(id+"F0.wireOp",EDGE,"E12.11.4.0"),sQuery(id+"F0.wireOp",EDGE,"E12.15.4.0"),sQuery(id+"F0.wireOp",EDGE,"E12.18.4.0"),sQuery(id+"F0.wireOp",EDGE,"E12.21.4.0"),sQuery(id+"F0.wireOp",EDGE,"E12.25.4.0"),sQuery(id+"F0.wireOp",EDGE,"E12.29.4.0"),sQuery(id+"F0.wireOp",EDGE,"E12.32.4.0"),sQuery(id+"F0.wireOp",EDGE,"E12.2.5.0"),sQuery(id+"F0.wireOp",EDGE,"E12.4.5.0"),sQuery(id+"F0.wireOp",EDGE,"E12.7.5.0"),sQuery(id+"F0.wireOp",EDGE,"E12.11.5.0"),sQuery(id+"F0.wireOp",EDGE,"E12.15.5.0"),sQuery(id+"F0.wireOp",EDGE,"E12.18.5.0"),sQuery(id+"F0.wireOp",EDGE,"E12.21.5.0"),sQuery(id+"F0.wireOp",EDGE,"E12.25.5.0"),sQuery(id+"F0.wireOp",EDGE,"E12.29.5.0"),sQuery(id+"F0.wireOp",EDGE,"E12.32.5.0"),sQuery(id+"F0.wireOp",EDGE,"E12.2.6.0"),sQuery(id+"F0.wireOp",EDGE,"E12.4.6.0"),sQuery(id+"F0.wireOp",EDGE,"E12.7.6.0"),sQuery(id+"F0.wireOp",EDGE,"E12.11.6.0"),sQuery(id+"F0.wireOp",EDGE,"E12.15.6.0"),sQuery(id+"F0.wireOp",EDGE,"E12.18.6.0"),sQuery(id+"F0.wireOp",EDGE,"E12.21.6.0"),sQuery(id+"F0.wireOp",EDGE,"E12.25.6.0"),sQuery(id+"F0.wireOp",EDGE,"E12.29.6.0"),sQuery(id+"F0.wireOp",EDGE,"E12.32.6.0"),sQuery(id+"F0.wireOp",EDGE,"E12.2.7.0"),sQuery(id+"F0.wireOp",EDGE,"E12.4.7.0"),sQuery(id+"F0.wireOp",EDGE,"E12.7.7.0"),sQuery(id+"F0.wireOp",EDGE,"E12.11.7.0"),sQuery(id+"F0.wireOp",EDGE,"E12.15.7.0"),sQuery(id+"F0.wireOp",EDGE,"E12.18.7.0"),sQuery(id+"F0.wireOp",EDGE,"E12.21.7.0"),sQuery(id+"F0.wireOp",EDGE,"E12.25.7.0"),sQuery(id+"F0.wireOp",EDGE,"E12.29.7.0"),sQuery(id+"F0.wireOp",EDGE,"E12.32.7.0"),sQuery(id+"F0.wireOp",EDGE,"E12.2.8.0"),sQuery(id+"F0.wireOp",EDGE,"E12.4.8.0"),sQuery(id+"F0.wireOp",EDGE,"E12.7.8.0"),sQuery(id+"F0.wireOp",EDGE,"E12.11.8.0"),sQuery(id+"F0.wireOp",EDGE,"E12.15.8.0"),sQuery(id+"F0.wireOp",EDGE,"E12.18.8.0"),sQuery(id+"F0.wireOp",EDGE,"E12.21.8.0"),sQuery(id+"F0.wireOp",EDGE,"E12.25.8.0"),sQuery(id+"F0.wireOp",EDGE,"E12.29.8.0"),sQuery(id+"F0.wireOp",EDGE,"E12.32.8.0"),sQuery(id+"F0.wireOp",EDGE,"E12.2.9.0"),sQuery(id+"F0.wireOp",EDGE,"E12.4.9.0"),sQuery(id+"F0.wireOp",EDGE,"E12.7.9.0"),sQuery(id+"F0.wireOp",EDGE,"E12.11.9.0"),sQuery(id+"F0.wireOp",EDGE,"E12.15.9.0"),sQuery(id+"F0.wireOp",EDGE,"E12.18.9.0"),sQuery(id+"F0.wireOp",EDGE,"E12.21.9.0"),sQuery(id+"F0.wireOp",EDGE,"E12.25.9.0"),sQuery(id+"F0.wireOp",EDGE,"E12.29.9.0"),sQuery(id+"F0.wireOp",EDGE,"E12.32.9.0"),sQuery(id+"F0.wireOp",EDGE,"E12.2.10.0"),sQuery(id+"F0.wireOp",EDGE,"E12.4.10.0"),sQuery(id+"F0.wireOp",EDGE,"E12.7.10.0"),sQuery(id+"F0.wireOp",EDGE,"E12.11.10.0"),sQuery(id+"F0.wireOp",EDGE,"E12.15.10.0"),sQuery(id+"F0.wireOp",EDGE,"E12.18.10.0"),sQuery(id+"F0.wireOp",EDGE,"E12.21.10.0"),sQuery(id+"F0.wireOp",EDGE,"E12.25.10.0"),sQuery(id+"F0.wireOp",EDGE,"E12.29.10.0"),sQuery(id+"F0.wireOp",EDGE,"E12.32.10.0"),sQuery(id+"F0.wireOp",EDGE,"E12.2.11.0"),sQuery(id+"F0.wireOp",EDGE,"E12.4.11.0"),sQuery(id+"F0.wireOp",EDGE,"E12.7.11.0"),sQuery(id+"F0.wireOp",EDGE,"E12.11.11.0"),sQuery(id+"F0.wireOp",EDGE,"E12.15.11.0"),sQuery(id+"F0.wireOp",EDGE,"E12.18.11.0"),sQuery(id+"F0.wireOp",EDGE,"E12.21.11.0"),sQuery(id+"F0.wireOp",EDGE,"E12.25.11.0"),sQuery(id+"F0.wireOp",EDGE,"E12.29.11.0"),sQuery(id+"F0.wireOp",EDGE,"E12.32.11.0"),sQuery(id+"F0.wireOp",EDGE,"E12.2.12.0"),sQuery(id+"F0.wireOp",EDGE,"E12.4.12.0"),sQuery(id+"F0.wireOp",EDGE,"E12.7.12.0"),sQuery(id+"F0.wireOp",EDGE,"E12.11.12.0"),sQuery(id+"F0.wireOp",EDGE,"E12.15.12.0"),sQuery(id+"F0.wireOp",EDGE,"E12.18.12.0"),sQuery(id+"F0.wireOp",EDGE,"E12.21.12.0"),sQuery(id+"F0.wireOp",EDGE,"E12.25.12.0"),sQuery(id+"F0.wireOp",EDGE,"E12.29.12.0"),sQuery(id+"F0.wireOp",EDGE,"E12.32.12.0"),sQuery(id+"F0.wireOp",EDGE,"E12.2.13.0"),sQuery(id+"F0.wireOp",EDGE,"E12.4.13.0"),sQuery(id+"F0.wireOp",EDGE,"E12.7.13.0"),sQuery(id+"F0.wireOp",EDGE,"E12.11.13.0"),sQuery(id+"F0.wireOp",EDGE,"E12.15.13.0"),sQuery(id+"F0.wireOp",EDGE,"E12.18.13.0"),sQuery(id+"F0.wireOp",EDGE,"E12.21.13.0"),sQuery(id+"F0.wireOp",EDGE,"E12.25.13.0"),sQuery(id+"F0.wireOp",EDGE,"E12.29.13.0"),sQuery(id+"F0.wireOp",EDGE,"E12.32.13.0"),sQuery(id+"F0.wireOp",EDGE,"E12.2.14.0"),sQuery(id+"F0.wireOp",EDGE,"E12.4.14.0"),sQuery(id+"F0.wireOp",EDGE,"E12.7.14.0"),sQuery(id+"F0.wireOp",EDGE,"E12.11.14.0"),sQuery(id+"F0.wireOp",EDGE,"E12.15.14.0"),sQuery(id+"F0.wireOp",EDGE,"E12.18.14.0"),sQuery(id+"F0.wireOp",EDGE,"E12.21.14.0"),sQuery(id+"F0.wireOp",EDGE,"E12.25.14.0"),sQuery(id+"F0.wireOp",EDGE,"E12.29.14.0"),sQuery(id+"F0.wireOp",EDGE,"E12.32.14.0"),sQuery(id+"F0.wireOp",EDGE,"E12.2.15.0"),sQuery(id+"F0.wireOp",EDGE,"E12.4.15.0"),sQuery(id+"F0.wireOp",EDGE,"E12.7.15.0"),sQuery(id+"F0.wireOp",EDGE,"E12.11.15.0"),sQuery(id+"F0.wireOp",EDGE,"E12.15.15.0"),sQuery(id+"F0.wireOp",EDGE,"E12.18.15.0"),sQuery(id+"F0.wireOp",EDGE,"E12.21.15.0"),sQuery(id+"F0.wireOp",EDGE,"E12.25.15.0"),sQuery(id+"F0.wireOp",EDGE,"E12.29.15.0"),sQuery(id+"F0.wireOp",EDGE,"E12.32.15.0"),sQuery(id+"F0.wireOp",EDGE,"E12.2.16.0"),sQuery(id+"F0.wireOp",EDGE,"E12.4.16.0"),sQuery(id+"F0.wireOp",EDGE,"E12.7.16.0"),sQuery(id+"F0.wireOp",EDGE,"E12.11.16.0"),sQuery(id+"F0.wireOp",EDGE,"E12.15.16.0"),sQuery(id+"F0.wireOp",EDGE,"E12.18.16.0"),sQuery(id+"F0.wireOp",EDGE,"E12.21.16.0"),sQuery(id+"F0.wireOp",EDGE,"E12.25.16.0"),sQuery(id+"F0.wireOp",EDGE,"E12.29.16.0"),sQuery(id+"F0.wireOp",EDGE,"E12.32.16.0"),sQuery(id+"F0.wireOp",EDGE,"E12.2.17.0"),sQuery(id+"F0.wireOp",EDGE,"E12.4.17.0"),sQuery(id+"F0.wireOp",EDGE,"E12.7.17.0"),sQuery(id+"F0.wireOp",EDGE,"E12.11.17.0"),sQuery(id+"F0.wireOp",EDGE,"E12.15.17.0"),sQuery(id+"F0.wireOp",EDGE,"E12.18.17.0"),sQuery(id+"F0.wireOp",EDGE,"E12.21.17.0"),sQuery(id+"F0.wireOp",EDGE,"E12.25.17.0"),sQuery(id+"F0.wireOp",EDGE,"E12.29.17.0"),sQuery(id+"F0.wireOp",EDGE,"E12.32.17.0"),sQuery(id+"F0.wireOp",EDGE,"E12.2.18.0"),sQuery(id+"F0.wireOp",EDGE,"E12.4.18.0"),sQuery(id+"F0.wireOp",EDGE,"E12.7.18.0"),sQuery(id+"F0.wireOp",EDGE,"E12.11.18.0"),sQuery(id+"F0.wireOp",EDGE,"E12.15.18.0"),sQuery(id+"F0.wireOp",EDGE,"E12.18.18.0"),sQuery(id+"F0.wireOp",EDGE,"E12.21.18.0"),sQuery(id+"F0.wireOp",EDGE,"E12.25.18.0"),sQuery(id+"F0.wireOp",EDGE,"E12.29.18.0"),sQuery(id+"F0.wireOp",EDGE,"E12.32.18.0"),sQuery(id+"F0.wireOp",EDGE,"E12.2.19.0"),sQuery(id+"F0.wireOp",EDGE,"E12.4.19.0"),sQuery(id+"F0.wireOp",EDGE,"E12.7.19.0"),sQuery(id+"F0.wireOp",EDGE,"E12.11.19.0"),sQuery(id+"F0.wireOp",EDGE,"E12.15.19.0"),sQuery(id+"F0.wireOp",EDGE,"E12.18.19.0"),sQuery(id+"F0.wireOp",EDGE,"E12.21.19.0"),sQuery(id+"F0.wireOp",EDGE,"E12.25.19.0"),sQuery(id+"F0.wireOp",EDGE,"E12.29.19.0"),sQuery(id+"F0.wireOp",EDGE,"E12.32.19.0"),sQuery(id+"F0.wireOp",EDGE,"E12.2.20.0"),sQuery(id+"F0.wireOp",EDGE,"E12.4.20.0"),sQuery(id+"F0.wireOp",EDGE,"E12.7.20.0"),sQuery(id+"F0.wireOp",EDGE,"E12.11.20.0"),sQuery(id+"F0.wireOp",EDGE,"E12.15.20.0"),sQuery(id+"F0.wireOp",EDGE,"E12.18.20.0"),sQuery(id+"F0.wireOp",EDGE,"E12.21.20.0"),sQuery(id+"F0.wireOp",EDGE,"E12.25.20.0"),sQuery(id+"F0.wireOp",EDGE,"E12.29.20.0"),sQuery(id+"F0.wireOp",EDGE,"E12.32.20.0"),sQuery(id+"F0.wireOp",EDGE,"E12.2.21.0"),sQuery(id+"F0.wireOp",EDGE,"E12.4.21.0"),sQuery(id+"F0.wireOp",EDGE,"E12.7.21.0"),sQuery(id+"F0.wireOp",EDGE,"E12.11.21.0"),sQuery(id+"F0.wireOp",EDGE,"E12.15.21.0"),sQuery(id+"F0.wireOp",EDGE,"E12.18.21.0"),sQuery(id+"F0.wireOp",EDGE,"E12.21.21.0"),sQuery(id+"F0.wireOp",EDGE,"E12.25.21.0"),sQuery(id+"F0.wireOp",EDGE,"E12.29.21.0"),sQuery(id+"F0.wireOp",EDGE,"E12.32.21.0"),sQuery(id+"F0.wireOp",EDGE,"E12.2.22.0"),sQuery(id+"F0.wireOp",EDGE,"E12.4.22.0"),sQuery(id+"F0.wireOp",EDGE,"E12.7.22.0"),sQuery(id+"F0.wireOp",EDGE,"E12.11.22.0"),sQuery(id+"F0.wireOp",EDGE,"E12.15.22.0"),sQuery(id+"F0.wireOp",EDGE,"E12.18.22.0"),sQuery(id+"F0.wireOp",EDGE,"E12.21.22.0"),sQuery(id+"F0.wireOp",EDGE,"E12.25.22.0"),sQuery(id+"F0.wireOp",EDGE,"E12.29.22.0"),sQuery(id+"F0.wireOp",EDGE,"E12.32.22.0"),sQuery(id+"F0.wireOp",EDGE,"E12.2.23.0"),sQuery(id+"F0.wireOp",EDGE,"E12.4.23.0"),sQuery(id+"F0.wireOp",EDGE,"E12.7.23.0"),sQuery(id+"F0.wireOp",EDGE,"E12.11.23.0"),sQuery(id+"F0.wireOp",EDGE,"E12.15.23.0"),sQuery(id+"F0.wireOp",EDGE,"E12.18.23.0"),sQuery(id+"F0.wireOp",EDGE,"E12.21.23.0"),sQuery(id+"F0.wireOp",EDGE,"E12.25.23.0"),sQuery(id+"F0.wireOp",EDGE,"E12.29.23.0"),sQuery(id+"F0.wireOp",EDGE,"E12.32.23.0"),sQuery(id+"F0.wireOp",EDGE,"E12.2.24.0"),sQuery(id+"F0.wireOp",EDGE,"E12.4.24.0"),sQuery(id+"F0.wireOp",EDGE,"E12.7.24.0"),sQuery(id+"F0.wireOp",EDGE,"E12.11.24.0"),sQuery(id+"F0.wireOp",EDGE,"E12.15.24.0"),sQuery(id+"F0.wireOp",EDGE,"E12.18.24.0"),sQuery(id+"F0.wireOp",EDGE,"E12.21.24.0"),sQuery(id+"F0.wireOp",EDGE,"E12.25.24.0"),sQuery(id+"F0.wireOp",EDGE,"E12.29.24.0"),sQuery(id+"F0.wireOp",EDGE,"E12.32.24.0"),sQuery(id+"F0.wireOp",EDGE,"E12.2.25.0"),sQuery(id+"F0.wireOp",EDGE,"E12.4.25.0"),sQuery(id+"F0.wireOp",EDGE,"E12.7.25.0"),sQuery(id+"F0.wireOp",EDGE,"E12.11.25.0"),sQuery(id+"F0.wireOp",EDGE,"E12.15.25.0"),sQuery(id+"F0.wireOp",EDGE,"E12.18.25.0"),sQuery(id+"F0.wireOp",EDGE,"E12.21.25.0"),sQuery(id+"F0.wireOp",EDGE,"E12.25.25.0"),sQuery(id+"F0.wireOp",EDGE,"E12.29.25.0"),sQuery(id+"F0.wireOp",EDGE,"E12.32.25.0"),sQuery(id+"F0.wireOp",EDGE,"E12.2.26.0"),sQuery(id+"F0.wireOp",EDGE,"E12.4.26.0"),sQuery(id+"F0.wireOp",EDGE,"E12.7.26.0"),sQuery(id+"F0.wireOp",EDGE,"E12.11.26.0"),sQuery(id+"F0.wireOp",EDGE,"E12.15.26.0"),sQuery(id+"F0.wireOp",EDGE,"E12.18.26.0"),sQuery(id+"F0.wireOp",EDGE,"E12.21.26.0"),sQuery(id+"F0.wireOp",EDGE,"E12.25.26.0"),sQuery(id+"F0.wireOp",EDGE,"E12.29.26.0"),sQuery(id+"F0.wireOp",EDGE,"E12.32.26.0"),sQuery(id+"F0.wireOp",EDGE,"E12.2.27.0"),sQuery(id+"F0.wireOp",EDGE,"E12.4.27.0"),sQuery(id+"F0.wireOp",EDGE,"E12.7.27.0"),sQuery(id+"F0.wireOp",EDGE,"E12.11.27.0"),sQuery(id+"F0.wireOp",EDGE,"E12.15.27.0"),sQuery(id+"F0.wireOp",EDGE,"E12.18.27.0"),sQuery(id+"F0.wireOp",EDGE,"E12.21.27.0"),sQuery(id+"F0.wireOp",EDGE,"E12.25.27.0"),sQuery(id+"F0.wireOp",EDGE,"E12.29.27.0"),sQuery(id+"F0.wireOp",EDGE,"E12.32.27.0"),sQuery(id+"F0.wireOp",EDGE,"E12.2.28.0"),sQuery(id+"F0.wireOp",EDGE,"E12.4.28.0"),sQuery(id+"F0.wireOp",EDGE,"E12.7.28.0"),sQuery(id+"F0.wireOp",EDGE,"E12.11.28.0"),sQuery(id+"F0.wireOp",EDGE,"E12.15.28.0"),sQuery(id+"F0.wireOp",EDGE,"E12.18.28.0"),sQuery(id+"F0.wireOp",EDGE,"E12.21.28.0"),sQuery(id+"F0.wireOp",EDGE,"E12.25.28.0"),sQuery(id+"F0.wireOp",EDGE,"E12.29.28.0"),sQuery(id+"F0.wireOp",EDGE,"E12.32.28.0"),sQuery(id+"F0.wireOp",EDGE,"E12.2.29.0"),sQuery(id+"F0.wireOp",EDGE,"E12.4.29.0"),sQuery(id+"F0.wireOp",EDGE,"E12.7.29.0"),sQuery(id+"F0.wireOp",EDGE,"E12.11.29.0"),sQuery(id+"F0.wireOp",EDGE,"E12.15.29.0"),sQuery(id+"F0.wireOp",EDGE,"E12.18.29.0"),sQuery(id+"F0.wireOp",EDGE,"E12.21.29.0"),sQuery(id+"F0.wireOp",EDGE,"E12.25.29.0"),sQuery(id+"F0.wireOp",EDGE,"E12.29.29.0"),sQuery(id+"F0.wireOp",EDGE,"E12.32.29.0"),sQuery(id+"F0.wireOp",EDGE,"E12.2.30.0"),sQuery(id+"F0.wireOp",EDGE,"E12.4.30.0"),sQuery(id+"F0.wireOp",EDGE,"E12.7.30.0"),sQuery(id+"F0.wireOp",EDGE,"E12.11.30.0"),sQuery(id+"F0.wireOp",EDGE,"E12.15.30.0"),sQuery(id+"F0.wireOp",EDGE,"E12.18.30.0"),sQuery(id+"F0.wireOp",EDGE,"E12.21.30.0"),sQuery(id+"F0.wireOp",EDGE,"E12.25.30.0"),sQuery(id+"F0.wireOp",EDGE,"E12.29.30.0"),sQuery(id+"F0.wireOp",EDGE,"E12.32.30.0"),sQuery(id+"F0.wireOp",EDGE,"E12.2.31.0"),sQuery(id+"F0.wireOp",EDGE,"E12.4.31.0"),sQuery(id+"F0.wireOp",EDGE,"E12.7.31.0"),sQuery(id+"F0.wireOp",EDGE,"E12.11.31.0"),sQuery(id+"F0.wireOp",EDGE,"E12.15.31.0"),sQuery(id+"F0.wireOp",EDGE,"E12.18.31.0"),sQuery(id+"F0.wireOp",EDGE,"E12.21.31.0"),sQuery(id+"F0.wireOp",EDGE,"E12.25.31.0"),sQuery(id+"F0.wireOp",EDGE,"E12.29.31.0"),sQuery(id+"F0.wireOp",EDGE,"E12.32.31.0"),sQuery(id+"F0.wireOp",EDGE,"E12.2.32.0"),sQuery(id+"F0.wireOp",EDGE,"E12.4.32.0"),sQuery(id+"F0.wireOp",EDGE,"E12.7.32.0"),sQuery(id+"F0.wireOp",EDGE,"E12.11.32.0"),sQuery(id+"F0.wireOp",EDGE,"E12.15.32.0"),sQuery(id+"F0.wireOp",EDGE,"E12.18.32.0"),sQuery(id+"F0.wireOp",EDGE,"E12.21.32.0"),sQuery(id+"F0.wireOp",EDGE,"E12.25.32.0"),sQuery(id+"F0.wireOp",EDGE,"E12.29.32.0"),sQuery(id+"F0.wireOp",EDGE,"E12.32.32.0"),sQuery(id+"F0.wireOp",EDGE,"E12.2.33.0"),sQuery(id+"F0.wireOp",EDGE,"E12.4.33.0"),sQuery(id+"F0.wireOp",EDGE,"E12.7.33.0"),sQuery(id+"F0.wireOp",EDGE,"E12.11.33.0"),sQuery(id+"F0.wireOp",EDGE,"E12.15.33.0"),sQuery(id+"F0.wireOp",EDGE,"E12.18.33.0"),sQuery(id+"F0.wireOp",EDGE,"E12.21.33.0"),sQuery(id+"F0.wireOp",EDGE,"E12.25.33.0"),sQuery(id+"F0.wireOp",EDGE,"E12.29.33.0"),sQuery(id+"F0.wireOp",EDGE,"E12.32.33.0"),sQuery(id+"F0.wireOp",EDGE,"E12.2.34.0"),sQuery(id+"F0.wireOp",EDGE,"E12.4.34.0"),sQuery(id+"F0.wireOp",EDGE,"E12.7.34.0"),sQuery(id+"F0.wireOp",EDGE,"E12.11.34.0"),sQuery(id+"F0.wireOp",EDGE,"E12.15.34.0"),sQuery(id+"F0.wireOp",EDGE,"E12.18.34.0"),sQuery(id+"F0.wireOp",EDGE,"E12.21.34.0"),sQuery(id+"F0.wireOp",EDGE,"E12.25.34.0"),sQuery(id+"F0.wireOp",EDGE,"E12.29.34.0"),sQuery(id+"F0.wireOp",EDGE,"E12.32.34.0"),sQuery(id+"F0.wireOp",EDGE,"E12.2.35.0"),sQuery(id+"F0.wireOp",EDGE,"E12.4.35.0"),sQuery(id+"F0.wireOp",EDGE,"E12.7.35.0"),sQuery(id+"F0.wireOp",EDGE,"E12.11.35.0"),sQuery(id+"F0.wireOp",EDGE,"E12.15.35.0"),sQuery(id+"F0.wireOp",EDGE,"E12.18.35.0"),sQuery(id+"F0.wireOp",EDGE,"E12.21.35.0"),sQuery(id+"F0.wireOp",EDGE,"E12.25.35.0"),sQuery(id+"F0.wireOp",EDGE,"E12.29.35.0"),sQuery(id+"F0.wireOp",EDGE,"E12.32.35.0"),sQuery(id+"F0.wireOp",EDGE,"E13.trimOffspring"),sQuery(id+"F0.wireOp",EDGE,"E14.trimOffspring"),sQuery(id+"F0.wireOp",EDGE,"E15.trimOffspring"),sQuery(id+"F0.wireOp",EDGE,"E16.trimOffspring"),sQuery(id+"F0.wireOp",EDGE,"E17.trimOffspring"),sQuery(id+"F0.wireOp",EDGE,"E18.trimOffspring"),sQuery(id+"F0.wireOp",EDGE,"E19.trimOffspring"),sQuery(id+"F0.wireOp",EDGE,"E20.trimOffspring"),sQuery(id+"F0.wireOp",EDGE,"E21.trimOffspring"),sQuery(id+"F0.wireOp",EDGE,"E22.trimOffspring"),sQuery(id+"F0.wireOp",EDGE,"E23.trimOffspring"),sQuery(id+"F0.wireOp",EDGE,"E24.trimOffspring"),sQuery(id+"F0.wireOp",EDGE,"E25.trimOffspring"),sQuery(id+"F0.wireOp",EDGE,"E26.trimOffspring"),sQuery(id+"F0.wireOp",EDGE,"E27.trimOffspring"),sQuery(id+"F0.wireOp",EDGE,"E28.trimOffspring"),sQuery(id+"F0.wireOp",EDGE,"E29.trimOffspring"),sQuery(id+"F0.wireOp",EDGE,"E30.trimOffspring"),sQuery(id+"F0.wireOp",EDGE,"E31.trimOffspring"),sQuery(id+"F0.wireOp",EDGE,"E32.trimOffspring"),sQuery(id+"F0.wireOp",EDGE,"E33.trimOffspring"),sQuery(id+"F0.wireOp",EDGE,"E34.trimOffspring"),sQuery(id+"F0.wireOp",EDGE,"E35.trimOffspring"),sQuery(id+"F0.wireOp",EDGE,"E36.trimOffspring"),sQuery(id+"F0.wireOp",EDGE,"E37.trimOffspring"),sQuery(id+"F0.wireOp",EDGE,"E38.trimOffspring"),sQuery(id+"F0.wireOp",EDGE,"E39.trimOffspring"),sQuery(id+"F0.wireOp",EDGE,"E40.trimOffspring"),sQuery(id+"F0.wireOp",EDGE,"E41.trimOffspring"),sQuery(id+"F0.wireOp",EDGE,"E42.trimOffspring"),sQuery(id+"F0.wireOp",EDGE,"E43.trimOffspring"),sQuery(id+"F0.wireOp",EDGE,"E44.trimOffspring"),sQuery(id+"F0.wireOp",EDGE,"E45.trimOffspring"),sQuery(id+"F0.wireOp",EDGE,"E46.trimOffspring"),sQuery(id+"F0.wireOp",EDGE,"E47.trimOffspring")])],"isStart":true}),makeQuery(id+"F8.hole-0.opRevolve","SWEPT_FACE",FACE,{"disambiguationData":[OSD([sQuery(id+"F8.hole-0.sketch.wireOp",EDGE,"core_line_2")])]})]});
            var Q17;
            Q17=makeQuery(id+"F7.hole-5.boolean.opBoolean","INTERSECT",EDGE,{"derivedFrom":[makeQuery(id+"F1.opExtrude","CAP_FACE",FACE,{"disambiguationData":[OSD([sQuery(id+"F0.wireOp",EDGE,"E0"),sQuery(id+"F0.wireOp",EDGE,"E1.trimOffspring"),sQuery(id+"F0.wireOp",EDGE,"E2"),sQuery(id+"F0.wireOp",EDGE,"E3"),sQuery(id+"F0.wireOp",EDGE,"E4.MirrorCS"),sQuery(id+"F0.wireOp",EDGE,"E5.MirrorCS"),sQuery(id+"F0.wireOp",EDGE,"E6.MirrorCS"),sQuery(id+"F0.wireOp",EDGE,"E7.filletArc"),sQuery(id+"F0.wireOp",EDGE,"E8.filletArc"),sQuery(id+"F0.wireOp",EDGE,"E9.filletArc"),sQuery(id+"F0.wireOp",EDGE,"E10.filletArc"),sQuery(id+"F0.wireOp",EDGE,"E11.1.0"),sQuery(id+"F0.wireOp",EDGE,"E11.1.1"),sQuery(id+"F0.wireOp",EDGE,"E11.1.2"),sQuery(id+"F0.wireOp",EDGE,"E11.1.3"),sQuery(id+"F0.wireOp",EDGE,"E11.1.4"),sQuery(id+"F0.wireOp",EDGE,"E11.1.5"),sQuery(id+"F0.wireOp",EDGE,"E11.1.6"),sQuery(id+"F0.wireOp",EDGE,"E11.1.7"),sQuery(id+"F0.wireOp",EDGE,"E11.1.8"),sQuery(id+"F0.wireOp",EDGE,"E11.1.9"),sQuery(id+"F0.wireOp",EDGE,"E11.2.0"),sQuery(id+"F0.wireOp",EDGE,"E11.2.1"),sQuery(id+"F0.wireOp",EDGE,"E11.2.2"),sQuery(id+"F0.wireOp",EDGE,"E11.2.3"),sQuery(id+"F0.wireOp",EDGE,"E11.2.4"),sQuery(id+"F0.wireOp",EDGE,"E11.2.5"),sQuery(id+"F0.wireOp",EDGE,"E11.2.6"),sQuery(id+"F0.wireOp",EDGE,"E11.2.7"),sQuery(id+"F0.wireOp",EDGE,"E11.2.8"),sQuery(id+"F0.wireOp",EDGE,"E11.2.9"),sQuery(id+"F0.wireOp",EDGE,"E12.2.3.0"),sQuery(id+"F0.wireOp",EDGE,"E12.4.3.0"),sQuery(id+"F0.wireOp",EDGE,"E12.7.3.0"),sQuery(id+"F0.wireOp",EDGE,"E12.11.3.0"),sQuery(id+"F0.wireOp",EDGE,"E12.15.3.0"),sQuery(id+"F0.wireOp",EDGE,"E12.18.3.0"),sQuery(id+"F0.wireOp",EDGE,"E12.21.3.0"),sQuery(id+"F0.wireOp",EDGE,"E12.25.3.0"),sQuery(id+"F0.wireOp",EDGE,"E12.29.3.0"),sQuery(id+"F0.wireOp",EDGE,"E12.32.3.0"),sQuery(id+"F0.wireOp",EDGE,"E12.2.4.0"),sQuery(id+"F0.wireOp",EDGE,"E12.4.4.0"),sQuery(id+"F0.wireOp",EDGE,"E12.7.4.0"),sQuery(id+"F0.wireOp",EDGE,"E12.11.4.0"),sQuery(id+"F0.wireOp",EDGE,"E12.15.4.0"),sQuery(id+"F0.wireOp",EDGE,"E12.18.4.0"),sQuery(id+"F0.wireOp",EDGE,"E12.21.4.0"),sQuery(id+"F0.wireOp",EDGE,"E12.25.4.0"),sQuery(id+"F0.wireOp",EDGE,"E12.29.4.0"),sQuery(id+"F0.wireOp",EDGE,"E12.32.4.0"),sQuery(id+"F0.wireOp",EDGE,"E12.2.5.0"),sQuery(id+"F0.wireOp",EDGE,"E12.4.5.0"),sQuery(id+"F0.wireOp",EDGE,"E12.7.5.0"),sQuery(id+"F0.wireOp",EDGE,"E12.11.5.0"),sQuery(id+"F0.wireOp",EDGE,"E12.15.5.0"),sQuery(id+"F0.wireOp",EDGE,"E12.18.5.0"),sQuery(id+"F0.wireOp",EDGE,"E12.21.5.0"),sQuery(id+"F0.wireOp",EDGE,"E12.25.5.0"),sQuery(id+"F0.wireOp",EDGE,"E12.29.5.0"),sQuery(id+"F0.wireOp",EDGE,"E12.32.5.0"),sQuery(id+"F0.wireOp",EDGE,"E12.2.6.0"),sQuery(id+"F0.wireOp",EDGE,"E12.4.6.0"),sQuery(id+"F0.wireOp",EDGE,"E12.7.6.0"),sQuery(id+"F0.wireOp",EDGE,"E12.11.6.0"),sQuery(id+"F0.wireOp",EDGE,"E12.15.6.0"),sQuery(id+"F0.wireOp",EDGE,"E12.18.6.0"),sQuery(id+"F0.wireOp",EDGE,"E12.21.6.0"),sQuery(id+"F0.wireOp",EDGE,"E12.25.6.0"),sQuery(id+"F0.wireOp",EDGE,"E12.29.6.0"),sQuery(id+"F0.wireOp",EDGE,"E12.32.6.0"),sQuery(id+"F0.wireOp",EDGE,"E12.2.7.0"),sQuery(id+"F0.wireOp",EDGE,"E12.4.7.0"),sQuery(id+"F0.wireOp",EDGE,"E12.7.7.0"),sQuery(id+"F0.wireOp",EDGE,"E12.11.7.0"),sQuery(id+"F0.wireOp",EDGE,"E12.15.7.0"),sQuery(id+"F0.wireOp",EDGE,"E12.18.7.0"),sQuery(id+"F0.wireOp",EDGE,"E12.21.7.0"),sQuery(id+"F0.wireOp",EDGE,"E12.25.7.0"),sQuery(id+"F0.wireOp",EDGE,"E12.29.7.0"),sQuery(id+"F0.wireOp",EDGE,"E12.32.7.0"),sQuery(id+"F0.wireOp",EDGE,"E12.2.8.0"),sQuery(id+"F0.wireOp",EDGE,"E12.4.8.0"),sQuery(id+"F0.wireOp",EDGE,"E12.7.8.0"),sQuery(id+"F0.wireOp",EDGE,"E12.11.8.0"),sQuery(id+"F0.wireOp",EDGE,"E12.15.8.0"),sQuery(id+"F0.wireOp",EDGE,"E12.18.8.0"),sQuery(id+"F0.wireOp",EDGE,"E12.21.8.0"),sQuery(id+"F0.wireOp",EDGE,"E12.25.8.0"),sQuery(id+"F0.wireOp",EDGE,"E12.29.8.0"),sQuery(id+"F0.wireOp",EDGE,"E12.32.8.0"),sQuery(id+"F0.wireOp",EDGE,"E12.2.9.0"),sQuery(id+"F0.wireOp",EDGE,"E12.4.9.0"),sQuery(id+"F0.wireOp",EDGE,"E12.7.9.0"),sQuery(id+"F0.wireOp",EDGE,"E12.11.9.0"),sQuery(id+"F0.wireOp",EDGE,"E12.15.9.0"),sQuery(id+"F0.wireOp",EDGE,"E12.18.9.0"),sQuery(id+"F0.wireOp",EDGE,"E12.21.9.0"),sQuery(id+"F0.wireOp",EDGE,"E12.25.9.0"),sQuery(id+"F0.wireOp",EDGE,"E12.29.9.0"),sQuery(id+"F0.wireOp",EDGE,"E12.32.9.0"),sQuery(id+"F0.wireOp",EDGE,"E12.2.10.0"),sQuery(id+"F0.wireOp",EDGE,"E12.4.10.0"),sQuery(id+"F0.wireOp",EDGE,"E12.7.10.0"),sQuery(id+"F0.wireOp",EDGE,"E12.11.10.0"),sQuery(id+"F0.wireOp",EDGE,"E12.15.10.0"),sQuery(id+"F0.wireOp",EDGE,"E12.18.10.0"),sQuery(id+"F0.wireOp",EDGE,"E12.21.10.0"),sQuery(id+"F0.wireOp",EDGE,"E12.25.10.0"),sQuery(id+"F0.wireOp",EDGE,"E12.29.10.0"),sQuery(id+"F0.wireOp",EDGE,"E12.32.10.0"),sQuery(id+"F0.wireOp",EDGE,"E12.2.11.0"),sQuery(id+"F0.wireOp",EDGE,"E12.4.11.0"),sQuery(id+"F0.wireOp",EDGE,"E12.7.11.0"),sQuery(id+"F0.wireOp",EDGE,"E12.11.11.0"),sQuery(id+"F0.wireOp",EDGE,"E12.15.11.0"),sQuery(id+"F0.wireOp",EDGE,"E12.18.11.0"),sQuery(id+"F0.wireOp",EDGE,"E12.21.11.0"),sQuery(id+"F0.wireOp",EDGE,"E12.25.11.0"),sQuery(id+"F0.wireOp",EDGE,"E12.29.11.0"),sQuery(id+"F0.wireOp",EDGE,"E12.32.11.0"),sQuery(id+"F0.wireOp",EDGE,"E12.2.12.0"),sQuery(id+"F0.wireOp",EDGE,"E12.4.12.0"),sQuery(id+"F0.wireOp",EDGE,"E12.7.12.0"),sQuery(id+"F0.wireOp",EDGE,"E12.11.12.0"),sQuery(id+"F0.wireOp",EDGE,"E12.15.12.0"),sQuery(id+"F0.wireOp",EDGE,"E12.18.12.0"),sQuery(id+"F0.wireOp",EDGE,"E12.21.12.0"),sQuery(id+"F0.wireOp",EDGE,"E12.25.12.0"),sQuery(id+"F0.wireOp",EDGE,"E12.29.12.0"),sQuery(id+"F0.wireOp",EDGE,"E12.32.12.0"),sQuery(id+"F0.wireOp",EDGE,"E12.2.13.0"),sQuery(id+"F0.wireOp",EDGE,"E12.4.13.0"),sQuery(id+"F0.wireOp",EDGE,"E12.7.13.0"),sQuery(id+"F0.wireOp",EDGE,"E12.11.13.0"),sQuery(id+"F0.wireOp",EDGE,"E12.15.13.0"),sQuery(id+"F0.wireOp",EDGE,"E12.18.13.0"),sQuery(id+"F0.wireOp",EDGE,"E12.21.13.0"),sQuery(id+"F0.wireOp",EDGE,"E12.25.13.0"),sQuery(id+"F0.wireOp",EDGE,"E12.29.13.0"),sQuery(id+"F0.wireOp",EDGE,"E12.32.13.0"),sQuery(id+"F0.wireOp",EDGE,"E12.2.14.0"),sQuery(id+"F0.wireOp",EDGE,"E12.4.14.0"),sQuery(id+"F0.wireOp",EDGE,"E12.7.14.0"),sQuery(id+"F0.wireOp",EDGE,"E12.11.14.0"),sQuery(id+"F0.wireOp",EDGE,"E12.15.14.0"),sQuery(id+"F0.wireOp",EDGE,"E12.18.14.0"),sQuery(id+"F0.wireOp",EDGE,"E12.21.14.0"),sQuery(id+"F0.wireOp",EDGE,"E12.25.14.0"),sQuery(id+"F0.wireOp",EDGE,"E12.29.14.0"),sQuery(id+"F0.wireOp",EDGE,"E12.32.14.0"),sQuery(id+"F0.wireOp",EDGE,"E12.2.15.0"),sQuery(id+"F0.wireOp",EDGE,"E12.4.15.0"),sQuery(id+"F0.wireOp",EDGE,"E12.7.15.0"),sQuery(id+"F0.wireOp",EDGE,"E12.11.15.0"),sQuery(id+"F0.wireOp",EDGE,"E12.15.15.0"),sQuery(id+"F0.wireOp",EDGE,"E12.18.15.0"),sQuery(id+"F0.wireOp",EDGE,"E12.21.15.0"),sQuery(id+"F0.wireOp",EDGE,"E12.25.15.0"),sQuery(id+"F0.wireOp",EDGE,"E12.29.15.0"),sQuery(id+"F0.wireOp",EDGE,"E12.32.15.0"),sQuery(id+"F0.wireOp",EDGE,"E12.2.16.0"),sQuery(id+"F0.wireOp",EDGE,"E12.4.16.0"),sQuery(id+"F0.wireOp",EDGE,"E12.7.16.0"),sQuery(id+"F0.wireOp",EDGE,"E12.11.16.0"),sQuery(id+"F0.wireOp",EDGE,"E12.15.16.0"),sQuery(id+"F0.wireOp",EDGE,"E12.18.16.0"),sQuery(id+"F0.wireOp",EDGE,"E12.21.16.0"),sQuery(id+"F0.wireOp",EDGE,"E12.25.16.0"),sQuery(id+"F0.wireOp",EDGE,"E12.29.16.0"),sQuery(id+"F0.wireOp",EDGE,"E12.32.16.0"),sQuery(id+"F0.wireOp",EDGE,"E12.2.17.0"),sQuery(id+"F0.wireOp",EDGE,"E12.4.17.0"),sQuery(id+"F0.wireOp",EDGE,"E12.7.17.0"),sQuery(id+"F0.wireOp",EDGE,"E12.11.17.0"),sQuery(id+"F0.wireOp",EDGE,"E12.15.17.0"),sQuery(id+"F0.wireOp",EDGE,"E12.18.17.0"),sQuery(id+"F0.wireOp",EDGE,"E12.21.17.0"),sQuery(id+"F0.wireOp",EDGE,"E12.25.17.0"),sQuery(id+"F0.wireOp",EDGE,"E12.29.17.0"),sQuery(id+"F0.wireOp",EDGE,"E12.32.17.0"),sQuery(id+"F0.wireOp",EDGE,"E12.2.18.0"),sQuery(id+"F0.wireOp",EDGE,"E12.4.18.0"),sQuery(id+"F0.wireOp",EDGE,"E12.7.18.0"),sQuery(id+"F0.wireOp",EDGE,"E12.11.18.0"),sQuery(id+"F0.wireOp",EDGE,"E12.15.18.0"),sQuery(id+"F0.wireOp",EDGE,"E12.18.18.0"),sQuery(id+"F0.wireOp",EDGE,"E12.21.18.0"),sQuery(id+"F0.wireOp",EDGE,"E12.25.18.0"),sQuery(id+"F0.wireOp",EDGE,"E12.29.18.0"),sQuery(id+"F0.wireOp",EDGE,"E12.32.18.0"),sQuery(id+"F0.wireOp",EDGE,"E12.2.19.0"),sQuery(id+"F0.wireOp",EDGE,"E12.4.19.0"),sQuery(id+"F0.wireOp",EDGE,"E12.7.19.0"),sQuery(id+"F0.wireOp",EDGE,"E12.11.19.0"),sQuery(id+"F0.wireOp",EDGE,"E12.15.19.0"),sQuery(id+"F0.wireOp",EDGE,"E12.18.19.0"),sQuery(id+"F0.wireOp",EDGE,"E12.21.19.0"),sQuery(id+"F0.wireOp",EDGE,"E12.25.19.0"),sQuery(id+"F0.wireOp",EDGE,"E12.29.19.0"),sQuery(id+"F0.wireOp",EDGE,"E12.32.19.0"),sQuery(id+"F0.wireOp",EDGE,"E12.2.20.0"),sQuery(id+"F0.wireOp",EDGE,"E12.4.20.0"),sQuery(id+"F0.wireOp",EDGE,"E12.7.20.0"),sQuery(id+"F0.wireOp",EDGE,"E12.11.20.0"),sQuery(id+"F0.wireOp",EDGE,"E12.15.20.0"),sQuery(id+"F0.wireOp",EDGE,"E12.18.20.0"),sQuery(id+"F0.wireOp",EDGE,"E12.21.20.0"),sQuery(id+"F0.wireOp",EDGE,"E12.25.20.0"),sQuery(id+"F0.wireOp",EDGE,"E12.29.20.0"),sQuery(id+"F0.wireOp",EDGE,"E12.32.20.0"),sQuery(id+"F0.wireOp",EDGE,"E12.2.21.0"),sQuery(id+"F0.wireOp",EDGE,"E12.4.21.0"),sQuery(id+"F0.wireOp",EDGE,"E12.7.21.0"),sQuery(id+"F0.wireOp",EDGE,"E12.11.21.0"),sQuery(id+"F0.wireOp",EDGE,"E12.15.21.0"),sQuery(id+"F0.wireOp",EDGE,"E12.18.21.0"),sQuery(id+"F0.wireOp",EDGE,"E12.21.21.0"),sQuery(id+"F0.wireOp",EDGE,"E12.25.21.0"),sQuery(id+"F0.wireOp",EDGE,"E12.29.21.0"),sQuery(id+"F0.wireOp",EDGE,"E12.32.21.0"),sQuery(id+"F0.wireOp",EDGE,"E12.2.22.0"),sQuery(id+"F0.wireOp",EDGE,"E12.4.22.0"),sQuery(id+"F0.wireOp",EDGE,"E12.7.22.0"),sQuery(id+"F0.wireOp",EDGE,"E12.11.22.0"),sQuery(id+"F0.wireOp",EDGE,"E12.15.22.0"),sQuery(id+"F0.wireOp",EDGE,"E12.18.22.0"),sQuery(id+"F0.wireOp",EDGE,"E12.21.22.0"),sQuery(id+"F0.wireOp",EDGE,"E12.25.22.0"),sQuery(id+"F0.wireOp",EDGE,"E12.29.22.0"),sQuery(id+"F0.wireOp",EDGE,"E12.32.22.0"),sQuery(id+"F0.wireOp",EDGE,"E12.2.23.0"),sQuery(id+"F0.wireOp",EDGE,"E12.4.23.0"),sQuery(id+"F0.wireOp",EDGE,"E12.7.23.0"),sQuery(id+"F0.wireOp",EDGE,"E12.11.23.0"),sQuery(id+"F0.wireOp",EDGE,"E12.15.23.0"),sQuery(id+"F0.wireOp",EDGE,"E12.18.23.0"),sQuery(id+"F0.wireOp",EDGE,"E12.21.23.0"),sQuery(id+"F0.wireOp",EDGE,"E12.25.23.0"),sQuery(id+"F0.wireOp",EDGE,"E12.29.23.0"),sQuery(id+"F0.wireOp",EDGE,"E12.32.23.0"),sQuery(id+"F0.wireOp",EDGE,"E12.2.24.0"),sQuery(id+"F0.wireOp",EDGE,"E12.4.24.0"),sQuery(id+"F0.wireOp",EDGE,"E12.7.24.0"),sQuery(id+"F0.wireOp",EDGE,"E12.11.24.0"),sQuery(id+"F0.wireOp",EDGE,"E12.15.24.0"),sQuery(id+"F0.wireOp",EDGE,"E12.18.24.0"),sQuery(id+"F0.wireOp",EDGE,"E12.21.24.0"),sQuery(id+"F0.wireOp",EDGE,"E12.25.24.0"),sQuery(id+"F0.wireOp",EDGE,"E12.29.24.0"),sQuery(id+"F0.wireOp",EDGE,"E12.32.24.0"),sQuery(id+"F0.wireOp",EDGE,"E12.2.25.0"),sQuery(id+"F0.wireOp",EDGE,"E12.4.25.0"),sQuery(id+"F0.wireOp",EDGE,"E12.7.25.0"),sQuery(id+"F0.wireOp",EDGE,"E12.11.25.0"),sQuery(id+"F0.wireOp",EDGE,"E12.15.25.0"),sQuery(id+"F0.wireOp",EDGE,"E12.18.25.0"),sQuery(id+"F0.wireOp",EDGE,"E12.21.25.0"),sQuery(id+"F0.wireOp",EDGE,"E12.25.25.0"),sQuery(id+"F0.wireOp",EDGE,"E12.29.25.0"),sQuery(id+"F0.wireOp",EDGE,"E12.32.25.0"),sQuery(id+"F0.wireOp",EDGE,"E12.2.26.0"),sQuery(id+"F0.wireOp",EDGE,"E12.4.26.0"),sQuery(id+"F0.wireOp",EDGE,"E12.7.26.0"),sQuery(id+"F0.wireOp",EDGE,"E12.11.26.0"),sQuery(id+"F0.wireOp",EDGE,"E12.15.26.0"),sQuery(id+"F0.wireOp",EDGE,"E12.18.26.0"),sQuery(id+"F0.wireOp",EDGE,"E12.21.26.0"),sQuery(id+"F0.wireOp",EDGE,"E12.25.26.0"),sQuery(id+"F0.wireOp",EDGE,"E12.29.26.0"),sQuery(id+"F0.wireOp",EDGE,"E12.32.26.0"),sQuery(id+"F0.wireOp",EDGE,"E12.2.27.0"),sQuery(id+"F0.wireOp",EDGE,"E12.4.27.0"),sQuery(id+"F0.wireOp",EDGE,"E12.7.27.0"),sQuery(id+"F0.wireOp",EDGE,"E12.11.27.0"),sQuery(id+"F0.wireOp",EDGE,"E12.15.27.0"),sQuery(id+"F0.wireOp",EDGE,"E12.18.27.0"),sQuery(id+"F0.wireOp",EDGE,"E12.21.27.0"),sQuery(id+"F0.wireOp",EDGE,"E12.25.27.0"),sQuery(id+"F0.wireOp",EDGE,"E12.29.27.0"),sQuery(id+"F0.wireOp",EDGE,"E12.32.27.0"),sQuery(id+"F0.wireOp",EDGE,"E12.2.28.0"),sQuery(id+"F0.wireOp",EDGE,"E12.4.28.0"),sQuery(id+"F0.wireOp",EDGE,"E12.7.28.0"),sQuery(id+"F0.wireOp",EDGE,"E12.11.28.0"),sQuery(id+"F0.wireOp",EDGE,"E12.15.28.0"),sQuery(id+"F0.wireOp",EDGE,"E12.18.28.0"),sQuery(id+"F0.wireOp",EDGE,"E12.21.28.0"),sQuery(id+"F0.wireOp",EDGE,"E12.25.28.0"),sQuery(id+"F0.wireOp",EDGE,"E12.29.28.0"),sQuery(id+"F0.wireOp",EDGE,"E12.32.28.0"),sQuery(id+"F0.wireOp",EDGE,"E12.2.29.0"),sQuery(id+"F0.wireOp",EDGE,"E12.4.29.0"),sQuery(id+"F0.wireOp",EDGE,"E12.7.29.0"),sQuery(id+"F0.wireOp",EDGE,"E12.11.29.0"),sQuery(id+"F0.wireOp",EDGE,"E12.15.29.0"),sQuery(id+"F0.wireOp",EDGE,"E12.18.29.0"),sQuery(id+"F0.wireOp",EDGE,"E12.21.29.0"),sQuery(id+"F0.wireOp",EDGE,"E12.25.29.0"),sQuery(id+"F0.wireOp",EDGE,"E12.29.29.0"),sQuery(id+"F0.wireOp",EDGE,"E12.32.29.0"),sQuery(id+"F0.wireOp",EDGE,"E12.2.30.0"),sQuery(id+"F0.wireOp",EDGE,"E12.4.30.0"),sQuery(id+"F0.wireOp",EDGE,"E12.7.30.0"),sQuery(id+"F0.wireOp",EDGE,"E12.11.30.0"),sQuery(id+"F0.wireOp",EDGE,"E12.15.30.0"),sQuery(id+"F0.wireOp",EDGE,"E12.18.30.0"),sQuery(id+"F0.wireOp",EDGE,"E12.21.30.0"),sQuery(id+"F0.wireOp",EDGE,"E12.25.30.0"),sQuery(id+"F0.wireOp",EDGE,"E12.29.30.0"),sQuery(id+"F0.wireOp",EDGE,"E12.32.30.0"),sQuery(id+"F0.wireOp",EDGE,"E12.2.31.0"),sQuery(id+"F0.wireOp",EDGE,"E12.4.31.0"),sQuery(id+"F0.wireOp",EDGE,"E12.7.31.0"),sQuery(id+"F0.wireOp",EDGE,"E12.11.31.0"),sQuery(id+"F0.wireOp",EDGE,"E12.15.31.0"),sQuery(id+"F0.wireOp",EDGE,"E12.18.31.0"),sQuery(id+"F0.wireOp",EDGE,"E12.21.31.0"),sQuery(id+"F0.wireOp",EDGE,"E12.25.31.0"),sQuery(id+"F0.wireOp",EDGE,"E12.29.31.0"),sQuery(id+"F0.wireOp",EDGE,"E12.32.31.0"),sQuery(id+"F0.wireOp",EDGE,"E12.2.32.0"),sQuery(id+"F0.wireOp",EDGE,"E12.4.32.0"),sQuery(id+"F0.wireOp",EDGE,"E12.7.32.0"),sQuery(id+"F0.wireOp",EDGE,"E12.11.32.0"),sQuery(id+"F0.wireOp",EDGE,"E12.15.32.0"),sQuery(id+"F0.wireOp",EDGE,"E12.18.32.0"),sQuery(id+"F0.wireOp",EDGE,"E12.21.32.0"),sQuery(id+"F0.wireOp",EDGE,"E12.25.32.0"),sQuery(id+"F0.wireOp",EDGE,"E12.29.32.0"),sQuery(id+"F0.wireOp",EDGE,"E12.32.32.0"),sQuery(id+"F0.wireOp",EDGE,"E12.2.33.0"),sQuery(id+"F0.wireOp",EDGE,"E12.4.33.0"),sQuery(id+"F0.wireOp",EDGE,"E12.7.33.0"),sQuery(id+"F0.wireOp",EDGE,"E12.11.33.0"),sQuery(id+"F0.wireOp",EDGE,"E12.15.33.0"),sQuery(id+"F0.wireOp",EDGE,"E12.18.33.0"),sQuery(id+"F0.wireOp",EDGE,"E12.21.33.0"),sQuery(id+"F0.wireOp",EDGE,"E12.25.33.0"),sQuery(id+"F0.wireOp",EDGE,"E12.29.33.0"),sQuery(id+"F0.wireOp",EDGE,"E12.32.33.0"),sQuery(id+"F0.wireOp",EDGE,"E12.2.34.0"),sQuery(id+"F0.wireOp",EDGE,"E12.4.34.0"),sQuery(id+"F0.wireOp",EDGE,"E12.7.34.0"),sQuery(id+"F0.wireOp",EDGE,"E12.11.34.0"),sQuery(id+"F0.wireOp",EDGE,"E12.15.34.0"),sQuery(id+"F0.wireOp",EDGE,"E12.18.34.0"),sQuery(id+"F0.wireOp",EDGE,"E12.21.34.0"),sQuery(id+"F0.wireOp",EDGE,"E12.25.34.0"),sQuery(id+"F0.wireOp",EDGE,"E12.29.34.0"),sQuery(id+"F0.wireOp",EDGE,"E12.32.34.0"),sQuery(id+"F0.wireOp",EDGE,"E12.2.35.0"),sQuery(id+"F0.wireOp",EDGE,"E12.4.35.0"),sQuery(id+"F0.wireOp",EDGE,"E12.7.35.0"),sQuery(id+"F0.wireOp",EDGE,"E12.11.35.0"),sQuery(id+"F0.wireOp",EDGE,"E12.15.35.0"),sQuery(id+"F0.wireOp",EDGE,"E12.18.35.0"),sQuery(id+"F0.wireOp",EDGE,"E12.21.35.0"),sQuery(id+"F0.wireOp",EDGE,"E12.25.35.0"),sQuery(id+"F0.wireOp",EDGE,"E12.29.35.0"),sQuery(id+"F0.wireOp",EDGE,"E12.32.35.0"),sQuery(id+"F0.wireOp",EDGE,"E13.trimOffspring"),sQuery(id+"F0.wireOp",EDGE,"E14.trimOffspring"),sQuery(id+"F0.wireOp",EDGE,"E15.trimOffspring"),sQuery(id+"F0.wireOp",EDGE,"E16.trimOffspring"),sQuery(id+"F0.wireOp",EDGE,"E17.trimOffspring"),sQuery(id+"F0.wireOp",EDGE,"E18.trimOffspring"),sQuery(id+"F0.wireOp",EDGE,"E19.trimOffspring"),sQuery(id+"F0.wireOp",EDGE,"E20.trimOffspring"),sQuery(id+"F0.wireOp",EDGE,"E21.trimOffspring"),sQuery(id+"F0.wireOp",EDGE,"E22.trimOffspring"),sQuery(id+"F0.wireOp",EDGE,"E23.trimOffspring"),sQuery(id+"F0.wireOp",EDGE,"E24.trimOffspring"),sQuery(id+"F0.wireOp",EDGE,"E25.trimOffspring"),sQuery(id+"F0.wireOp",EDGE,"E26.trimOffspring"),sQuery(id+"F0.wireOp",EDGE,"E27.trimOffspring"),sQuery(id+"F0.wireOp",EDGE,"E28.trimOffspring"),sQuery(id+"F0.wireOp",EDGE,"E29.trimOffspring"),sQuery(id+"F0.wireOp",EDGE,"E30.trimOffspring"),sQuery(id+"F0.wireOp",EDGE,"E31.trimOffspring"),sQuery(id+"F0.wireOp",EDGE,"E32.trimOffspring"),sQuery(id+"F0.wireOp",EDGE,"E33.trimOffspring"),sQuery(id+"F0.wireOp",EDGE,"E34.trimOffspring"),sQuery(id+"F0.wireOp",EDGE,"E35.trimOffspring"),sQuery(id+"F0.wireOp",EDGE,"E36.trimOffspring"),sQuery(id+"F0.wireOp",EDGE,"E37.trimOffspring"),sQuery(id+"F0.wireOp",EDGE,"E38.trimOffspring"),sQuery(id+"F0.wireOp",EDGE,"E39.trimOffspring"),sQuery(id+"F0.wireOp",EDGE,"E40.trimOffspring"),sQuery(id+"F0.wireOp",EDGE,"E41.trimOffspring"),sQuery(id+"F0.wireOp",EDGE,"E42.trimOffspring"),sQuery(id+"F0.wireOp",EDGE,"E43.trimOffspring"),sQuery(id+"F0.wireOp",EDGE,"E44.trimOffspring"),sQuery(id+"F0.wireOp",EDGE,"E45.trimOffspring"),sQuery(id+"F0.wireOp",EDGE,"E46.trimOffspring"),sQuery(id+"F0.wireOp",EDGE,"E47.trimOffspring")])],"isStart":true}),makeQuery(id+"F7.hole-5.opRevolve","SWEPT_FACE",FACE,{"disambiguationData":[OSD([sQuery(id+"F7.hole-5.sketch.wireOp",EDGE,"core_line_2")])]})]});
            var Q18;
            Q18=makeQuery(id+"F7.hole-5.boolean.opBoolean","COPY",EDGE,{"derivedFrom":makeQuery(id+"F7.hole-5.opRevolve","SWEPT_EDGE",EDGE,{"disambiguationData":[OSD([sQuery(id+"F7.hole-5.sketch.wireOp",EDGE,"cbore_start_line_2"),sQuery(id+"F7.hole-5.sketch.wireOp",EDGE,"cbore_start_line_3")])]})});
            var Q19;
            Q19=makeQuery(id+"F7.hole-0.boolean.opBoolean","COPY",EDGE,{"derivedFrom":makeQuery(id+"F7.hole-0.opRevolve","SWEPT_EDGE",EDGE,{"disambiguationData":[OSD([sQuery(id+"F7.hole-0.sketch.wireOp",EDGE,"cbore_start_line_2"),sQuery(id+"F7.hole-0.sketch.wireOp",EDGE,"cbore_start_line_3")])]})});
            var Q20;
            Q20=makeQuery(id+"F7.hole-0.boolean.opBoolean","INTERSECT",EDGE,{"derivedFrom":[makeQuery(id+"F1.opExtrude","CAP_FACE",FACE,{"disambiguationData":[OSD([sQuery(id+"F0.wireOp",EDGE,"E0"),sQuery(id+"F0.wireOp",EDGE,"E1.trimOffspring"),sQuery(id+"F0.wireOp",EDGE,"E2"),sQuery(id+"F0.wireOp",EDGE,"E3"),sQuery(id+"F0.wireOp",EDGE,"E4.MirrorCS"),sQuery(id+"F0.wireOp",EDGE,"E5.MirrorCS"),sQuery(id+"F0.wireOp",EDGE,"E6.MirrorCS"),sQuery(id+"F0.wireOp",EDGE,"E7.filletArc"),sQuery(id+"F0.wireOp",EDGE,"E8.filletArc"),sQuery(id+"F0.wireOp",EDGE,"E9.filletArc"),sQuery(id+"F0.wireOp",EDGE,"E10.filletArc"),sQuery(id+"F0.wireOp",EDGE,"E11.1.0"),sQuery(id+"F0.wireOp",EDGE,"E11.1.1"),sQuery(id+"F0.wireOp",EDGE,"E11.1.2"),sQuery(id+"F0.wireOp",EDGE,"E11.1.3"),sQuery(id+"F0.wireOp",EDGE,"E11.1.4"),sQuery(id+"F0.wireOp",EDGE,"E11.1.5"),sQuery(id+"F0.wireOp",EDGE,"E11.1.6"),sQuery(id+"F0.wireOp",EDGE,"E11.1.7"),sQuery(id+"F0.wireOp",EDGE,"E11.1.8"),sQuery(id+"F0.wireOp",EDGE,"E11.1.9"),sQuery(id+"F0.wireOp",EDGE,"E11.2.0"),sQuery(id+"F0.wireOp",EDGE,"E11.2.1"),sQuery(id+"F0.wireOp",EDGE,"E11.2.2"),sQuery(id+"F0.wireOp",EDGE,"E11.2.3"),sQuery(id+"F0.wireOp",EDGE,"E11.2.4"),sQuery(id+"F0.wireOp",EDGE,"E11.2.5"),sQuery(id+"F0.wireOp",EDGE,"E11.2.6"),sQuery(id+"F0.wireOp",EDGE,"E11.2.7"),sQuery(id+"F0.wireOp",EDGE,"E11.2.8"),sQuery(id+"F0.wireOp",EDGE,"E11.2.9"),sQuery(id+"F0.wireOp",EDGE,"E12.2.3.0"),sQuery(id+"F0.wireOp",EDGE,"E12.4.3.0"),sQuery(id+"F0.wireOp",EDGE,"E12.7.3.0"),sQuery(id+"F0.wireOp",EDGE,"E12.11.3.0"),sQuery(id+"F0.wireOp",EDGE,"E12.15.3.0"),sQuery(id+"F0.wireOp",EDGE,"E12.18.3.0"),sQuery(id+"F0.wireOp",EDGE,"E12.21.3.0"),sQuery(id+"F0.wireOp",EDGE,"E12.25.3.0"),sQuery(id+"F0.wireOp",EDGE,"E12.29.3.0"),sQuery(id+"F0.wireOp",EDGE,"E12.32.3.0"),sQuery(id+"F0.wireOp",EDGE,"E12.2.4.0"),sQuery(id+"F0.wireOp",EDGE,"E12.4.4.0"),sQuery(id+"F0.wireOp",EDGE,"E12.7.4.0"),sQuery(id+"F0.wireOp",EDGE,"E12.11.4.0"),sQuery(id+"F0.wireOp",EDGE,"E12.15.4.0"),sQuery(id+"F0.wireOp",EDGE,"E12.18.4.0"),sQuery(id+"F0.wireOp",EDGE,"E12.21.4.0"),sQuery(id+"F0.wireOp",EDGE,"E12.25.4.0"),sQuery(id+"F0.wireOp",EDGE,"E12.29.4.0"),sQuery(id+"F0.wireOp",EDGE,"E12.32.4.0"),sQuery(id+"F0.wireOp",EDGE,"E12.2.5.0"),sQuery(id+"F0.wireOp",EDGE,"E12.4.5.0"),sQuery(id+"F0.wireOp",EDGE,"E12.7.5.0"),sQuery(id+"F0.wireOp",EDGE,"E12.11.5.0"),sQuery(id+"F0.wireOp",EDGE,"E12.15.5.0"),sQuery(id+"F0.wireOp",EDGE,"E12.18.5.0"),sQuery(id+"F0.wireOp",EDGE,"E12.21.5.0"),sQuery(id+"F0.wireOp",EDGE,"E12.25.5.0"),sQuery(id+"F0.wireOp",EDGE,"E12.29.5.0"),sQuery(id+"F0.wireOp",EDGE,"E12.32.5.0"),sQuery(id+"F0.wireOp",EDGE,"E12.2.6.0"),sQuery(id+"F0.wireOp",EDGE,"E12.4.6.0"),sQuery(id+"F0.wireOp",EDGE,"E12.7.6.0"),sQuery(id+"F0.wireOp",EDGE,"E12.11.6.0"),sQuery(id+"F0.wireOp",EDGE,"E12.15.6.0"),sQuery(id+"F0.wireOp",EDGE,"E12.18.6.0"),sQuery(id+"F0.wireOp",EDGE,"E12.21.6.0"),sQuery(id+"F0.wireOp",EDGE,"E12.25.6.0"),sQuery(id+"F0.wireOp",EDGE,"E12.29.6.0"),sQuery(id+"F0.wireOp",EDGE,"E12.32.6.0"),sQuery(id+"F0.wireOp",EDGE,"E12.2.7.0"),sQuery(id+"F0.wireOp",EDGE,"E12.4.7.0"),sQuery(id+"F0.wireOp",EDGE,"E12.7.7.0"),sQuery(id+"F0.wireOp",EDGE,"E12.11.7.0"),sQuery(id+"F0.wireOp",EDGE,"E12.15.7.0"),sQuery(id+"F0.wireOp",EDGE,"E12.18.7.0"),sQuery(id+"F0.wireOp",EDGE,"E12.21.7.0"),sQuery(id+"F0.wireOp",EDGE,"E12.25.7.0"),sQuery(id+"F0.wireOp",EDGE,"E12.29.7.0"),sQuery(id+"F0.wireOp",EDGE,"E12.32.7.0"),sQuery(id+"F0.wireOp",EDGE,"E12.2.8.0"),sQuery(id+"F0.wireOp",EDGE,"E12.4.8.0"),sQuery(id+"F0.wireOp",EDGE,"E12.7.8.0"),sQuery(id+"F0.wireOp",EDGE,"E12.11.8.0"),sQuery(id+"F0.wireOp",EDGE,"E12.15.8.0"),sQuery(id+"F0.wireOp",EDGE,"E12.18.8.0"),sQuery(id+"F0.wireOp",EDGE,"E12.21.8.0"),sQuery(id+"F0.wireOp",EDGE,"E12.25.8.0"),sQuery(id+"F0.wireOp",EDGE,"E12.29.8.0"),sQuery(id+"F0.wireOp",EDGE,"E12.32.8.0"),sQuery(id+"F0.wireOp",EDGE,"E12.2.9.0"),sQuery(id+"F0.wireOp",EDGE,"E12.4.9.0"),sQuery(id+"F0.wireOp",EDGE,"E12.7.9.0"),sQuery(id+"F0.wireOp",EDGE,"E12.11.9.0"),sQuery(id+"F0.wireOp",EDGE,"E12.15.9.0"),sQuery(id+"F0.wireOp",EDGE,"E12.18.9.0"),sQuery(id+"F0.wireOp",EDGE,"E12.21.9.0"),sQuery(id+"F0.wireOp",EDGE,"E12.25.9.0"),sQuery(id+"F0.wireOp",EDGE,"E12.29.9.0"),sQuery(id+"F0.wireOp",EDGE,"E12.32.9.0"),sQuery(id+"F0.wireOp",EDGE,"E12.2.10.0"),sQuery(id+"F0.wireOp",EDGE,"E12.4.10.0"),sQuery(id+"F0.wireOp",EDGE,"E12.7.10.0"),sQuery(id+"F0.wireOp",EDGE,"E12.11.10.0"),sQuery(id+"F0.wireOp",EDGE,"E12.15.10.0"),sQuery(id+"F0.wireOp",EDGE,"E12.18.10.0"),sQuery(id+"F0.wireOp",EDGE,"E12.21.10.0"),sQuery(id+"F0.wireOp",EDGE,"E12.25.10.0"),sQuery(id+"F0.wireOp",EDGE,"E12.29.10.0"),sQuery(id+"F0.wireOp",EDGE,"E12.32.10.0"),sQuery(id+"F0.wireOp",EDGE,"E12.2.11.0"),sQuery(id+"F0.wireOp",EDGE,"E12.4.11.0"),sQuery(id+"F0.wireOp",EDGE,"E12.7.11.0"),sQuery(id+"F0.wireOp",EDGE,"E12.11.11.0"),sQuery(id+"F0.wireOp",EDGE,"E12.15.11.0"),sQuery(id+"F0.wireOp",EDGE,"E12.18.11.0"),sQuery(id+"F0.wireOp",EDGE,"E12.21.11.0"),sQuery(id+"F0.wireOp",EDGE,"E12.25.11.0"),sQuery(id+"F0.wireOp",EDGE,"E12.29.11.0"),sQuery(id+"F0.wireOp",EDGE,"E12.32.11.0"),sQuery(id+"F0.wireOp",EDGE,"E12.2.12.0"),sQuery(id+"F0.wireOp",EDGE,"E12.4.12.0"),sQuery(id+"F0.wireOp",EDGE,"E12.7.12.0"),sQuery(id+"F0.wireOp",EDGE,"E12.11.12.0"),sQuery(id+"F0.wireOp",EDGE,"E12.15.12.0"),sQuery(id+"F0.wireOp",EDGE,"E12.18.12.0"),sQuery(id+"F0.wireOp",EDGE,"E12.21.12.0"),sQuery(id+"F0.wireOp",EDGE,"E12.25.12.0"),sQuery(id+"F0.wireOp",EDGE,"E12.29.12.0"),sQuery(id+"F0.wireOp",EDGE,"E12.32.12.0"),sQuery(id+"F0.wireOp",EDGE,"E12.2.13.0"),sQuery(id+"F0.wireOp",EDGE,"E12.4.13.0"),sQuery(id+"F0.wireOp",EDGE,"E12.7.13.0"),sQuery(id+"F0.wireOp",EDGE,"E12.11.13.0"),sQuery(id+"F0.wireOp",EDGE,"E12.15.13.0"),sQuery(id+"F0.wireOp",EDGE,"E12.18.13.0"),sQuery(id+"F0.wireOp",EDGE,"E12.21.13.0"),sQuery(id+"F0.wireOp",EDGE,"E12.25.13.0"),sQuery(id+"F0.wireOp",EDGE,"E12.29.13.0"),sQuery(id+"F0.wireOp",EDGE,"E12.32.13.0"),sQuery(id+"F0.wireOp",EDGE,"E12.2.14.0"),sQuery(id+"F0.wireOp",EDGE,"E12.4.14.0"),sQuery(id+"F0.wireOp",EDGE,"E12.7.14.0"),sQuery(id+"F0.wireOp",EDGE,"E12.11.14.0"),sQuery(id+"F0.wireOp",EDGE,"E12.15.14.0"),sQuery(id+"F0.wireOp",EDGE,"E12.18.14.0"),sQuery(id+"F0.wireOp",EDGE,"E12.21.14.0"),sQuery(id+"F0.wireOp",EDGE,"E12.25.14.0"),sQuery(id+"F0.wireOp",EDGE,"E12.29.14.0"),sQuery(id+"F0.wireOp",EDGE,"E12.32.14.0"),sQuery(id+"F0.wireOp",EDGE,"E12.2.15.0"),sQuery(id+"F0.wireOp",EDGE,"E12.4.15.0"),sQuery(id+"F0.wireOp",EDGE,"E12.7.15.0"),sQuery(id+"F0.wireOp",EDGE,"E12.11.15.0"),sQuery(id+"F0.wireOp",EDGE,"E12.15.15.0"),sQuery(id+"F0.wireOp",EDGE,"E12.18.15.0"),sQuery(id+"F0.wireOp",EDGE,"E12.21.15.0"),sQuery(id+"F0.wireOp",EDGE,"E12.25.15.0"),sQuery(id+"F0.wireOp",EDGE,"E12.29.15.0"),sQuery(id+"F0.wireOp",EDGE,"E12.32.15.0"),sQuery(id+"F0.wireOp",EDGE,"E12.2.16.0"),sQuery(id+"F0.wireOp",EDGE,"E12.4.16.0"),sQuery(id+"F0.wireOp",EDGE,"E12.7.16.0"),sQuery(id+"F0.wireOp",EDGE,"E12.11.16.0"),sQuery(id+"F0.wireOp",EDGE,"E12.15.16.0"),sQuery(id+"F0.wireOp",EDGE,"E12.18.16.0"),sQuery(id+"F0.wireOp",EDGE,"E12.21.16.0"),sQuery(id+"F0.wireOp",EDGE,"E12.25.16.0"),sQuery(id+"F0.wireOp",EDGE,"E12.29.16.0"),sQuery(id+"F0.wireOp",EDGE,"E12.32.16.0"),sQuery(id+"F0.wireOp",EDGE,"E12.2.17.0"),sQuery(id+"F0.wireOp",EDGE,"E12.4.17.0"),sQuery(id+"F0.wireOp",EDGE,"E12.7.17.0"),sQuery(id+"F0.wireOp",EDGE,"E12.11.17.0"),sQuery(id+"F0.wireOp",EDGE,"E12.15.17.0"),sQuery(id+"F0.wireOp",EDGE,"E12.18.17.0"),sQuery(id+"F0.wireOp",EDGE,"E12.21.17.0"),sQuery(id+"F0.wireOp",EDGE,"E12.25.17.0"),sQuery(id+"F0.wireOp",EDGE,"E12.29.17.0"),sQuery(id+"F0.wireOp",EDGE,"E12.32.17.0"),sQuery(id+"F0.wireOp",EDGE,"E12.2.18.0"),sQuery(id+"F0.wireOp",EDGE,"E12.4.18.0"),sQuery(id+"F0.wireOp",EDGE,"E12.7.18.0"),sQuery(id+"F0.wireOp",EDGE,"E12.11.18.0"),sQuery(id+"F0.wireOp",EDGE,"E12.15.18.0"),sQuery(id+"F0.wireOp",EDGE,"E12.18.18.0"),sQuery(id+"F0.wireOp",EDGE,"E12.21.18.0"),sQuery(id+"F0.wireOp",EDGE,"E12.25.18.0"),sQuery(id+"F0.wireOp",EDGE,"E12.29.18.0"),sQuery(id+"F0.wireOp",EDGE,"E12.32.18.0"),sQuery(id+"F0.wireOp",EDGE,"E12.2.19.0"),sQuery(id+"F0.wireOp",EDGE,"E12.4.19.0"),sQuery(id+"F0.wireOp",EDGE,"E12.7.19.0"),sQuery(id+"F0.wireOp",EDGE,"E12.11.19.0"),sQuery(id+"F0.wireOp",EDGE,"E12.15.19.0"),sQuery(id+"F0.wireOp",EDGE,"E12.18.19.0"),sQuery(id+"F0.wireOp",EDGE,"E12.21.19.0"),sQuery(id+"F0.wireOp",EDGE,"E12.25.19.0"),sQuery(id+"F0.wireOp",EDGE,"E12.29.19.0"),sQuery(id+"F0.wireOp",EDGE,"E12.32.19.0"),sQuery(id+"F0.wireOp",EDGE,"E12.2.20.0"),sQuery(id+"F0.wireOp",EDGE,"E12.4.20.0"),sQuery(id+"F0.wireOp",EDGE,"E12.7.20.0"),sQuery(id+"F0.wireOp",EDGE,"E12.11.20.0"),sQuery(id+"F0.wireOp",EDGE,"E12.15.20.0"),sQuery(id+"F0.wireOp",EDGE,"E12.18.20.0"),sQuery(id+"F0.wireOp",EDGE,"E12.21.20.0"),sQuery(id+"F0.wireOp",EDGE,"E12.25.20.0"),sQuery(id+"F0.wireOp",EDGE,"E12.29.20.0"),sQuery(id+"F0.wireOp",EDGE,"E12.32.20.0"),sQuery(id+"F0.wireOp",EDGE,"E12.2.21.0"),sQuery(id+"F0.wireOp",EDGE,"E12.4.21.0"),sQuery(id+"F0.wireOp",EDGE,"E12.7.21.0"),sQuery(id+"F0.wireOp",EDGE,"E12.11.21.0"),sQuery(id+"F0.wireOp",EDGE,"E12.15.21.0"),sQuery(id+"F0.wireOp",EDGE,"E12.18.21.0"),sQuery(id+"F0.wireOp",EDGE,"E12.21.21.0"),sQuery(id+"F0.wireOp",EDGE,"E12.25.21.0"),sQuery(id+"F0.wireOp",EDGE,"E12.29.21.0"),sQuery(id+"F0.wireOp",EDGE,"E12.32.21.0"),sQuery(id+"F0.wireOp",EDGE,"E12.2.22.0"),sQuery(id+"F0.wireOp",EDGE,"E12.4.22.0"),sQuery(id+"F0.wireOp",EDGE,"E12.7.22.0"),sQuery(id+"F0.wireOp",EDGE,"E12.11.22.0"),sQuery(id+"F0.wireOp",EDGE,"E12.15.22.0"),sQuery(id+"F0.wireOp",EDGE,"E12.18.22.0"),sQuery(id+"F0.wireOp",EDGE,"E12.21.22.0"),sQuery(id+"F0.wireOp",EDGE,"E12.25.22.0"),sQuery(id+"F0.wireOp",EDGE,"E12.29.22.0"),sQuery(id+"F0.wireOp",EDGE,"E12.32.22.0"),sQuery(id+"F0.wireOp",EDGE,"E12.2.23.0"),sQuery(id+"F0.wireOp",EDGE,"E12.4.23.0"),sQuery(id+"F0.wireOp",EDGE,"E12.7.23.0"),sQuery(id+"F0.wireOp",EDGE,"E12.11.23.0"),sQuery(id+"F0.wireOp",EDGE,"E12.15.23.0"),sQuery(id+"F0.wireOp",EDGE,"E12.18.23.0"),sQuery(id+"F0.wireOp",EDGE,"E12.21.23.0"),sQuery(id+"F0.wireOp",EDGE,"E12.25.23.0"),sQuery(id+"F0.wireOp",EDGE,"E12.29.23.0"),sQuery(id+"F0.wireOp",EDGE,"E12.32.23.0"),sQuery(id+"F0.wireOp",EDGE,"E12.2.24.0"),sQuery(id+"F0.wireOp",EDGE,"E12.4.24.0"),sQuery(id+"F0.wireOp",EDGE,"E12.7.24.0"),sQuery(id+"F0.wireOp",EDGE,"E12.11.24.0"),sQuery(id+"F0.wireOp",EDGE,"E12.15.24.0"),sQuery(id+"F0.wireOp",EDGE,"E12.18.24.0"),sQuery(id+"F0.wireOp",EDGE,"E12.21.24.0"),sQuery(id+"F0.wireOp",EDGE,"E12.25.24.0"),sQuery(id+"F0.wireOp",EDGE,"E12.29.24.0"),sQuery(id+"F0.wireOp",EDGE,"E12.32.24.0"),sQuery(id+"F0.wireOp",EDGE,"E12.2.25.0"),sQuery(id+"F0.wireOp",EDGE,"E12.4.25.0"),sQuery(id+"F0.wireOp",EDGE,"E12.7.25.0"),sQuery(id+"F0.wireOp",EDGE,"E12.11.25.0"),sQuery(id+"F0.wireOp",EDGE,"E12.15.25.0"),sQuery(id+"F0.wireOp",EDGE,"E12.18.25.0"),sQuery(id+"F0.wireOp",EDGE,"E12.21.25.0"),sQuery(id+"F0.wireOp",EDGE,"E12.25.25.0"),sQuery(id+"F0.wireOp",EDGE,"E12.29.25.0"),sQuery(id+"F0.wireOp",EDGE,"E12.32.25.0"),sQuery(id+"F0.wireOp",EDGE,"E12.2.26.0"),sQuery(id+"F0.wireOp",EDGE,"E12.4.26.0"),sQuery(id+"F0.wireOp",EDGE,"E12.7.26.0"),sQuery(id+"F0.wireOp",EDGE,"E12.11.26.0"),sQuery(id+"F0.wireOp",EDGE,"E12.15.26.0"),sQuery(id+"F0.wireOp",EDGE,"E12.18.26.0"),sQuery(id+"F0.wireOp",EDGE,"E12.21.26.0"),sQuery(id+"F0.wireOp",EDGE,"E12.25.26.0"),sQuery(id+"F0.wireOp",EDGE,"E12.29.26.0"),sQuery(id+"F0.wireOp",EDGE,"E12.32.26.0"),sQuery(id+"F0.wireOp",EDGE,"E12.2.27.0"),sQuery(id+"F0.wireOp",EDGE,"E12.4.27.0"),sQuery(id+"F0.wireOp",EDGE,"E12.7.27.0"),sQuery(id+"F0.wireOp",EDGE,"E12.11.27.0"),sQuery(id+"F0.wireOp",EDGE,"E12.15.27.0"),sQuery(id+"F0.wireOp",EDGE,"E12.18.27.0"),sQuery(id+"F0.wireOp",EDGE,"E12.21.27.0"),sQuery(id+"F0.wireOp",EDGE,"E12.25.27.0"),sQuery(id+"F0.wireOp",EDGE,"E12.29.27.0"),sQuery(id+"F0.wireOp",EDGE,"E12.32.27.0"),sQuery(id+"F0.wireOp",EDGE,"E12.2.28.0"),sQuery(id+"F0.wireOp",EDGE,"E12.4.28.0"),sQuery(id+"F0.wireOp",EDGE,"E12.7.28.0"),sQuery(id+"F0.wireOp",EDGE,"E12.11.28.0"),sQuery(id+"F0.wireOp",EDGE,"E12.15.28.0"),sQuery(id+"F0.wireOp",EDGE,"E12.18.28.0"),sQuery(id+"F0.wireOp",EDGE,"E12.21.28.0"),sQuery(id+"F0.wireOp",EDGE,"E12.25.28.0"),sQuery(id+"F0.wireOp",EDGE,"E12.29.28.0"),sQuery(id+"F0.wireOp",EDGE,"E12.32.28.0"),sQuery(id+"F0.wireOp",EDGE,"E12.2.29.0"),sQuery(id+"F0.wireOp",EDGE,"E12.4.29.0"),sQuery(id+"F0.wireOp",EDGE,"E12.7.29.0"),sQuery(id+"F0.wireOp",EDGE,"E12.11.29.0"),sQuery(id+"F0.wireOp",EDGE,"E12.15.29.0"),sQuery(id+"F0.wireOp",EDGE,"E12.18.29.0"),sQuery(id+"F0.wireOp",EDGE,"E12.21.29.0"),sQuery(id+"F0.wireOp",EDGE,"E12.25.29.0"),sQuery(id+"F0.wireOp",EDGE,"E12.29.29.0"),sQuery(id+"F0.wireOp",EDGE,"E12.32.29.0"),sQuery(id+"F0.wireOp",EDGE,"E12.2.30.0"),sQuery(id+"F0.wireOp",EDGE,"E12.4.30.0"),sQuery(id+"F0.wireOp",EDGE,"E12.7.30.0"),sQuery(id+"F0.wireOp",EDGE,"E12.11.30.0"),sQuery(id+"F0.wireOp",EDGE,"E12.15.30.0"),sQuery(id+"F0.wireOp",EDGE,"E12.18.30.0"),sQuery(id+"F0.wireOp",EDGE,"E12.21.30.0"),sQuery(id+"F0.wireOp",EDGE,"E12.25.30.0"),sQuery(id+"F0.wireOp",EDGE,"E12.29.30.0"),sQuery(id+"F0.wireOp",EDGE,"E12.32.30.0"),sQuery(id+"F0.wireOp",EDGE,"E12.2.31.0"),sQuery(id+"F0.wireOp",EDGE,"E12.4.31.0"),sQuery(id+"F0.wireOp",EDGE,"E12.7.31.0"),sQuery(id+"F0.wireOp",EDGE,"E12.11.31.0"),sQuery(id+"F0.wireOp",EDGE,"E12.15.31.0"),sQuery(id+"F0.wireOp",EDGE,"E12.18.31.0"),sQuery(id+"F0.wireOp",EDGE,"E12.21.31.0"),sQuery(id+"F0.wireOp",EDGE,"E12.25.31.0"),sQuery(id+"F0.wireOp",EDGE,"E12.29.31.0"),sQuery(id+"F0.wireOp",EDGE,"E12.32.31.0"),sQuery(id+"F0.wireOp",EDGE,"E12.2.32.0"),sQuery(id+"F0.wireOp",EDGE,"E12.4.32.0"),sQuery(id+"F0.wireOp",EDGE,"E12.7.32.0"),sQuery(id+"F0.wireOp",EDGE,"E12.11.32.0"),sQuery(id+"F0.wireOp",EDGE,"E12.15.32.0"),sQuery(id+"F0.wireOp",EDGE,"E12.18.32.0"),sQuery(id+"F0.wireOp",EDGE,"E12.21.32.0"),sQuery(id+"F0.wireOp",EDGE,"E12.25.32.0"),sQuery(id+"F0.wireOp",EDGE,"E12.29.32.0"),sQuery(id+"F0.wireOp",EDGE,"E12.32.32.0"),sQuery(id+"F0.wireOp",EDGE,"E12.2.33.0"),sQuery(id+"F0.wireOp",EDGE,"E12.4.33.0"),sQuery(id+"F0.wireOp",EDGE,"E12.7.33.0"),sQuery(id+"F0.wireOp",EDGE,"E12.11.33.0"),sQuery(id+"F0.wireOp",EDGE,"E12.15.33.0"),sQuery(id+"F0.wireOp",EDGE,"E12.18.33.0"),sQuery(id+"F0.wireOp",EDGE,"E12.21.33.0"),sQuery(id+"F0.wireOp",EDGE,"E12.25.33.0"),sQuery(id+"F0.wireOp",EDGE,"E12.29.33.0"),sQuery(id+"F0.wireOp",EDGE,"E12.32.33.0"),sQuery(id+"F0.wireOp",EDGE,"E12.2.34.0"),sQuery(id+"F0.wireOp",EDGE,"E12.4.34.0"),sQuery(id+"F0.wireOp",EDGE,"E12.7.34.0"),sQuery(id+"F0.wireOp",EDGE,"E12.11.34.0"),sQuery(id+"F0.wireOp",EDGE,"E12.15.34.0"),sQuery(id+"F0.wireOp",EDGE,"E12.18.34.0"),sQuery(id+"F0.wireOp",EDGE,"E12.21.34.0"),sQuery(id+"F0.wireOp",EDGE,"E12.25.34.0"),sQuery(id+"F0.wireOp",EDGE,"E12.29.34.0"),sQuery(id+"F0.wireOp",EDGE,"E12.32.34.0"),sQuery(id+"F0.wireOp",EDGE,"E12.2.35.0"),sQuery(id+"F0.wireOp",EDGE,"E12.4.35.0"),sQuery(id+"F0.wireOp",EDGE,"E12.7.35.0"),sQuery(id+"F0.wireOp",EDGE,"E12.11.35.0"),sQuery(id+"F0.wireOp",EDGE,"E12.15.35.0"),sQuery(id+"F0.wireOp",EDGE,"E12.18.35.0"),sQuery(id+"F0.wireOp",EDGE,"E12.21.35.0"),sQuery(id+"F0.wireOp",EDGE,"E12.25.35.0"),sQuery(id+"F0.wireOp",EDGE,"E12.29.35.0"),sQuery(id+"F0.wireOp",EDGE,"E12.32.35.0"),sQuery(id+"F0.wireOp",EDGE,"E13.trimOffspring"),sQuery(id+"F0.wireOp",EDGE,"E14.trimOffspring"),sQuery(id+"F0.wireOp",EDGE,"E15.trimOffspring"),sQuery(id+"F0.wireOp",EDGE,"E16.trimOffspring"),sQuery(id+"F0.wireOp",EDGE,"E17.trimOffspring"),sQuery(id+"F0.wireOp",EDGE,"E18.trimOffspring"),sQuery(id+"F0.wireOp",EDGE,"E19.trimOffspring"),sQuery(id+"F0.wireOp",EDGE,"E20.trimOffspring"),sQuery(id+"F0.wireOp",EDGE,"E21.trimOffspring"),sQuery(id+"F0.wireOp",EDGE,"E22.trimOffspring"),sQuery(id+"F0.wireOp",EDGE,"E23.trimOffspring"),sQuery(id+"F0.wireOp",EDGE,"E24.trimOffspring"),sQuery(id+"F0.wireOp",EDGE,"E25.trimOffspring"),sQuery(id+"F0.wireOp",EDGE,"E26.trimOffspring"),sQuery(id+"F0.wireOp",EDGE,"E27.trimOffspring"),sQuery(id+"F0.wireOp",EDGE,"E28.trimOffspring"),sQuery(id+"F0.wireOp",EDGE,"E29.trimOffspring"),sQuery(id+"F0.wireOp",EDGE,"E30.trimOffspring"),sQuery(id+"F0.wireOp",EDGE,"E31.trimOffspring"),sQuery(id+"F0.wireOp",EDGE,"E32.trimOffspring"),sQuery(id+"F0.wireOp",EDGE,"E33.trimOffspring"),sQuery(id+"F0.wireOp",EDGE,"E34.trimOffspring"),sQuery(id+"F0.wireOp",EDGE,"E35.trimOffspring"),sQuery(id+"F0.wireOp",EDGE,"E36.trimOffspring"),sQuery(id+"F0.wireOp",EDGE,"E37.trimOffspring"),sQuery(id+"F0.wireOp",EDGE,"E38.trimOffspring"),sQuery(id+"F0.wireOp",EDGE,"E39.trimOffspring"),sQuery(id+"F0.wireOp",EDGE,"E40.trimOffspring"),sQuery(id+"F0.wireOp",EDGE,"E41.trimOffspring"),sQuery(id+"F0.wireOp",EDGE,"E42.trimOffspring"),sQuery(id+"F0.wireOp",EDGE,"E43.trimOffspring"),sQuery(id+"F0.wireOp",EDGE,"E44.trimOffspring"),sQuery(id+"F0.wireOp",EDGE,"E45.trimOffspring"),sQuery(id+"F0.wireOp",EDGE,"E46.trimOffspring"),sQuery(id+"F0.wireOp",EDGE,"E47.trimOffspring")])],"isStart":true}),makeQuery(id+"F7.hole-0.opRevolve","SWEPT_FACE",FACE,{"disambiguationData":[OSD([sQuery(id+"F7.hole-0.sketch.wireOp",EDGE,"core_line_2")])]})]});
            var Q21;
            Q21=makeQuery(id+"F7.hole-1.boolean.opBoolean","COPY",EDGE,{"derivedFrom":makeQuery(id+"F7.hole-1.opRevolve","SWEPT_EDGE",EDGE,{"disambiguationData":[OSD([sQuery(id+"F7.hole-1.sketch.wireOp",EDGE,"cbore_start_line_2"),sQuery(id+"F7.hole-1.sketch.wireOp",EDGE,"cbore_start_line_3")])]})});
            var Q22;
            Q22=makeQuery(id+"F7.hole-1.boolean.opBoolean","INTERSECT",EDGE,{"derivedFrom":[makeQuery(id+"F1.opExtrude","CAP_FACE",FACE,{"disambiguationData":[OSD([sQuery(id+"F0.wireOp",EDGE,"E0"),sQuery(id+"F0.wireOp",EDGE,"E1.trimOffspring"),sQuery(id+"F0.wireOp",EDGE,"E2"),sQuery(id+"F0.wireOp",EDGE,"E3"),sQuery(id+"F0.wireOp",EDGE,"E4.MirrorCS"),sQuery(id+"F0.wireOp",EDGE,"E5.MirrorCS"),sQuery(id+"F0.wireOp",EDGE,"E6.MirrorCS"),sQuery(id+"F0.wireOp",EDGE,"E7.filletArc"),sQuery(id+"F0.wireOp",EDGE,"E8.filletArc"),sQuery(id+"F0.wireOp",EDGE,"E9.filletArc"),sQuery(id+"F0.wireOp",EDGE,"E10.filletArc"),sQuery(id+"F0.wireOp",EDGE,"E11.1.0"),sQuery(id+"F0.wireOp",EDGE,"E11.1.1"),sQuery(id+"F0.wireOp",EDGE,"E11.1.2"),sQuery(id+"F0.wireOp",EDGE,"E11.1.3"),sQuery(id+"F0.wireOp",EDGE,"E11.1.4"),sQuery(id+"F0.wireOp",EDGE,"E11.1.5"),sQuery(id+"F0.wireOp",EDGE,"E11.1.6"),sQuery(id+"F0.wireOp",EDGE,"E11.1.7"),sQuery(id+"F0.wireOp",EDGE,"E11.1.8"),sQuery(id+"F0.wireOp",EDGE,"E11.1.9"),sQuery(id+"F0.wireOp",EDGE,"E11.2.0"),sQuery(id+"F0.wireOp",EDGE,"E11.2.1"),sQuery(id+"F0.wireOp",EDGE,"E11.2.2"),sQuery(id+"F0.wireOp",EDGE,"E11.2.3"),sQuery(id+"F0.wireOp",EDGE,"E11.2.4"),sQuery(id+"F0.wireOp",EDGE,"E11.2.5"),sQuery(id+"F0.wireOp",EDGE,"E11.2.6"),sQuery(id+"F0.wireOp",EDGE,"E11.2.7"),sQuery(id+"F0.wireOp",EDGE,"E11.2.8"),sQuery(id+"F0.wireOp",EDGE,"E11.2.9"),sQuery(id+"F0.wireOp",EDGE,"E12.2.3.0"),sQuery(id+"F0.wireOp",EDGE,"E12.4.3.0"),sQuery(id+"F0.wireOp",EDGE,"E12.7.3.0"),sQuery(id+"F0.wireOp",EDGE,"E12.11.3.0"),sQuery(id+"F0.wireOp",EDGE,"E12.15.3.0"),sQuery(id+"F0.wireOp",EDGE,"E12.18.3.0"),sQuery(id+"F0.wireOp",EDGE,"E12.21.3.0"),sQuery(id+"F0.wireOp",EDGE,"E12.25.3.0"),sQuery(id+"F0.wireOp",EDGE,"E12.29.3.0"),sQuery(id+"F0.wireOp",EDGE,"E12.32.3.0"),sQuery(id+"F0.wireOp",EDGE,"E12.2.4.0"),sQuery(id+"F0.wireOp",EDGE,"E12.4.4.0"),sQuery(id+"F0.wireOp",EDGE,"E12.7.4.0"),sQuery(id+"F0.wireOp",EDGE,"E12.11.4.0"),sQuery(id+"F0.wireOp",EDGE,"E12.15.4.0"),sQuery(id+"F0.wireOp",EDGE,"E12.18.4.0"),sQuery(id+"F0.wireOp",EDGE,"E12.21.4.0"),sQuery(id+"F0.wireOp",EDGE,"E12.25.4.0"),sQuery(id+"F0.wireOp",EDGE,"E12.29.4.0"),sQuery(id+"F0.wireOp",EDGE,"E12.32.4.0"),sQuery(id+"F0.wireOp",EDGE,"E12.2.5.0"),sQuery(id+"F0.wireOp",EDGE,"E12.4.5.0"),sQuery(id+"F0.wireOp",EDGE,"E12.7.5.0"),sQuery(id+"F0.wireOp",EDGE,"E12.11.5.0"),sQuery(id+"F0.wireOp",EDGE,"E12.15.5.0"),sQuery(id+"F0.wireOp",EDGE,"E12.18.5.0"),sQuery(id+"F0.wireOp",EDGE,"E12.21.5.0"),sQuery(id+"F0.wireOp",EDGE,"E12.25.5.0"),sQuery(id+"F0.wireOp",EDGE,"E12.29.5.0"),sQuery(id+"F0.wireOp",EDGE,"E12.32.5.0"),sQuery(id+"F0.wireOp",EDGE,"E12.2.6.0"),sQuery(id+"F0.wireOp",EDGE,"E12.4.6.0"),sQuery(id+"F0.wireOp",EDGE,"E12.7.6.0"),sQuery(id+"F0.wireOp",EDGE,"E12.11.6.0"),sQuery(id+"F0.wireOp",EDGE,"E12.15.6.0"),sQuery(id+"F0.wireOp",EDGE,"E12.18.6.0"),sQuery(id+"F0.wireOp",EDGE,"E12.21.6.0"),sQuery(id+"F0.wireOp",EDGE,"E12.25.6.0"),sQuery(id+"F0.wireOp",EDGE,"E12.29.6.0"),sQuery(id+"F0.wireOp",EDGE,"E12.32.6.0"),sQuery(id+"F0.wireOp",EDGE,"E12.2.7.0"),sQuery(id+"F0.wireOp",EDGE,"E12.4.7.0"),sQuery(id+"F0.wireOp",EDGE,"E12.7.7.0"),sQuery(id+"F0.wireOp",EDGE,"E12.11.7.0"),sQuery(id+"F0.wireOp",EDGE,"E12.15.7.0"),sQuery(id+"F0.wireOp",EDGE,"E12.18.7.0"),sQuery(id+"F0.wireOp",EDGE,"E12.21.7.0"),sQuery(id+"F0.wireOp",EDGE,"E12.25.7.0"),sQuery(id+"F0.wireOp",EDGE,"E12.29.7.0"),sQuery(id+"F0.wireOp",EDGE,"E12.32.7.0"),sQuery(id+"F0.wireOp",EDGE,"E12.2.8.0"),sQuery(id+"F0.wireOp",EDGE,"E12.4.8.0"),sQuery(id+"F0.wireOp",EDGE,"E12.7.8.0"),sQuery(id+"F0.wireOp",EDGE,"E12.11.8.0"),sQuery(id+"F0.wireOp",EDGE,"E12.15.8.0"),sQuery(id+"F0.wireOp",EDGE,"E12.18.8.0"),sQuery(id+"F0.wireOp",EDGE,"E12.21.8.0"),sQuery(id+"F0.wireOp",EDGE,"E12.25.8.0"),sQuery(id+"F0.wireOp",EDGE,"E12.29.8.0"),sQuery(id+"F0.wireOp",EDGE,"E12.32.8.0"),sQuery(id+"F0.wireOp",EDGE,"E12.2.9.0"),sQuery(id+"F0.wireOp",EDGE,"E12.4.9.0"),sQuery(id+"F0.wireOp",EDGE,"E12.7.9.0"),sQuery(id+"F0.wireOp",EDGE,"E12.11.9.0"),sQuery(id+"F0.wireOp",EDGE,"E12.15.9.0"),sQuery(id+"F0.wireOp",EDGE,"E12.18.9.0"),sQuery(id+"F0.wireOp",EDGE,"E12.21.9.0"),sQuery(id+"F0.wireOp",EDGE,"E12.25.9.0"),sQuery(id+"F0.wireOp",EDGE,"E12.29.9.0"),sQuery(id+"F0.wireOp",EDGE,"E12.32.9.0"),sQuery(id+"F0.wireOp",EDGE,"E12.2.10.0"),sQuery(id+"F0.wireOp",EDGE,"E12.4.10.0"),sQuery(id+"F0.wireOp",EDGE,"E12.7.10.0"),sQuery(id+"F0.wireOp",EDGE,"E12.11.10.0"),sQuery(id+"F0.wireOp",EDGE,"E12.15.10.0"),sQuery(id+"F0.wireOp",EDGE,"E12.18.10.0"),sQuery(id+"F0.wireOp",EDGE,"E12.21.10.0"),sQuery(id+"F0.wireOp",EDGE,"E12.25.10.0"),sQuery(id+"F0.wireOp",EDGE,"E12.29.10.0"),sQuery(id+"F0.wireOp",EDGE,"E12.32.10.0"),sQuery(id+"F0.wireOp",EDGE,"E12.2.11.0"),sQuery(id+"F0.wireOp",EDGE,"E12.4.11.0"),sQuery(id+"F0.wireOp",EDGE,"E12.7.11.0"),sQuery(id+"F0.wireOp",EDGE,"E12.11.11.0"),sQuery(id+"F0.wireOp",EDGE,"E12.15.11.0"),sQuery(id+"F0.wireOp",EDGE,"E12.18.11.0"),sQuery(id+"F0.wireOp",EDGE,"E12.21.11.0"),sQuery(id+"F0.wireOp",EDGE,"E12.25.11.0"),sQuery(id+"F0.wireOp",EDGE,"E12.29.11.0"),sQuery(id+"F0.wireOp",EDGE,"E12.32.11.0"),sQuery(id+"F0.wireOp",EDGE,"E12.2.12.0"),sQuery(id+"F0.wireOp",EDGE,"E12.4.12.0"),sQuery(id+"F0.wireOp",EDGE,"E12.7.12.0"),sQuery(id+"F0.wireOp",EDGE,"E12.11.12.0"),sQuery(id+"F0.wireOp",EDGE,"E12.15.12.0"),sQuery(id+"F0.wireOp",EDGE,"E12.18.12.0"),sQuery(id+"F0.wireOp",EDGE,"E12.21.12.0"),sQuery(id+"F0.wireOp",EDGE,"E12.25.12.0"),sQuery(id+"F0.wireOp",EDGE,"E12.29.12.0"),sQuery(id+"F0.wireOp",EDGE,"E12.32.12.0"),sQuery(id+"F0.wireOp",EDGE,"E12.2.13.0"),sQuery(id+"F0.wireOp",EDGE,"E12.4.13.0"),sQuery(id+"F0.wireOp",EDGE,"E12.7.13.0"),sQuery(id+"F0.wireOp",EDGE,"E12.11.13.0"),sQuery(id+"F0.wireOp",EDGE,"E12.15.13.0"),sQuery(id+"F0.wireOp",EDGE,"E12.18.13.0"),sQuery(id+"F0.wireOp",EDGE,"E12.21.13.0"),sQuery(id+"F0.wireOp",EDGE,"E12.25.13.0"),sQuery(id+"F0.wireOp",EDGE,"E12.29.13.0"),sQuery(id+"F0.wireOp",EDGE,"E12.32.13.0"),sQuery(id+"F0.wireOp",EDGE,"E12.2.14.0"),sQuery(id+"F0.wireOp",EDGE,"E12.4.14.0"),sQuery(id+"F0.wireOp",EDGE,"E12.7.14.0"),sQuery(id+"F0.wireOp",EDGE,"E12.11.14.0"),sQuery(id+"F0.wireOp",EDGE,"E12.15.14.0"),sQuery(id+"F0.wireOp",EDGE,"E12.18.14.0"),sQuery(id+"F0.wireOp",EDGE,"E12.21.14.0"),sQuery(id+"F0.wireOp",EDGE,"E12.25.14.0"),sQuery(id+"F0.wireOp",EDGE,"E12.29.14.0"),sQuery(id+"F0.wireOp",EDGE,"E12.32.14.0"),sQuery(id+"F0.wireOp",EDGE,"E12.2.15.0"),sQuery(id+"F0.wireOp",EDGE,"E12.4.15.0"),sQuery(id+"F0.wireOp",EDGE,"E12.7.15.0"),sQuery(id+"F0.wireOp",EDGE,"E12.11.15.0"),sQuery(id+"F0.wireOp",EDGE,"E12.15.15.0"),sQuery(id+"F0.wireOp",EDGE,"E12.18.15.0"),sQuery(id+"F0.wireOp",EDGE,"E12.21.15.0"),sQuery(id+"F0.wireOp",EDGE,"E12.25.15.0"),sQuery(id+"F0.wireOp",EDGE,"E12.29.15.0"),sQuery(id+"F0.wireOp",EDGE,"E12.32.15.0"),sQuery(id+"F0.wireOp",EDGE,"E12.2.16.0"),sQuery(id+"F0.wireOp",EDGE,"E12.4.16.0"),sQuery(id+"F0.wireOp",EDGE,"E12.7.16.0"),sQuery(id+"F0.wireOp",EDGE,"E12.11.16.0"),sQuery(id+"F0.wireOp",EDGE,"E12.15.16.0"),sQuery(id+"F0.wireOp",EDGE,"E12.18.16.0"),sQuery(id+"F0.wireOp",EDGE,"E12.21.16.0"),sQuery(id+"F0.wireOp",EDGE,"E12.25.16.0"),sQuery(id+"F0.wireOp",EDGE,"E12.29.16.0"),sQuery(id+"F0.wireOp",EDGE,"E12.32.16.0"),sQuery(id+"F0.wireOp",EDGE,"E12.2.17.0"),sQuery(id+"F0.wireOp",EDGE,"E12.4.17.0"),sQuery(id+"F0.wireOp",EDGE,"E12.7.17.0"),sQuery(id+"F0.wireOp",EDGE,"E12.11.17.0"),sQuery(id+"F0.wireOp",EDGE,"E12.15.17.0"),sQuery(id+"F0.wireOp",EDGE,"E12.18.17.0"),sQuery(id+"F0.wireOp",EDGE,"E12.21.17.0"),sQuery(id+"F0.wireOp",EDGE,"E12.25.17.0"),sQuery(id+"F0.wireOp",EDGE,"E12.29.17.0"),sQuery(id+"F0.wireOp",EDGE,"E12.32.17.0"),sQuery(id+"F0.wireOp",EDGE,"E12.2.18.0"),sQuery(id+"F0.wireOp",EDGE,"E12.4.18.0"),sQuery(id+"F0.wireOp",EDGE,"E12.7.18.0"),sQuery(id+"F0.wireOp",EDGE,"E12.11.18.0"),sQuery(id+"F0.wireOp",EDGE,"E12.15.18.0"),sQuery(id+"F0.wireOp",EDGE,"E12.18.18.0"),sQuery(id+"F0.wireOp",EDGE,"E12.21.18.0"),sQuery(id+"F0.wireOp",EDGE,"E12.25.18.0"),sQuery(id+"F0.wireOp",EDGE,"E12.29.18.0"),sQuery(id+"F0.wireOp",EDGE,"E12.32.18.0"),sQuery(id+"F0.wireOp",EDGE,"E12.2.19.0"),sQuery(id+"F0.wireOp",EDGE,"E12.4.19.0"),sQuery(id+"F0.wireOp",EDGE,"E12.7.19.0"),sQuery(id+"F0.wireOp",EDGE,"E12.11.19.0"),sQuery(id+"F0.wireOp",EDGE,"E12.15.19.0"),sQuery(id+"F0.wireOp",EDGE,"E12.18.19.0"),sQuery(id+"F0.wireOp",EDGE,"E12.21.19.0"),sQuery(id+"F0.wireOp",EDGE,"E12.25.19.0"),sQuery(id+"F0.wireOp",EDGE,"E12.29.19.0"),sQuery(id+"F0.wireOp",EDGE,"E12.32.19.0"),sQuery(id+"F0.wireOp",EDGE,"E12.2.20.0"),sQuery(id+"F0.wireOp",EDGE,"E12.4.20.0"),sQuery(id+"F0.wireOp",EDGE,"E12.7.20.0"),sQuery(id+"F0.wireOp",EDGE,"E12.11.20.0"),sQuery(id+"F0.wireOp",EDGE,"E12.15.20.0"),sQuery(id+"F0.wireOp",EDGE,"E12.18.20.0"),sQuery(id+"F0.wireOp",EDGE,"E12.21.20.0"),sQuery(id+"F0.wireOp",EDGE,"E12.25.20.0"),sQuery(id+"F0.wireOp",EDGE,"E12.29.20.0"),sQuery(id+"F0.wireOp",EDGE,"E12.32.20.0"),sQuery(id+"F0.wireOp",EDGE,"E12.2.21.0"),sQuery(id+"F0.wireOp",EDGE,"E12.4.21.0"),sQuery(id+"F0.wireOp",EDGE,"E12.7.21.0"),sQuery(id+"F0.wireOp",EDGE,"E12.11.21.0"),sQuery(id+"F0.wireOp",EDGE,"E12.15.21.0"),sQuery(id+"F0.wireOp",EDGE,"E12.18.21.0"),sQuery(id+"F0.wireOp",EDGE,"E12.21.21.0"),sQuery(id+"F0.wireOp",EDGE,"E12.25.21.0"),sQuery(id+"F0.wireOp",EDGE,"E12.29.21.0"),sQuery(id+"F0.wireOp",EDGE,"E12.32.21.0"),sQuery(id+"F0.wireOp",EDGE,"E12.2.22.0"),sQuery(id+"F0.wireOp",EDGE,"E12.4.22.0"),sQuery(id+"F0.wireOp",EDGE,"E12.7.22.0"),sQuery(id+"F0.wireOp",EDGE,"E12.11.22.0"),sQuery(id+"F0.wireOp",EDGE,"E12.15.22.0"),sQuery(id+"F0.wireOp",EDGE,"E12.18.22.0"),sQuery(id+"F0.wireOp",EDGE,"E12.21.22.0"),sQuery(id+"F0.wireOp",EDGE,"E12.25.22.0"),sQuery(id+"F0.wireOp",EDGE,"E12.29.22.0"),sQuery(id+"F0.wireOp",EDGE,"E12.32.22.0"),sQuery(id+"F0.wireOp",EDGE,"E12.2.23.0"),sQuery(id+"F0.wireOp",EDGE,"E12.4.23.0"),sQuery(id+"F0.wireOp",EDGE,"E12.7.23.0"),sQuery(id+"F0.wireOp",EDGE,"E12.11.23.0"),sQuery(id+"F0.wireOp",EDGE,"E12.15.23.0"),sQuery(id+"F0.wireOp",EDGE,"E12.18.23.0"),sQuery(id+"F0.wireOp",EDGE,"E12.21.23.0"),sQuery(id+"F0.wireOp",EDGE,"E12.25.23.0"),sQuery(id+"F0.wireOp",EDGE,"E12.29.23.0"),sQuery(id+"F0.wireOp",EDGE,"E12.32.23.0"),sQuery(id+"F0.wireOp",EDGE,"E12.2.24.0"),sQuery(id+"F0.wireOp",EDGE,"E12.4.24.0"),sQuery(id+"F0.wireOp",EDGE,"E12.7.24.0"),sQuery(id+"F0.wireOp",EDGE,"E12.11.24.0"),sQuery(id+"F0.wireOp",EDGE,"E12.15.24.0"),sQuery(id+"F0.wireOp",EDGE,"E12.18.24.0"),sQuery(id+"F0.wireOp",EDGE,"E12.21.24.0"),sQuery(id+"F0.wireOp",EDGE,"E12.25.24.0"),sQuery(id+"F0.wireOp",EDGE,"E12.29.24.0"),sQuery(id+"F0.wireOp",EDGE,"E12.32.24.0"),sQuery(id+"F0.wireOp",EDGE,"E12.2.25.0"),sQuery(id+"F0.wireOp",EDGE,"E12.4.25.0"),sQuery(id+"F0.wireOp",EDGE,"E12.7.25.0"),sQuery(id+"F0.wireOp",EDGE,"E12.11.25.0"),sQuery(id+"F0.wireOp",EDGE,"E12.15.25.0"),sQuery(id+"F0.wireOp",EDGE,"E12.18.25.0"),sQuery(id+"F0.wireOp",EDGE,"E12.21.25.0"),sQuery(id+"F0.wireOp",EDGE,"E12.25.25.0"),sQuery(id+"F0.wireOp",EDGE,"E12.29.25.0"),sQuery(id+"F0.wireOp",EDGE,"E12.32.25.0"),sQuery(id+"F0.wireOp",EDGE,"E12.2.26.0"),sQuery(id+"F0.wireOp",EDGE,"E12.4.26.0"),sQuery(id+"F0.wireOp",EDGE,"E12.7.26.0"),sQuery(id+"F0.wireOp",EDGE,"E12.11.26.0"),sQuery(id+"F0.wireOp",EDGE,"E12.15.26.0"),sQuery(id+"F0.wireOp",EDGE,"E12.18.26.0"),sQuery(id+"F0.wireOp",EDGE,"E12.21.26.0"),sQuery(id+"F0.wireOp",EDGE,"E12.25.26.0"),sQuery(id+"F0.wireOp",EDGE,"E12.29.26.0"),sQuery(id+"F0.wireOp",EDGE,"E12.32.26.0"),sQuery(id+"F0.wireOp",EDGE,"E12.2.27.0"),sQuery(id+"F0.wireOp",EDGE,"E12.4.27.0"),sQuery(id+"F0.wireOp",EDGE,"E12.7.27.0"),sQuery(id+"F0.wireOp",EDGE,"E12.11.27.0"),sQuery(id+"F0.wireOp",EDGE,"E12.15.27.0"),sQuery(id+"F0.wireOp",EDGE,"E12.18.27.0"),sQuery(id+"F0.wireOp",EDGE,"E12.21.27.0"),sQuery(id+"F0.wireOp",EDGE,"E12.25.27.0"),sQuery(id+"F0.wireOp",EDGE,"E12.29.27.0"),sQuery(id+"F0.wireOp",EDGE,"E12.32.27.0"),sQuery(id+"F0.wireOp",EDGE,"E12.2.28.0"),sQuery(id+"F0.wireOp",EDGE,"E12.4.28.0"),sQuery(id+"F0.wireOp",EDGE,"E12.7.28.0"),sQuery(id+"F0.wireOp",EDGE,"E12.11.28.0"),sQuery(id+"F0.wireOp",EDGE,"E12.15.28.0"),sQuery(id+"F0.wireOp",EDGE,"E12.18.28.0"),sQuery(id+"F0.wireOp",EDGE,"E12.21.28.0"),sQuery(id+"F0.wireOp",EDGE,"E12.25.28.0"),sQuery(id+"F0.wireOp",EDGE,"E12.29.28.0"),sQuery(id+"F0.wireOp",EDGE,"E12.32.28.0"),sQuery(id+"F0.wireOp",EDGE,"E12.2.29.0"),sQuery(id+"F0.wireOp",EDGE,"E12.4.29.0"),sQuery(id+"F0.wireOp",EDGE,"E12.7.29.0"),sQuery(id+"F0.wireOp",EDGE,"E12.11.29.0"),sQuery(id+"F0.wireOp",EDGE,"E12.15.29.0"),sQuery(id+"F0.wireOp",EDGE,"E12.18.29.0"),sQuery(id+"F0.wireOp",EDGE,"E12.21.29.0"),sQuery(id+"F0.wireOp",EDGE,"E12.25.29.0"),sQuery(id+"F0.wireOp",EDGE,"E12.29.29.0"),sQuery(id+"F0.wireOp",EDGE,"E12.32.29.0"),sQuery(id+"F0.wireOp",EDGE,"E12.2.30.0"),sQuery(id+"F0.wireOp",EDGE,"E12.4.30.0"),sQuery(id+"F0.wireOp",EDGE,"E12.7.30.0"),sQuery(id+"F0.wireOp",EDGE,"E12.11.30.0"),sQuery(id+"F0.wireOp",EDGE,"E12.15.30.0"),sQuery(id+"F0.wireOp",EDGE,"E12.18.30.0"),sQuery(id+"F0.wireOp",EDGE,"E12.21.30.0"),sQuery(id+"F0.wireOp",EDGE,"E12.25.30.0"),sQuery(id+"F0.wireOp",EDGE,"E12.29.30.0"),sQuery(id+"F0.wireOp",EDGE,"E12.32.30.0"),sQuery(id+"F0.wireOp",EDGE,"E12.2.31.0"),sQuery(id+"F0.wireOp",EDGE,"E12.4.31.0"),sQuery(id+"F0.wireOp",EDGE,"E12.7.31.0"),sQuery(id+"F0.wireOp",EDGE,"E12.11.31.0"),sQuery(id+"F0.wireOp",EDGE,"E12.15.31.0"),sQuery(id+"F0.wireOp",EDGE,"E12.18.31.0"),sQuery(id+"F0.wireOp",EDGE,"E12.21.31.0"),sQuery(id+"F0.wireOp",EDGE,"E12.25.31.0"),sQuery(id+"F0.wireOp",EDGE,"E12.29.31.0"),sQuery(id+"F0.wireOp",EDGE,"E12.32.31.0"),sQuery(id+"F0.wireOp",EDGE,"E12.2.32.0"),sQuery(id+"F0.wireOp",EDGE,"E12.4.32.0"),sQuery(id+"F0.wireOp",EDGE,"E12.7.32.0"),sQuery(id+"F0.wireOp",EDGE,"E12.11.32.0"),sQuery(id+"F0.wireOp",EDGE,"E12.15.32.0"),sQuery(id+"F0.wireOp",EDGE,"E12.18.32.0"),sQuery(id+"F0.wireOp",EDGE,"E12.21.32.0"),sQuery(id+"F0.wireOp",EDGE,"E12.25.32.0"),sQuery(id+"F0.wireOp",EDGE,"E12.29.32.0"),sQuery(id+"F0.wireOp",EDGE,"E12.32.32.0"),sQuery(id+"F0.wireOp",EDGE,"E12.2.33.0"),sQuery(id+"F0.wireOp",EDGE,"E12.4.33.0"),sQuery(id+"F0.wireOp",EDGE,"E12.7.33.0"),sQuery(id+"F0.wireOp",EDGE,"E12.11.33.0"),sQuery(id+"F0.wireOp",EDGE,"E12.15.33.0"),sQuery(id+"F0.wireOp",EDGE,"E12.18.33.0"),sQuery(id+"F0.wireOp",EDGE,"E12.21.33.0"),sQuery(id+"F0.wireOp",EDGE,"E12.25.33.0"),sQuery(id+"F0.wireOp",EDGE,"E12.29.33.0"),sQuery(id+"F0.wireOp",EDGE,"E12.32.33.0"),sQuery(id+"F0.wireOp",EDGE,"E12.2.34.0"),sQuery(id+"F0.wireOp",EDGE,"E12.4.34.0"),sQuery(id+"F0.wireOp",EDGE,"E12.7.34.0"),sQuery(id+"F0.wireOp",EDGE,"E12.11.34.0"),sQuery(id+"F0.wireOp",EDGE,"E12.15.34.0"),sQuery(id+"F0.wireOp",EDGE,"E12.18.34.0"),sQuery(id+"F0.wireOp",EDGE,"E12.21.34.0"),sQuery(id+"F0.wireOp",EDGE,"E12.25.34.0"),sQuery(id+"F0.wireOp",EDGE,"E12.29.34.0"),sQuery(id+"F0.wireOp",EDGE,"E12.32.34.0"),sQuery(id+"F0.wireOp",EDGE,"E12.2.35.0"),sQuery(id+"F0.wireOp",EDGE,"E12.4.35.0"),sQuery(id+"F0.wireOp",EDGE,"E12.7.35.0"),sQuery(id+"F0.wireOp",EDGE,"E12.11.35.0"),sQuery(id+"F0.wireOp",EDGE,"E12.15.35.0"),sQuery(id+"F0.wireOp",EDGE,"E12.18.35.0"),sQuery(id+"F0.wireOp",EDGE,"E12.21.35.0"),sQuery(id+"F0.wireOp",EDGE,"E12.25.35.0"),sQuery(id+"F0.wireOp",EDGE,"E12.29.35.0"),sQuery(id+"F0.wireOp",EDGE,"E12.32.35.0"),sQuery(id+"F0.wireOp",EDGE,"E13.trimOffspring"),sQuery(id+"F0.wireOp",EDGE,"E14.trimOffspring"),sQuery(id+"F0.wireOp",EDGE,"E15.trimOffspring"),sQuery(id+"F0.wireOp",EDGE,"E16.trimOffspring"),sQuery(id+"F0.wireOp",EDGE,"E17.trimOffspring"),sQuery(id+"F0.wireOp",EDGE,"E18.trimOffspring"),sQuery(id+"F0.wireOp",EDGE,"E19.trimOffspring"),sQuery(id+"F0.wireOp",EDGE,"E20.trimOffspring"),sQuery(id+"F0.wireOp",EDGE,"E21.trimOffspring"),sQuery(id+"F0.wireOp",EDGE,"E22.trimOffspring"),sQuery(id+"F0.wireOp",EDGE,"E23.trimOffspring"),sQuery(id+"F0.wireOp",EDGE,"E24.trimOffspring"),sQuery(id+"F0.wireOp",EDGE,"E25.trimOffspring"),sQuery(id+"F0.wireOp",EDGE,"E26.trimOffspring"),sQuery(id+"F0.wireOp",EDGE,"E27.trimOffspring"),sQuery(id+"F0.wireOp",EDGE,"E28.trimOffspring"),sQuery(id+"F0.wireOp",EDGE,"E29.trimOffspring"),sQuery(id+"F0.wireOp",EDGE,"E30.trimOffspring"),sQuery(id+"F0.wireOp",EDGE,"E31.trimOffspring"),sQuery(id+"F0.wireOp",EDGE,"E32.trimOffspring"),sQuery(id+"F0.wireOp",EDGE,"E33.trimOffspring"),sQuery(id+"F0.wireOp",EDGE,"E34.trimOffspring"),sQuery(id+"F0.wireOp",EDGE,"E35.trimOffspring"),sQuery(id+"F0.wireOp",EDGE,"E36.trimOffspring"),sQuery(id+"F0.wireOp",EDGE,"E37.trimOffspring"),sQuery(id+"F0.wireOp",EDGE,"E38.trimOffspring"),sQuery(id+"F0.wireOp",EDGE,"E39.trimOffspring"),sQuery(id+"F0.wireOp",EDGE,"E40.trimOffspring"),sQuery(id+"F0.wireOp",EDGE,"E41.trimOffspring"),sQuery(id+"F0.wireOp",EDGE,"E42.trimOffspring"),sQuery(id+"F0.wireOp",EDGE,"E43.trimOffspring"),sQuery(id+"F0.wireOp",EDGE,"E44.trimOffspring"),sQuery(id+"F0.wireOp",EDGE,"E45.trimOffspring"),sQuery(id+"F0.wireOp",EDGE,"E46.trimOffspring"),sQuery(id+"F0.wireOp",EDGE,"E47.trimOffspring")])],"isStart":true}),makeQuery(id+"F7.hole-1.opRevolve","SWEPT_FACE",FACE,{"disambiguationData":[OSD([sQuery(id+"F7.hole-1.sketch.wireOp",EDGE,"core_line_2")])]})]});
            var Q23;
            Q23=makeQuery(id+"F7.hole-2.boolean.opBoolean","INTERSECT",EDGE,{"derivedFrom":[makeQuery(id+"F1.opExtrude","CAP_FACE",FACE,{"disambiguationData":[OSD([sQuery(id+"F0.wireOp",EDGE,"E0"),sQuery(id+"F0.wireOp",EDGE,"E1.trimOffspring"),sQuery(id+"F0.wireOp",EDGE,"E2"),sQuery(id+"F0.wireOp",EDGE,"E3"),sQuery(id+"F0.wireOp",EDGE,"E4.MirrorCS"),sQuery(id+"F0.wireOp",EDGE,"E5.MirrorCS"),sQuery(id+"F0.wireOp",EDGE,"E6.MirrorCS"),sQuery(id+"F0.wireOp",EDGE,"E7.filletArc"),sQuery(id+"F0.wireOp",EDGE,"E8.filletArc"),sQuery(id+"F0.wireOp",EDGE,"E9.filletArc"),sQuery(id+"F0.wireOp",EDGE,"E10.filletArc"),sQuery(id+"F0.wireOp",EDGE,"E11.1.0"),sQuery(id+"F0.wireOp",EDGE,"E11.1.1"),sQuery(id+"F0.wireOp",EDGE,"E11.1.2"),sQuery(id+"F0.wireOp",EDGE,"E11.1.3"),sQuery(id+"F0.wireOp",EDGE,"E11.1.4"),sQuery(id+"F0.wireOp",EDGE,"E11.1.5"),sQuery(id+"F0.wireOp",EDGE,"E11.1.6"),sQuery(id+"F0.wireOp",EDGE,"E11.1.7"),sQuery(id+"F0.wireOp",EDGE,"E11.1.8"),sQuery(id+"F0.wireOp",EDGE,"E11.1.9"),sQuery(id+"F0.wireOp",EDGE,"E11.2.0"),sQuery(id+"F0.wireOp",EDGE,"E11.2.1"),sQuery(id+"F0.wireOp",EDGE,"E11.2.2"),sQuery(id+"F0.wireOp",EDGE,"E11.2.3"),sQuery(id+"F0.wireOp",EDGE,"E11.2.4"),sQuery(id+"F0.wireOp",EDGE,"E11.2.5"),sQuery(id+"F0.wireOp",EDGE,"E11.2.6"),sQuery(id+"F0.wireOp",EDGE,"E11.2.7"),sQuery(id+"F0.wireOp",EDGE,"E11.2.8"),sQuery(id+"F0.wireOp",EDGE,"E11.2.9"),sQuery(id+"F0.wireOp",EDGE,"E12.2.3.0"),sQuery(id+"F0.wireOp",EDGE,"E12.4.3.0"),sQuery(id+"F0.wireOp",EDGE,"E12.7.3.0"),sQuery(id+"F0.wireOp",EDGE,"E12.11.3.0"),sQuery(id+"F0.wireOp",EDGE,"E12.15.3.0"),sQuery(id+"F0.wireOp",EDGE,"E12.18.3.0"),sQuery(id+"F0.wireOp",EDGE,"E12.21.3.0"),sQuery(id+"F0.wireOp",EDGE,"E12.25.3.0"),sQuery(id+"F0.wireOp",EDGE,"E12.29.3.0"),sQuery(id+"F0.wireOp",EDGE,"E12.32.3.0"),sQuery(id+"F0.wireOp",EDGE,"E12.2.4.0"),sQuery(id+"F0.wireOp",EDGE,"E12.4.4.0"),sQuery(id+"F0.wireOp",EDGE,"E12.7.4.0"),sQuery(id+"F0.wireOp",EDGE,"E12.11.4.0"),sQuery(id+"F0.wireOp",EDGE,"E12.15.4.0"),sQuery(id+"F0.wireOp",EDGE,"E12.18.4.0"),sQuery(id+"F0.wireOp",EDGE,"E12.21.4.0"),sQuery(id+"F0.wireOp",EDGE,"E12.25.4.0"),sQuery(id+"F0.wireOp",EDGE,"E12.29.4.0"),sQuery(id+"F0.wireOp",EDGE,"E12.32.4.0"),sQuery(id+"F0.wireOp",EDGE,"E12.2.5.0"),sQuery(id+"F0.wireOp",EDGE,"E12.4.5.0"),sQuery(id+"F0.wireOp",EDGE,"E12.7.5.0"),sQuery(id+"F0.wireOp",EDGE,"E12.11.5.0"),sQuery(id+"F0.wireOp",EDGE,"E12.15.5.0"),sQuery(id+"F0.wireOp",EDGE,"E12.18.5.0"),sQuery(id+"F0.wireOp",EDGE,"E12.21.5.0"),sQuery(id+"F0.wireOp",EDGE,"E12.25.5.0"),sQuery(id+"F0.wireOp",EDGE,"E12.29.5.0"),sQuery(id+"F0.wireOp",EDGE,"E12.32.5.0"),sQuery(id+"F0.wireOp",EDGE,"E12.2.6.0"),sQuery(id+"F0.wireOp",EDGE,"E12.4.6.0"),sQuery(id+"F0.wireOp",EDGE,"E12.7.6.0"),sQuery(id+"F0.wireOp",EDGE,"E12.11.6.0"),sQuery(id+"F0.wireOp",EDGE,"E12.15.6.0"),sQuery(id+"F0.wireOp",EDGE,"E12.18.6.0"),sQuery(id+"F0.wireOp",EDGE,"E12.21.6.0"),sQuery(id+"F0.wireOp",EDGE,"E12.25.6.0"),sQuery(id+"F0.wireOp",EDGE,"E12.29.6.0"),sQuery(id+"F0.wireOp",EDGE,"E12.32.6.0"),sQuery(id+"F0.wireOp",EDGE,"E12.2.7.0"),sQuery(id+"F0.wireOp",EDGE,"E12.4.7.0"),sQuery(id+"F0.wireOp",EDGE,"E12.7.7.0"),sQuery(id+"F0.wireOp",EDGE,"E12.11.7.0"),sQuery(id+"F0.wireOp",EDGE,"E12.15.7.0"),sQuery(id+"F0.wireOp",EDGE,"E12.18.7.0"),sQuery(id+"F0.wireOp",EDGE,"E12.21.7.0"),sQuery(id+"F0.wireOp",EDGE,"E12.25.7.0"),sQuery(id+"F0.wireOp",EDGE,"E12.29.7.0"),sQuery(id+"F0.wireOp",EDGE,"E12.32.7.0"),sQuery(id+"F0.wireOp",EDGE,"E12.2.8.0"),sQuery(id+"F0.wireOp",EDGE,"E12.4.8.0"),sQuery(id+"F0.wireOp",EDGE,"E12.7.8.0"),sQuery(id+"F0.wireOp",EDGE,"E12.11.8.0"),sQuery(id+"F0.wireOp",EDGE,"E12.15.8.0"),sQuery(id+"F0.wireOp",EDGE,"E12.18.8.0"),sQuery(id+"F0.wireOp",EDGE,"E12.21.8.0"),sQuery(id+"F0.wireOp",EDGE,"E12.25.8.0"),sQuery(id+"F0.wireOp",EDGE,"E12.29.8.0"),sQuery(id+"F0.wireOp",EDGE,"E12.32.8.0"),sQuery(id+"F0.wireOp",EDGE,"E12.2.9.0"),sQuery(id+"F0.wireOp",EDGE,"E12.4.9.0"),sQuery(id+"F0.wireOp",EDGE,"E12.7.9.0"),sQuery(id+"F0.wireOp",EDGE,"E12.11.9.0"),sQuery(id+"F0.wireOp",EDGE,"E12.15.9.0"),sQuery(id+"F0.wireOp",EDGE,"E12.18.9.0"),sQuery(id+"F0.wireOp",EDGE,"E12.21.9.0"),sQuery(id+"F0.wireOp",EDGE,"E12.25.9.0"),sQuery(id+"F0.wireOp",EDGE,"E12.29.9.0"),sQuery(id+"F0.wireOp",EDGE,"E12.32.9.0"),sQuery(id+"F0.wireOp",EDGE,"E12.2.10.0"),sQuery(id+"F0.wireOp",EDGE,"E12.4.10.0"),sQuery(id+"F0.wireOp",EDGE,"E12.7.10.0"),sQuery(id+"F0.wireOp",EDGE,"E12.11.10.0"),sQuery(id+"F0.wireOp",EDGE,"E12.15.10.0"),sQuery(id+"F0.wireOp",EDGE,"E12.18.10.0"),sQuery(id+"F0.wireOp",EDGE,"E12.21.10.0"),sQuery(id+"F0.wireOp",EDGE,"E12.25.10.0"),sQuery(id+"F0.wireOp",EDGE,"E12.29.10.0"),sQuery(id+"F0.wireOp",EDGE,"E12.32.10.0"),sQuery(id+"F0.wireOp",EDGE,"E12.2.11.0"),sQuery(id+"F0.wireOp",EDGE,"E12.4.11.0"),sQuery(id+"F0.wireOp",EDGE,"E12.7.11.0"),sQuery(id+"F0.wireOp",EDGE,"E12.11.11.0"),sQuery(id+"F0.wireOp",EDGE,"E12.15.11.0"),sQuery(id+"F0.wireOp",EDGE,"E12.18.11.0"),sQuery(id+"F0.wireOp",EDGE,"E12.21.11.0"),sQuery(id+"F0.wireOp",EDGE,"E12.25.11.0"),sQuery(id+"F0.wireOp",EDGE,"E12.29.11.0"),sQuery(id+"F0.wireOp",EDGE,"E12.32.11.0"),sQuery(id+"F0.wireOp",EDGE,"E12.2.12.0"),sQuery(id+"F0.wireOp",EDGE,"E12.4.12.0"),sQuery(id+"F0.wireOp",EDGE,"E12.7.12.0"),sQuery(id+"F0.wireOp",EDGE,"E12.11.12.0"),sQuery(id+"F0.wireOp",EDGE,"E12.15.12.0"),sQuery(id+"F0.wireOp",EDGE,"E12.18.12.0"),sQuery(id+"F0.wireOp",EDGE,"E12.21.12.0"),sQuery(id+"F0.wireOp",EDGE,"E12.25.12.0"),sQuery(id+"F0.wireOp",EDGE,"E12.29.12.0"),sQuery(id+"F0.wireOp",EDGE,"E12.32.12.0"),sQuery(id+"F0.wireOp",EDGE,"E12.2.13.0"),sQuery(id+"F0.wireOp",EDGE,"E12.4.13.0"),sQuery(id+"F0.wireOp",EDGE,"E12.7.13.0"),sQuery(id+"F0.wireOp",EDGE,"E12.11.13.0"),sQuery(id+"F0.wireOp",EDGE,"E12.15.13.0"),sQuery(id+"F0.wireOp",EDGE,"E12.18.13.0"),sQuery(id+"F0.wireOp",EDGE,"E12.21.13.0"),sQuery(id+"F0.wireOp",EDGE,"E12.25.13.0"),sQuery(id+"F0.wireOp",EDGE,"E12.29.13.0"),sQuery(id+"F0.wireOp",EDGE,"E12.32.13.0"),sQuery(id+"F0.wireOp",EDGE,"E12.2.14.0"),sQuery(id+"F0.wireOp",EDGE,"E12.4.14.0"),sQuery(id+"F0.wireOp",EDGE,"E12.7.14.0"),sQuery(id+"F0.wireOp",EDGE,"E12.11.14.0"),sQuery(id+"F0.wireOp",EDGE,"E12.15.14.0"),sQuery(id+"F0.wireOp",EDGE,"E12.18.14.0"),sQuery(id+"F0.wireOp",EDGE,"E12.21.14.0"),sQuery(id+"F0.wireOp",EDGE,"E12.25.14.0"),sQuery(id+"F0.wireOp",EDGE,"E12.29.14.0"),sQuery(id+"F0.wireOp",EDGE,"E12.32.14.0"),sQuery(id+"F0.wireOp",EDGE,"E12.2.15.0"),sQuery(id+"F0.wireOp",EDGE,"E12.4.15.0"),sQuery(id+"F0.wireOp",EDGE,"E12.7.15.0"),sQuery(id+"F0.wireOp",EDGE,"E12.11.15.0"),sQuery(id+"F0.wireOp",EDGE,"E12.15.15.0"),sQuery(id+"F0.wireOp",EDGE,"E12.18.15.0"),sQuery(id+"F0.wireOp",EDGE,"E12.21.15.0"),sQuery(id+"F0.wireOp",EDGE,"E12.25.15.0"),sQuery(id+"F0.wireOp",EDGE,"E12.29.15.0"),sQuery(id+"F0.wireOp",EDGE,"E12.32.15.0"),sQuery(id+"F0.wireOp",EDGE,"E12.2.16.0"),sQuery(id+"F0.wireOp",EDGE,"E12.4.16.0"),sQuery(id+"F0.wireOp",EDGE,"E12.7.16.0"),sQuery(id+"F0.wireOp",EDGE,"E12.11.16.0"),sQuery(id+"F0.wireOp",EDGE,"E12.15.16.0"),sQuery(id+"F0.wireOp",EDGE,"E12.18.16.0"),sQuery(id+"F0.wireOp",EDGE,"E12.21.16.0"),sQuery(id+"F0.wireOp",EDGE,"E12.25.16.0"),sQuery(id+"F0.wireOp",EDGE,"E12.29.16.0"),sQuery(id+"F0.wireOp",EDGE,"E12.32.16.0"),sQuery(id+"F0.wireOp",EDGE,"E12.2.17.0"),sQuery(id+"F0.wireOp",EDGE,"E12.4.17.0"),sQuery(id+"F0.wireOp",EDGE,"E12.7.17.0"),sQuery(id+"F0.wireOp",EDGE,"E12.11.17.0"),sQuery(id+"F0.wireOp",EDGE,"E12.15.17.0"),sQuery(id+"F0.wireOp",EDGE,"E12.18.17.0"),sQuery(id+"F0.wireOp",EDGE,"E12.21.17.0"),sQuery(id+"F0.wireOp",EDGE,"E12.25.17.0"),sQuery(id+"F0.wireOp",EDGE,"E12.29.17.0"),sQuery(id+"F0.wireOp",EDGE,"E12.32.17.0"),sQuery(id+"F0.wireOp",EDGE,"E12.2.18.0"),sQuery(id+"F0.wireOp",EDGE,"E12.4.18.0"),sQuery(id+"F0.wireOp",EDGE,"E12.7.18.0"),sQuery(id+"F0.wireOp",EDGE,"E12.11.18.0"),sQuery(id+"F0.wireOp",EDGE,"E12.15.18.0"),sQuery(id+"F0.wireOp",EDGE,"E12.18.18.0"),sQuery(id+"F0.wireOp",EDGE,"E12.21.18.0"),sQuery(id+"F0.wireOp",EDGE,"E12.25.18.0"),sQuery(id+"F0.wireOp",EDGE,"E12.29.18.0"),sQuery(id+"F0.wireOp",EDGE,"E12.32.18.0"),sQuery(id+"F0.wireOp",EDGE,"E12.2.19.0"),sQuery(id+"F0.wireOp",EDGE,"E12.4.19.0"),sQuery(id+"F0.wireOp",EDGE,"E12.7.19.0"),sQuery(id+"F0.wireOp",EDGE,"E12.11.19.0"),sQuery(id+"F0.wireOp",EDGE,"E12.15.19.0"),sQuery(id+"F0.wireOp",EDGE,"E12.18.19.0"),sQuery(id+"F0.wireOp",EDGE,"E12.21.19.0"),sQuery(id+"F0.wireOp",EDGE,"E12.25.19.0"),sQuery(id+"F0.wireOp",EDGE,"E12.29.19.0"),sQuery(id+"F0.wireOp",EDGE,"E12.32.19.0"),sQuery(id+"F0.wireOp",EDGE,"E12.2.20.0"),sQuery(id+"F0.wireOp",EDGE,"E12.4.20.0"),sQuery(id+"F0.wireOp",EDGE,"E12.7.20.0"),sQuery(id+"F0.wireOp",EDGE,"E12.11.20.0"),sQuery(id+"F0.wireOp",EDGE,"E12.15.20.0"),sQuery(id+"F0.wireOp",EDGE,"E12.18.20.0"),sQuery(id+"F0.wireOp",EDGE,"E12.21.20.0"),sQuery(id+"F0.wireOp",EDGE,"E12.25.20.0"),sQuery(id+"F0.wireOp",EDGE,"E12.29.20.0"),sQuery(id+"F0.wireOp",EDGE,"E12.32.20.0"),sQuery(id+"F0.wireOp",EDGE,"E12.2.21.0"),sQuery(id+"F0.wireOp",EDGE,"E12.4.21.0"),sQuery(id+"F0.wireOp",EDGE,"E12.7.21.0"),sQuery(id+"F0.wireOp",EDGE,"E12.11.21.0"),sQuery(id+"F0.wireOp",EDGE,"E12.15.21.0"),sQuery(id+"F0.wireOp",EDGE,"E12.18.21.0"),sQuery(id+"F0.wireOp",EDGE,"E12.21.21.0"),sQuery(id+"F0.wireOp",EDGE,"E12.25.21.0"),sQuery(id+"F0.wireOp",EDGE,"E12.29.21.0"),sQuery(id+"F0.wireOp",EDGE,"E12.32.21.0"),sQuery(id+"F0.wireOp",EDGE,"E12.2.22.0"),sQuery(id+"F0.wireOp",EDGE,"E12.4.22.0"),sQuery(id+"F0.wireOp",EDGE,"E12.7.22.0"),sQuery(id+"F0.wireOp",EDGE,"E12.11.22.0"),sQuery(id+"F0.wireOp",EDGE,"E12.15.22.0"),sQuery(id+"F0.wireOp",EDGE,"E12.18.22.0"),sQuery(id+"F0.wireOp",EDGE,"E12.21.22.0"),sQuery(id+"F0.wireOp",EDGE,"E12.25.22.0"),sQuery(id+"F0.wireOp",EDGE,"E12.29.22.0"),sQuery(id+"F0.wireOp",EDGE,"E12.32.22.0"),sQuery(id+"F0.wireOp",EDGE,"E12.2.23.0"),sQuery(id+"F0.wireOp",EDGE,"E12.4.23.0"),sQuery(id+"F0.wireOp",EDGE,"E12.7.23.0"),sQuery(id+"F0.wireOp",EDGE,"E12.11.23.0"),sQuery(id+"F0.wireOp",EDGE,"E12.15.23.0"),sQuery(id+"F0.wireOp",EDGE,"E12.18.23.0"),sQuery(id+"F0.wireOp",EDGE,"E12.21.23.0"),sQuery(id+"F0.wireOp",EDGE,"E12.25.23.0"),sQuery(id+"F0.wireOp",EDGE,"E12.29.23.0"),sQuery(id+"F0.wireOp",EDGE,"E12.32.23.0"),sQuery(id+"F0.wireOp",EDGE,"E12.2.24.0"),sQuery(id+"F0.wireOp",EDGE,"E12.4.24.0"),sQuery(id+"F0.wireOp",EDGE,"E12.7.24.0"),sQuery(id+"F0.wireOp",EDGE,"E12.11.24.0"),sQuery(id+"F0.wireOp",EDGE,"E12.15.24.0"),sQuery(id+"F0.wireOp",EDGE,"E12.18.24.0"),sQuery(id+"F0.wireOp",EDGE,"E12.21.24.0"),sQuery(id+"F0.wireOp",EDGE,"E12.25.24.0"),sQuery(id+"F0.wireOp",EDGE,"E12.29.24.0"),sQuery(id+"F0.wireOp",EDGE,"E12.32.24.0"),sQuery(id+"F0.wireOp",EDGE,"E12.2.25.0"),sQuery(id+"F0.wireOp",EDGE,"E12.4.25.0"),sQuery(id+"F0.wireOp",EDGE,"E12.7.25.0"),sQuery(id+"F0.wireOp",EDGE,"E12.11.25.0"),sQuery(id+"F0.wireOp",EDGE,"E12.15.25.0"),sQuery(id+"F0.wireOp",EDGE,"E12.18.25.0"),sQuery(id+"F0.wireOp",EDGE,"E12.21.25.0"),sQuery(id+"F0.wireOp",EDGE,"E12.25.25.0"),sQuery(id+"F0.wireOp",EDGE,"E12.29.25.0"),sQuery(id+"F0.wireOp",EDGE,"E12.32.25.0"),sQuery(id+"F0.wireOp",EDGE,"E12.2.26.0"),sQuery(id+"F0.wireOp",EDGE,"E12.4.26.0"),sQuery(id+"F0.wireOp",EDGE,"E12.7.26.0"),sQuery(id+"F0.wireOp",EDGE,"E12.11.26.0"),sQuery(id+"F0.wireOp",EDGE,"E12.15.26.0"),sQuery(id+"F0.wireOp",EDGE,"E12.18.26.0"),sQuery(id+"F0.wireOp",EDGE,"E12.21.26.0"),sQuery(id+"F0.wireOp",EDGE,"E12.25.26.0"),sQuery(id+"F0.wireOp",EDGE,"E12.29.26.0"),sQuery(id+"F0.wireOp",EDGE,"E12.32.26.0"),sQuery(id+"F0.wireOp",EDGE,"E12.2.27.0"),sQuery(id+"F0.wireOp",EDGE,"E12.4.27.0"),sQuery(id+"F0.wireOp",EDGE,"E12.7.27.0"),sQuery(id+"F0.wireOp",EDGE,"E12.11.27.0"),sQuery(id+"F0.wireOp",EDGE,"E12.15.27.0"),sQuery(id+"F0.wireOp",EDGE,"E12.18.27.0"),sQuery(id+"F0.wireOp",EDGE,"E12.21.27.0"),sQuery(id+"F0.wireOp",EDGE,"E12.25.27.0"),sQuery(id+"F0.wireOp",EDGE,"E12.29.27.0"),sQuery(id+"F0.wireOp",EDGE,"E12.32.27.0"),sQuery(id+"F0.wireOp",EDGE,"E12.2.28.0"),sQuery(id+"F0.wireOp",EDGE,"E12.4.28.0"),sQuery(id+"F0.wireOp",EDGE,"E12.7.28.0"),sQuery(id+"F0.wireOp",EDGE,"E12.11.28.0"),sQuery(id+"F0.wireOp",EDGE,"E12.15.28.0"),sQuery(id+"F0.wireOp",EDGE,"E12.18.28.0"),sQuery(id+"F0.wireOp",EDGE,"E12.21.28.0"),sQuery(id+"F0.wireOp",EDGE,"E12.25.28.0"),sQuery(id+"F0.wireOp",EDGE,"E12.29.28.0"),sQuery(id+"F0.wireOp",EDGE,"E12.32.28.0"),sQuery(id+"F0.wireOp",EDGE,"E12.2.29.0"),sQuery(id+"F0.wireOp",EDGE,"E12.4.29.0"),sQuery(id+"F0.wireOp",EDGE,"E12.7.29.0"),sQuery(id+"F0.wireOp",EDGE,"E12.11.29.0"),sQuery(id+"F0.wireOp",EDGE,"E12.15.29.0"),sQuery(id+"F0.wireOp",EDGE,"E12.18.29.0"),sQuery(id+"F0.wireOp",EDGE,"E12.21.29.0"),sQuery(id+"F0.wireOp",EDGE,"E12.25.29.0"),sQuery(id+"F0.wireOp",EDGE,"E12.29.29.0"),sQuery(id+"F0.wireOp",EDGE,"E12.32.29.0"),sQuery(id+"F0.wireOp",EDGE,"E12.2.30.0"),sQuery(id+"F0.wireOp",EDGE,"E12.4.30.0"),sQuery(id+"F0.wireOp",EDGE,"E12.7.30.0"),sQuery(id+"F0.wireOp",EDGE,"E12.11.30.0"),sQuery(id+"F0.wireOp",EDGE,"E12.15.30.0"),sQuery(id+"F0.wireOp",EDGE,"E12.18.30.0"),sQuery(id+"F0.wireOp",EDGE,"E12.21.30.0"),sQuery(id+"F0.wireOp",EDGE,"E12.25.30.0"),sQuery(id+"F0.wireOp",EDGE,"E12.29.30.0"),sQuery(id+"F0.wireOp",EDGE,"E12.32.30.0"),sQuery(id+"F0.wireOp",EDGE,"E12.2.31.0"),sQuery(id+"F0.wireOp",EDGE,"E12.4.31.0"),sQuery(id+"F0.wireOp",EDGE,"E12.7.31.0"),sQuery(id+"F0.wireOp",EDGE,"E12.11.31.0"),sQuery(id+"F0.wireOp",EDGE,"E12.15.31.0"),sQuery(id+"F0.wireOp",EDGE,"E12.18.31.0"),sQuery(id+"F0.wireOp",EDGE,"E12.21.31.0"),sQuery(id+"F0.wireOp",EDGE,"E12.25.31.0"),sQuery(id+"F0.wireOp",EDGE,"E12.29.31.0"),sQuery(id+"F0.wireOp",EDGE,"E12.32.31.0"),sQuery(id+"F0.wireOp",EDGE,"E12.2.32.0"),sQuery(id+"F0.wireOp",EDGE,"E12.4.32.0"),sQuery(id+"F0.wireOp",EDGE,"E12.7.32.0"),sQuery(id+"F0.wireOp",EDGE,"E12.11.32.0"),sQuery(id+"F0.wireOp",EDGE,"E12.15.32.0"),sQuery(id+"F0.wireOp",EDGE,"E12.18.32.0"),sQuery(id+"F0.wireOp",EDGE,"E12.21.32.0"),sQuery(id+"F0.wireOp",EDGE,"E12.25.32.0"),sQuery(id+"F0.wireOp",EDGE,"E12.29.32.0"),sQuery(id+"F0.wireOp",EDGE,"E12.32.32.0"),sQuery(id+"F0.wireOp",EDGE,"E12.2.33.0"),sQuery(id+"F0.wireOp",EDGE,"E12.4.33.0"),sQuery(id+"F0.wireOp",EDGE,"E12.7.33.0"),sQuery(id+"F0.wireOp",EDGE,"E12.11.33.0"),sQuery(id+"F0.wireOp",EDGE,"E12.15.33.0"),sQuery(id+"F0.wireOp",EDGE,"E12.18.33.0"),sQuery(id+"F0.wireOp",EDGE,"E12.21.33.0"),sQuery(id+"F0.wireOp",EDGE,"E12.25.33.0"),sQuery(id+"F0.wireOp",EDGE,"E12.29.33.0"),sQuery(id+"F0.wireOp",EDGE,"E12.32.33.0"),sQuery(id+"F0.wireOp",EDGE,"E12.2.34.0"),sQuery(id+"F0.wireOp",EDGE,"E12.4.34.0"),sQuery(id+"F0.wireOp",EDGE,"E12.7.34.0"),sQuery(id+"F0.wireOp",EDGE,"E12.11.34.0"),sQuery(id+"F0.wireOp",EDGE,"E12.15.34.0"),sQuery(id+"F0.wireOp",EDGE,"E12.18.34.0"),sQuery(id+"F0.wireOp",EDGE,"E12.21.34.0"),sQuery(id+"F0.wireOp",EDGE,"E12.25.34.0"),sQuery(id+"F0.wireOp",EDGE,"E12.29.34.0"),sQuery(id+"F0.wireOp",EDGE,"E12.32.34.0"),sQuery(id+"F0.wireOp",EDGE,"E12.2.35.0"),sQuery(id+"F0.wireOp",EDGE,"E12.4.35.0"),sQuery(id+"F0.wireOp",EDGE,"E12.7.35.0"),sQuery(id+"F0.wireOp",EDGE,"E12.11.35.0"),sQuery(id+"F0.wireOp",EDGE,"E12.15.35.0"),sQuery(id+"F0.wireOp",EDGE,"E12.18.35.0"),sQuery(id+"F0.wireOp",EDGE,"E12.21.35.0"),sQuery(id+"F0.wireOp",EDGE,"E12.25.35.0"),sQuery(id+"F0.wireOp",EDGE,"E12.29.35.0"),sQuery(id+"F0.wireOp",EDGE,"E12.32.35.0"),sQuery(id+"F0.wireOp",EDGE,"E13.trimOffspring"),sQuery(id+"F0.wireOp",EDGE,"E14.trimOffspring"),sQuery(id+"F0.wireOp",EDGE,"E15.trimOffspring"),sQuery(id+"F0.wireOp",EDGE,"E16.trimOffspring"),sQuery(id+"F0.wireOp",EDGE,"E17.trimOffspring"),sQuery(id+"F0.wireOp",EDGE,"E18.trimOffspring"),sQuery(id+"F0.wireOp",EDGE,"E19.trimOffspring"),sQuery(id+"F0.wireOp",EDGE,"E20.trimOffspring"),sQuery(id+"F0.wireOp",EDGE,"E21.trimOffspring"),sQuery(id+"F0.wireOp",EDGE,"E22.trimOffspring"),sQuery(id+"F0.wireOp",EDGE,"E23.trimOffspring"),sQuery(id+"F0.wireOp",EDGE,"E24.trimOffspring"),sQuery(id+"F0.wireOp",EDGE,"E25.trimOffspring"),sQuery(id+"F0.wireOp",EDGE,"E26.trimOffspring"),sQuery(id+"F0.wireOp",EDGE,"E27.trimOffspring"),sQuery(id+"F0.wireOp",EDGE,"E28.trimOffspring"),sQuery(id+"F0.wireOp",EDGE,"E29.trimOffspring"),sQuery(id+"F0.wireOp",EDGE,"E30.trimOffspring"),sQuery(id+"F0.wireOp",EDGE,"E31.trimOffspring"),sQuery(id+"F0.wireOp",EDGE,"E32.trimOffspring"),sQuery(id+"F0.wireOp",EDGE,"E33.trimOffspring"),sQuery(id+"F0.wireOp",EDGE,"E34.trimOffspring"),sQuery(id+"F0.wireOp",EDGE,"E35.trimOffspring"),sQuery(id+"F0.wireOp",EDGE,"E36.trimOffspring"),sQuery(id+"F0.wireOp",EDGE,"E37.trimOffspring"),sQuery(id+"F0.wireOp",EDGE,"E38.trimOffspring"),sQuery(id+"F0.wireOp",EDGE,"E39.trimOffspring"),sQuery(id+"F0.wireOp",EDGE,"E40.trimOffspring"),sQuery(id+"F0.wireOp",EDGE,"E41.trimOffspring"),sQuery(id+"F0.wireOp",EDGE,"E42.trimOffspring"),sQuery(id+"F0.wireOp",EDGE,"E43.trimOffspring"),sQuery(id+"F0.wireOp",EDGE,"E44.trimOffspring"),sQuery(id+"F0.wireOp",EDGE,"E45.trimOffspring"),sQuery(id+"F0.wireOp",EDGE,"E46.trimOffspring"),sQuery(id+"F0.wireOp",EDGE,"E47.trimOffspring")])],"isStart":true}),makeQuery(id+"F7.hole-2.opRevolve","SWEPT_FACE",FACE,{"disambiguationData":[OSD([sQuery(id+"F7.hole-2.sketch.wireOp",EDGE,"core_line_2")])]})]});
            var Q24;
            Q24=makeQuery(id+"F7.hole-2.boolean.opBoolean","COPY",EDGE,{"derivedFrom":makeQuery(id+"F7.hole-2.opRevolve","SWEPT_EDGE",EDGE,{"disambiguationData":[OSD([sQuery(id+"F7.hole-2.sketch.wireOp",EDGE,"cbore_start_line_2"),sQuery(id+"F7.hole-2.sketch.wireOp",EDGE,"cbore_start_line_3")])]})});
            var Q25;
            Q25=makeQuery(id+"F7.hole-3.boolean.opBoolean","COPY",EDGE,{"derivedFrom":makeQuery(id+"F7.hole-3.opRevolve","SWEPT_EDGE",EDGE,{"disambiguationData":[OSD([sQuery(id+"F7.hole-3.sketch.wireOp",EDGE,"cbore_start_line_2"),sQuery(id+"F7.hole-3.sketch.wireOp",EDGE,"cbore_start_line_3")])]})});
            var Q26;
            Q26=makeQuery(id+"F7.hole-3.boolean.opBoolean","INTERSECT",EDGE,{"derivedFrom":[makeQuery(id+"F1.opExtrude","CAP_FACE",FACE,{"disambiguationData":[OSD([sQuery(id+"F0.wireOp",EDGE,"E0"),sQuery(id+"F0.wireOp",EDGE,"E1.trimOffspring"),sQuery(id+"F0.wireOp",EDGE,"E2"),sQuery(id+"F0.wireOp",EDGE,"E3"),sQuery(id+"F0.wireOp",EDGE,"E4.MirrorCS"),sQuery(id+"F0.wireOp",EDGE,"E5.MirrorCS"),sQuery(id+"F0.wireOp",EDGE,"E6.MirrorCS"),sQuery(id+"F0.wireOp",EDGE,"E7.filletArc"),sQuery(id+"F0.wireOp",EDGE,"E8.filletArc"),sQuery(id+"F0.wireOp",EDGE,"E9.filletArc"),sQuery(id+"F0.wireOp",EDGE,"E10.filletArc"),sQuery(id+"F0.wireOp",EDGE,"E11.1.0"),sQuery(id+"F0.wireOp",EDGE,"E11.1.1"),sQuery(id+"F0.wireOp",EDGE,"E11.1.2"),sQuery(id+"F0.wireOp",EDGE,"E11.1.3"),sQuery(id+"F0.wireOp",EDGE,"E11.1.4"),sQuery(id+"F0.wireOp",EDGE,"E11.1.5"),sQuery(id+"F0.wireOp",EDGE,"E11.1.6"),sQuery(id+"F0.wireOp",EDGE,"E11.1.7"),sQuery(id+"F0.wireOp",EDGE,"E11.1.8"),sQuery(id+"F0.wireOp",EDGE,"E11.1.9"),sQuery(id+"F0.wireOp",EDGE,"E11.2.0"),sQuery(id+"F0.wireOp",EDGE,"E11.2.1"),sQuery(id+"F0.wireOp",EDGE,"E11.2.2"),sQuery(id+"F0.wireOp",EDGE,"E11.2.3"),sQuery(id+"F0.wireOp",EDGE,"E11.2.4"),sQuery(id+"F0.wireOp",EDGE,"E11.2.5"),sQuery(id+"F0.wireOp",EDGE,"E11.2.6"),sQuery(id+"F0.wireOp",EDGE,"E11.2.7"),sQuery(id+"F0.wireOp",EDGE,"E11.2.8"),sQuery(id+"F0.wireOp",EDGE,"E11.2.9"),sQuery(id+"F0.wireOp",EDGE,"E12.2.3.0"),sQuery(id+"F0.wireOp",EDGE,"E12.4.3.0"),sQuery(id+"F0.wireOp",EDGE,"E12.7.3.0"),sQuery(id+"F0.wireOp",EDGE,"E12.11.3.0"),sQuery(id+"F0.wireOp",EDGE,"E12.15.3.0"),sQuery(id+"F0.wireOp",EDGE,"E12.18.3.0"),sQuery(id+"F0.wireOp",EDGE,"E12.21.3.0"),sQuery(id+"F0.wireOp",EDGE,"E12.25.3.0"),sQuery(id+"F0.wireOp",EDGE,"E12.29.3.0"),sQuery(id+"F0.wireOp",EDGE,"E12.32.3.0"),sQuery(id+"F0.wireOp",EDGE,"E12.2.4.0"),sQuery(id+"F0.wireOp",EDGE,"E12.4.4.0"),sQuery(id+"F0.wireOp",EDGE,"E12.7.4.0"),sQuery(id+"F0.wireOp",EDGE,"E12.11.4.0"),sQuery(id+"F0.wireOp",EDGE,"E12.15.4.0"),sQuery(id+"F0.wireOp",EDGE,"E12.18.4.0"),sQuery(id+"F0.wireOp",EDGE,"E12.21.4.0"),sQuery(id+"F0.wireOp",EDGE,"E12.25.4.0"),sQuery(id+"F0.wireOp",EDGE,"E12.29.4.0"),sQuery(id+"F0.wireOp",EDGE,"E12.32.4.0"),sQuery(id+"F0.wireOp",EDGE,"E12.2.5.0"),sQuery(id+"F0.wireOp",EDGE,"E12.4.5.0"),sQuery(id+"F0.wireOp",EDGE,"E12.7.5.0"),sQuery(id+"F0.wireOp",EDGE,"E12.11.5.0"),sQuery(id+"F0.wireOp",EDGE,"E12.15.5.0"),sQuery(id+"F0.wireOp",EDGE,"E12.18.5.0"),sQuery(id+"F0.wireOp",EDGE,"E12.21.5.0"),sQuery(id+"F0.wireOp",EDGE,"E12.25.5.0"),sQuery(id+"F0.wireOp",EDGE,"E12.29.5.0"),sQuery(id+"F0.wireOp",EDGE,"E12.32.5.0"),sQuery(id+"F0.wireOp",EDGE,"E12.2.6.0"),sQuery(id+"F0.wireOp",EDGE,"E12.4.6.0"),sQuery(id+"F0.wireOp",EDGE,"E12.7.6.0"),sQuery(id+"F0.wireOp",EDGE,"E12.11.6.0"),sQuery(id+"F0.wireOp",EDGE,"E12.15.6.0"),sQuery(id+"F0.wireOp",EDGE,"E12.18.6.0"),sQuery(id+"F0.wireOp",EDGE,"E12.21.6.0"),sQuery(id+"F0.wireOp",EDGE,"E12.25.6.0"),sQuery(id+"F0.wireOp",EDGE,"E12.29.6.0"),sQuery(id+"F0.wireOp",EDGE,"E12.32.6.0"),sQuery(id+"F0.wireOp",EDGE,"E12.2.7.0"),sQuery(id+"F0.wireOp",EDGE,"E12.4.7.0"),sQuery(id+"F0.wireOp",EDGE,"E12.7.7.0"),sQuery(id+"F0.wireOp",EDGE,"E12.11.7.0"),sQuery(id+"F0.wireOp",EDGE,"E12.15.7.0"),sQuery(id+"F0.wireOp",EDGE,"E12.18.7.0"),sQuery(id+"F0.wireOp",EDGE,"E12.21.7.0"),sQuery(id+"F0.wireOp",EDGE,"E12.25.7.0"),sQuery(id+"F0.wireOp",EDGE,"E12.29.7.0"),sQuery(id+"F0.wireOp",EDGE,"E12.32.7.0"),sQuery(id+"F0.wireOp",EDGE,"E12.2.8.0"),sQuery(id+"F0.wireOp",EDGE,"E12.4.8.0"),sQuery(id+"F0.wireOp",EDGE,"E12.7.8.0"),sQuery(id+"F0.wireOp",EDGE,"E12.11.8.0"),sQuery(id+"F0.wireOp",EDGE,"E12.15.8.0"),sQuery(id+"F0.wireOp",EDGE,"E12.18.8.0"),sQuery(id+"F0.wireOp",EDGE,"E12.21.8.0"),sQuery(id+"F0.wireOp",EDGE,"E12.25.8.0"),sQuery(id+"F0.wireOp",EDGE,"E12.29.8.0"),sQuery(id+"F0.wireOp",EDGE,"E12.32.8.0"),sQuery(id+"F0.wireOp",EDGE,"E12.2.9.0"),sQuery(id+"F0.wireOp",EDGE,"E12.4.9.0"),sQuery(id+"F0.wireOp",EDGE,"E12.7.9.0"),sQuery(id+"F0.wireOp",EDGE,"E12.11.9.0"),sQuery(id+"F0.wireOp",EDGE,"E12.15.9.0"),sQuery(id+"F0.wireOp",EDGE,"E12.18.9.0"),sQuery(id+"F0.wireOp",EDGE,"E12.21.9.0"),sQuery(id+"F0.wireOp",EDGE,"E12.25.9.0"),sQuery(id+"F0.wireOp",EDGE,"E12.29.9.0"),sQuery(id+"F0.wireOp",EDGE,"E12.32.9.0"),sQuery(id+"F0.wireOp",EDGE,"E12.2.10.0"),sQuery(id+"F0.wireOp",EDGE,"E12.4.10.0"),sQuery(id+"F0.wireOp",EDGE,"E12.7.10.0"),sQuery(id+"F0.wireOp",EDGE,"E12.11.10.0"),sQuery(id+"F0.wireOp",EDGE,"E12.15.10.0"),sQuery(id+"F0.wireOp",EDGE,"E12.18.10.0"),sQuery(id+"F0.wireOp",EDGE,"E12.21.10.0"),sQuery(id+"F0.wireOp",EDGE,"E12.25.10.0"),sQuery(id+"F0.wireOp",EDGE,"E12.29.10.0"),sQuery(id+"F0.wireOp",EDGE,"E12.32.10.0"),sQuery(id+"F0.wireOp",EDGE,"E12.2.11.0"),sQuery(id+"F0.wireOp",EDGE,"E12.4.11.0"),sQuery(id+"F0.wireOp",EDGE,"E12.7.11.0"),sQuery(id+"F0.wireOp",EDGE,"E12.11.11.0"),sQuery(id+"F0.wireOp",EDGE,"E12.15.11.0"),sQuery(id+"F0.wireOp",EDGE,"E12.18.11.0"),sQuery(id+"F0.wireOp",EDGE,"E12.21.11.0"),sQuery(id+"F0.wireOp",EDGE,"E12.25.11.0"),sQuery(id+"F0.wireOp",EDGE,"E12.29.11.0"),sQuery(id+"F0.wireOp",EDGE,"E12.32.11.0"),sQuery(id+"F0.wireOp",EDGE,"E12.2.12.0"),sQuery(id+"F0.wireOp",EDGE,"E12.4.12.0"),sQuery(id+"F0.wireOp",EDGE,"E12.7.12.0"),sQuery(id+"F0.wireOp",EDGE,"E12.11.12.0"),sQuery(id+"F0.wireOp",EDGE,"E12.15.12.0"),sQuery(id+"F0.wireOp",EDGE,"E12.18.12.0"),sQuery(id+"F0.wireOp",EDGE,"E12.21.12.0"),sQuery(id+"F0.wireOp",EDGE,"E12.25.12.0"),sQuery(id+"F0.wireOp",EDGE,"E12.29.12.0"),sQuery(id+"F0.wireOp",EDGE,"E12.32.12.0"),sQuery(id+"F0.wireOp",EDGE,"E12.2.13.0"),sQuery(id+"F0.wireOp",EDGE,"E12.4.13.0"),sQuery(id+"F0.wireOp",EDGE,"E12.7.13.0"),sQuery(id+"F0.wireOp",EDGE,"E12.11.13.0"),sQuery(id+"F0.wireOp",EDGE,"E12.15.13.0"),sQuery(id+"F0.wireOp",EDGE,"E12.18.13.0"),sQuery(id+"F0.wireOp",EDGE,"E12.21.13.0"),sQuery(id+"F0.wireOp",EDGE,"E12.25.13.0"),sQuery(id+"F0.wireOp",EDGE,"E12.29.13.0"),sQuery(id+"F0.wireOp",EDGE,"E12.32.13.0"),sQuery(id+"F0.wireOp",EDGE,"E12.2.14.0"),sQuery(id+"F0.wireOp",EDGE,"E12.4.14.0"),sQuery(id+"F0.wireOp",EDGE,"E12.7.14.0"),sQuery(id+"F0.wireOp",EDGE,"E12.11.14.0"),sQuery(id+"F0.wireOp",EDGE,"E12.15.14.0"),sQuery(id+"F0.wireOp",EDGE,"E12.18.14.0"),sQuery(id+"F0.wireOp",EDGE,"E12.21.14.0"),sQuery(id+"F0.wireOp",EDGE,"E12.25.14.0"),sQuery(id+"F0.wireOp",EDGE,"E12.29.14.0"),sQuery(id+"F0.wireOp",EDGE,"E12.32.14.0"),sQuery(id+"F0.wireOp",EDGE,"E12.2.15.0"),sQuery(id+"F0.wireOp",EDGE,"E12.4.15.0"),sQuery(id+"F0.wireOp",EDGE,"E12.7.15.0"),sQuery(id+"F0.wireOp",EDGE,"E12.11.15.0"),sQuery(id+"F0.wireOp",EDGE,"E12.15.15.0"),sQuery(id+"F0.wireOp",EDGE,"E12.18.15.0"),sQuery(id+"F0.wireOp",EDGE,"E12.21.15.0"),sQuery(id+"F0.wireOp",EDGE,"E12.25.15.0"),sQuery(id+"F0.wireOp",EDGE,"E12.29.15.0"),sQuery(id+"F0.wireOp",EDGE,"E12.32.15.0"),sQuery(id+"F0.wireOp",EDGE,"E12.2.16.0"),sQuery(id+"F0.wireOp",EDGE,"E12.4.16.0"),sQuery(id+"F0.wireOp",EDGE,"E12.7.16.0"),sQuery(id+"F0.wireOp",EDGE,"E12.11.16.0"),sQuery(id+"F0.wireOp",EDGE,"E12.15.16.0"),sQuery(id+"F0.wireOp",EDGE,"E12.18.16.0"),sQuery(id+"F0.wireOp",EDGE,"E12.21.16.0"),sQuery(id+"F0.wireOp",EDGE,"E12.25.16.0"),sQuery(id+"F0.wireOp",EDGE,"E12.29.16.0"),sQuery(id+"F0.wireOp",EDGE,"E12.32.16.0"),sQuery(id+"F0.wireOp",EDGE,"E12.2.17.0"),sQuery(id+"F0.wireOp",EDGE,"E12.4.17.0"),sQuery(id+"F0.wireOp",EDGE,"E12.7.17.0"),sQuery(id+"F0.wireOp",EDGE,"E12.11.17.0"),sQuery(id+"F0.wireOp",EDGE,"E12.15.17.0"),sQuery(id+"F0.wireOp",EDGE,"E12.18.17.0"),sQuery(id+"F0.wireOp",EDGE,"E12.21.17.0"),sQuery(id+"F0.wireOp",EDGE,"E12.25.17.0"),sQuery(id+"F0.wireOp",EDGE,"E12.29.17.0"),sQuery(id+"F0.wireOp",EDGE,"E12.32.17.0"),sQuery(id+"F0.wireOp",EDGE,"E12.2.18.0"),sQuery(id+"F0.wireOp",EDGE,"E12.4.18.0"),sQuery(id+"F0.wireOp",EDGE,"E12.7.18.0"),sQuery(id+"F0.wireOp",EDGE,"E12.11.18.0"),sQuery(id+"F0.wireOp",EDGE,"E12.15.18.0"),sQuery(id+"F0.wireOp",EDGE,"E12.18.18.0"),sQuery(id+"F0.wireOp",EDGE,"E12.21.18.0"),sQuery(id+"F0.wireOp",EDGE,"E12.25.18.0"),sQuery(id+"F0.wireOp",EDGE,"E12.29.18.0"),sQuery(id+"F0.wireOp",EDGE,"E12.32.18.0"),sQuery(id+"F0.wireOp",EDGE,"E12.2.19.0"),sQuery(id+"F0.wireOp",EDGE,"E12.4.19.0"),sQuery(id+"F0.wireOp",EDGE,"E12.7.19.0"),sQuery(id+"F0.wireOp",EDGE,"E12.11.19.0"),sQuery(id+"F0.wireOp",EDGE,"E12.15.19.0"),sQuery(id+"F0.wireOp",EDGE,"E12.18.19.0"),sQuery(id+"F0.wireOp",EDGE,"E12.21.19.0"),sQuery(id+"F0.wireOp",EDGE,"E12.25.19.0"),sQuery(id+"F0.wireOp",EDGE,"E12.29.19.0"),sQuery(id+"F0.wireOp",EDGE,"E12.32.19.0"),sQuery(id+"F0.wireOp",EDGE,"E12.2.20.0"),sQuery(id+"F0.wireOp",EDGE,"E12.4.20.0"),sQuery(id+"F0.wireOp",EDGE,"E12.7.20.0"),sQuery(id+"F0.wireOp",EDGE,"E12.11.20.0"),sQuery(id+"F0.wireOp",EDGE,"E12.15.20.0"),sQuery(id+"F0.wireOp",EDGE,"E12.18.20.0"),sQuery(id+"F0.wireOp",EDGE,"E12.21.20.0"),sQuery(id+"F0.wireOp",EDGE,"E12.25.20.0"),sQuery(id+"F0.wireOp",EDGE,"E12.29.20.0"),sQuery(id+"F0.wireOp",EDGE,"E12.32.20.0"),sQuery(id+"F0.wireOp",EDGE,"E12.2.21.0"),sQuery(id+"F0.wireOp",EDGE,"E12.4.21.0"),sQuery(id+"F0.wireOp",EDGE,"E12.7.21.0"),sQuery(id+"F0.wireOp",EDGE,"E12.11.21.0"),sQuery(id+"F0.wireOp",EDGE,"E12.15.21.0"),sQuery(id+"F0.wireOp",EDGE,"E12.18.21.0"),sQuery(id+"F0.wireOp",EDGE,"E12.21.21.0"),sQuery(id+"F0.wireOp",EDGE,"E12.25.21.0"),sQuery(id+"F0.wireOp",EDGE,"E12.29.21.0"),sQuery(id+"F0.wireOp",EDGE,"E12.32.21.0"),sQuery(id+"F0.wireOp",EDGE,"E12.2.22.0"),sQuery(id+"F0.wireOp",EDGE,"E12.4.22.0"),sQuery(id+"F0.wireOp",EDGE,"E12.7.22.0"),sQuery(id+"F0.wireOp",EDGE,"E12.11.22.0"),sQuery(id+"F0.wireOp",EDGE,"E12.15.22.0"),sQuery(id+"F0.wireOp",EDGE,"E12.18.22.0"),sQuery(id+"F0.wireOp",EDGE,"E12.21.22.0"),sQuery(id+"F0.wireOp",EDGE,"E12.25.22.0"),sQuery(id+"F0.wireOp",EDGE,"E12.29.22.0"),sQuery(id+"F0.wireOp",EDGE,"E12.32.22.0"),sQuery(id+"F0.wireOp",EDGE,"E12.2.23.0"),sQuery(id+"F0.wireOp",EDGE,"E12.4.23.0"),sQuery(id+"F0.wireOp",EDGE,"E12.7.23.0"),sQuery(id+"F0.wireOp",EDGE,"E12.11.23.0"),sQuery(id+"F0.wireOp",EDGE,"E12.15.23.0"),sQuery(id+"F0.wireOp",EDGE,"E12.18.23.0"),sQuery(id+"F0.wireOp",EDGE,"E12.21.23.0"),sQuery(id+"F0.wireOp",EDGE,"E12.25.23.0"),sQuery(id+"F0.wireOp",EDGE,"E12.29.23.0"),sQuery(id+"F0.wireOp",EDGE,"E12.32.23.0"),sQuery(id+"F0.wireOp",EDGE,"E12.2.24.0"),sQuery(id+"F0.wireOp",EDGE,"E12.4.24.0"),sQuery(id+"F0.wireOp",EDGE,"E12.7.24.0"),sQuery(id+"F0.wireOp",EDGE,"E12.11.24.0"),sQuery(id+"F0.wireOp",EDGE,"E12.15.24.0"),sQuery(id+"F0.wireOp",EDGE,"E12.18.24.0"),sQuery(id+"F0.wireOp",EDGE,"E12.21.24.0"),sQuery(id+"F0.wireOp",EDGE,"E12.25.24.0"),sQuery(id+"F0.wireOp",EDGE,"E12.29.24.0"),sQuery(id+"F0.wireOp",EDGE,"E12.32.24.0"),sQuery(id+"F0.wireOp",EDGE,"E12.2.25.0"),sQuery(id+"F0.wireOp",EDGE,"E12.4.25.0"),sQuery(id+"F0.wireOp",EDGE,"E12.7.25.0"),sQuery(id+"F0.wireOp",EDGE,"E12.11.25.0"),sQuery(id+"F0.wireOp",EDGE,"E12.15.25.0"),sQuery(id+"F0.wireOp",EDGE,"E12.18.25.0"),sQuery(id+"F0.wireOp",EDGE,"E12.21.25.0"),sQuery(id+"F0.wireOp",EDGE,"E12.25.25.0"),sQuery(id+"F0.wireOp",EDGE,"E12.29.25.0"),sQuery(id+"F0.wireOp",EDGE,"E12.32.25.0"),sQuery(id+"F0.wireOp",EDGE,"E12.2.26.0"),sQuery(id+"F0.wireOp",EDGE,"E12.4.26.0"),sQuery(id+"F0.wireOp",EDGE,"E12.7.26.0"),sQuery(id+"F0.wireOp",EDGE,"E12.11.26.0"),sQuery(id+"F0.wireOp",EDGE,"E12.15.26.0"),sQuery(id+"F0.wireOp",EDGE,"E12.18.26.0"),sQuery(id+"F0.wireOp",EDGE,"E12.21.26.0"),sQuery(id+"F0.wireOp",EDGE,"E12.25.26.0"),sQuery(id+"F0.wireOp",EDGE,"E12.29.26.0"),sQuery(id+"F0.wireOp",EDGE,"E12.32.26.0"),sQuery(id+"F0.wireOp",EDGE,"E12.2.27.0"),sQuery(id+"F0.wireOp",EDGE,"E12.4.27.0"),sQuery(id+"F0.wireOp",EDGE,"E12.7.27.0"),sQuery(id+"F0.wireOp",EDGE,"E12.11.27.0"),sQuery(id+"F0.wireOp",EDGE,"E12.15.27.0"),sQuery(id+"F0.wireOp",EDGE,"E12.18.27.0"),sQuery(id+"F0.wireOp",EDGE,"E12.21.27.0"),sQuery(id+"F0.wireOp",EDGE,"E12.25.27.0"),sQuery(id+"F0.wireOp",EDGE,"E12.29.27.0"),sQuery(id+"F0.wireOp",EDGE,"E12.32.27.0"),sQuery(id+"F0.wireOp",EDGE,"E12.2.28.0"),sQuery(id+"F0.wireOp",EDGE,"E12.4.28.0"),sQuery(id+"F0.wireOp",EDGE,"E12.7.28.0"),sQuery(id+"F0.wireOp",EDGE,"E12.11.28.0"),sQuery(id+"F0.wireOp",EDGE,"E12.15.28.0"),sQuery(id+"F0.wireOp",EDGE,"E12.18.28.0"),sQuery(id+"F0.wireOp",EDGE,"E12.21.28.0"),sQuery(id+"F0.wireOp",EDGE,"E12.25.28.0"),sQuery(id+"F0.wireOp",EDGE,"E12.29.28.0"),sQuery(id+"F0.wireOp",EDGE,"E12.32.28.0"),sQuery(id+"F0.wireOp",EDGE,"E12.2.29.0"),sQuery(id+"F0.wireOp",EDGE,"E12.4.29.0"),sQuery(id+"F0.wireOp",EDGE,"E12.7.29.0"),sQuery(id+"F0.wireOp",EDGE,"E12.11.29.0"),sQuery(id+"F0.wireOp",EDGE,"E12.15.29.0"),sQuery(id+"F0.wireOp",EDGE,"E12.18.29.0"),sQuery(id+"F0.wireOp",EDGE,"E12.21.29.0"),sQuery(id+"F0.wireOp",EDGE,"E12.25.29.0"),sQuery(id+"F0.wireOp",EDGE,"E12.29.29.0"),sQuery(id+"F0.wireOp",EDGE,"E12.32.29.0"),sQuery(id+"F0.wireOp",EDGE,"E12.2.30.0"),sQuery(id+"F0.wireOp",EDGE,"E12.4.30.0"),sQuery(id+"F0.wireOp",EDGE,"E12.7.30.0"),sQuery(id+"F0.wireOp",EDGE,"E12.11.30.0"),sQuery(id+"F0.wireOp",EDGE,"E12.15.30.0"),sQuery(id+"F0.wireOp",EDGE,"E12.18.30.0"),sQuery(id+"F0.wireOp",EDGE,"E12.21.30.0"),sQuery(id+"F0.wireOp",EDGE,"E12.25.30.0"),sQuery(id+"F0.wireOp",EDGE,"E12.29.30.0"),sQuery(id+"F0.wireOp",EDGE,"E12.32.30.0"),sQuery(id+"F0.wireOp",EDGE,"E12.2.31.0"),sQuery(id+"F0.wireOp",EDGE,"E12.4.31.0"),sQuery(id+"F0.wireOp",EDGE,"E12.7.31.0"),sQuery(id+"F0.wireOp",EDGE,"E12.11.31.0"),sQuery(id+"F0.wireOp",EDGE,"E12.15.31.0"),sQuery(id+"F0.wireOp",EDGE,"E12.18.31.0"),sQuery(id+"F0.wireOp",EDGE,"E12.21.31.0"),sQuery(id+"F0.wireOp",EDGE,"E12.25.31.0"),sQuery(id+"F0.wireOp",EDGE,"E12.29.31.0"),sQuery(id+"F0.wireOp",EDGE,"E12.32.31.0"),sQuery(id+"F0.wireOp",EDGE,"E12.2.32.0"),sQuery(id+"F0.wireOp",EDGE,"E12.4.32.0"),sQuery(id+"F0.wireOp",EDGE,"E12.7.32.0"),sQuery(id+"F0.wireOp",EDGE,"E12.11.32.0"),sQuery(id+"F0.wireOp",EDGE,"E12.15.32.0"),sQuery(id+"F0.wireOp",EDGE,"E12.18.32.0"),sQuery(id+"F0.wireOp",EDGE,"E12.21.32.0"),sQuery(id+"F0.wireOp",EDGE,"E12.25.32.0"),sQuery(id+"F0.wireOp",EDGE,"E12.29.32.0"),sQuery(id+"F0.wireOp",EDGE,"E12.32.32.0"),sQuery(id+"F0.wireOp",EDGE,"E12.2.33.0"),sQuery(id+"F0.wireOp",EDGE,"E12.4.33.0"),sQuery(id+"F0.wireOp",EDGE,"E12.7.33.0"),sQuery(id+"F0.wireOp",EDGE,"E12.11.33.0"),sQuery(id+"F0.wireOp",EDGE,"E12.15.33.0"),sQuery(id+"F0.wireOp",EDGE,"E12.18.33.0"),sQuery(id+"F0.wireOp",EDGE,"E12.21.33.0"),sQuery(id+"F0.wireOp",EDGE,"E12.25.33.0"),sQuery(id+"F0.wireOp",EDGE,"E12.29.33.0"),sQuery(id+"F0.wireOp",EDGE,"E12.32.33.0"),sQuery(id+"F0.wireOp",EDGE,"E12.2.34.0"),sQuery(id+"F0.wireOp",EDGE,"E12.4.34.0"),sQuery(id+"F0.wireOp",EDGE,"E12.7.34.0"),sQuery(id+"F0.wireOp",EDGE,"E12.11.34.0"),sQuery(id+"F0.wireOp",EDGE,"E12.15.34.0"),sQuery(id+"F0.wireOp",EDGE,"E12.18.34.0"),sQuery(id+"F0.wireOp",EDGE,"E12.21.34.0"),sQuery(id+"F0.wireOp",EDGE,"E12.25.34.0"),sQuery(id+"F0.wireOp",EDGE,"E12.29.34.0"),sQuery(id+"F0.wireOp",EDGE,"E12.32.34.0"),sQuery(id+"F0.wireOp",EDGE,"E12.2.35.0"),sQuery(id+"F0.wireOp",EDGE,"E12.4.35.0"),sQuery(id+"F0.wireOp",EDGE,"E12.7.35.0"),sQuery(id+"F0.wireOp",EDGE,"E12.11.35.0"),sQuery(id+"F0.wireOp",EDGE,"E12.15.35.0"),sQuery(id+"F0.wireOp",EDGE,"E12.18.35.0"),sQuery(id+"F0.wireOp",EDGE,"E12.21.35.0"),sQuery(id+"F0.wireOp",EDGE,"E12.25.35.0"),sQuery(id+"F0.wireOp",EDGE,"E12.29.35.0"),sQuery(id+"F0.wireOp",EDGE,"E12.32.35.0"),sQuery(id+"F0.wireOp",EDGE,"E13.trimOffspring"),sQuery(id+"F0.wireOp",EDGE,"E14.trimOffspring"),sQuery(id+"F0.wireOp",EDGE,"E15.trimOffspring"),sQuery(id+"F0.wireOp",EDGE,"E16.trimOffspring"),sQuery(id+"F0.wireOp",EDGE,"E17.trimOffspring"),sQuery(id+"F0.wireOp",EDGE,"E18.trimOffspring"),sQuery(id+"F0.wireOp",EDGE,"E19.trimOffspring"),sQuery(id+"F0.wireOp",EDGE,"E20.trimOffspring"),sQuery(id+"F0.wireOp",EDGE,"E21.trimOffspring"),sQuery(id+"F0.wireOp",EDGE,"E22.trimOffspring"),sQuery(id+"F0.wireOp",EDGE,"E23.trimOffspring"),sQuery(id+"F0.wireOp",EDGE,"E24.trimOffspring"),sQuery(id+"F0.wireOp",EDGE,"E25.trimOffspring"),sQuery(id+"F0.wireOp",EDGE,"E26.trimOffspring"),sQuery(id+"F0.wireOp",EDGE,"E27.trimOffspring"),sQuery(id+"F0.wireOp",EDGE,"E28.trimOffspring"),sQuery(id+"F0.wireOp",EDGE,"E29.trimOffspring"),sQuery(id+"F0.wireOp",EDGE,"E30.trimOffspring"),sQuery(id+"F0.wireOp",EDGE,"E31.trimOffspring"),sQuery(id+"F0.wireOp",EDGE,"E32.trimOffspring"),sQuery(id+"F0.wireOp",EDGE,"E33.trimOffspring"),sQuery(id+"F0.wireOp",EDGE,"E34.trimOffspring"),sQuery(id+"F0.wireOp",EDGE,"E35.trimOffspring"),sQuery(id+"F0.wireOp",EDGE,"E36.trimOffspring"),sQuery(id+"F0.wireOp",EDGE,"E37.trimOffspring"),sQuery(id+"F0.wireOp",EDGE,"E38.trimOffspring"),sQuery(id+"F0.wireOp",EDGE,"E39.trimOffspring"),sQuery(id+"F0.wireOp",EDGE,"E40.trimOffspring"),sQuery(id+"F0.wireOp",EDGE,"E41.trimOffspring"),sQuery(id+"F0.wireOp",EDGE,"E42.trimOffspring"),sQuery(id+"F0.wireOp",EDGE,"E43.trimOffspring"),sQuery(id+"F0.wireOp",EDGE,"E44.trimOffspring"),sQuery(id+"F0.wireOp",EDGE,"E45.trimOffspring"),sQuery(id+"F0.wireOp",EDGE,"E46.trimOffspring"),sQuery(id+"F0.wireOp",EDGE,"E47.trimOffspring")])],"isStart":true}),makeQuery(id+"F7.hole-3.opRevolve","SWEPT_FACE",FACE,{"disambiguationData":[OSD([sQuery(id+"F7.hole-3.sketch.wireOp",EDGE,"core_line_2")])]})]});
            var Q27;
            Q27=makeQuery(id+"F7.hole-4.boolean.opBoolean","COPY",EDGE,{"derivedFrom":makeQuery(id+"F7.hole-4.opRevolve","SWEPT_EDGE",EDGE,{"disambiguationData":[OSD([sQuery(id+"F7.hole-4.sketch.wireOp",EDGE,"cbore_start_line_2"),sQuery(id+"F7.hole-4.sketch.wireOp",EDGE,"cbore_start_line_3")])]})});
            var Q28;
            Q28=makeQuery(id+"F7.hole-4.boolean.opBoolean","INTERSECT",EDGE,{"derivedFrom":[makeQuery(id+"F1.opExtrude","CAP_FACE",FACE,{"disambiguationData":[OSD([sQuery(id+"F0.wireOp",EDGE,"E0"),sQuery(id+"F0.wireOp",EDGE,"E1.trimOffspring"),sQuery(id+"F0.wireOp",EDGE,"E2"),sQuery(id+"F0.wireOp",EDGE,"E3"),sQuery(id+"F0.wireOp",EDGE,"E4.MirrorCS"),sQuery(id+"F0.wireOp",EDGE,"E5.MirrorCS"),sQuery(id+"F0.wireOp",EDGE,"E6.MirrorCS"),sQuery(id+"F0.wireOp",EDGE,"E7.filletArc"),sQuery(id+"F0.wireOp",EDGE,"E8.filletArc"),sQuery(id+"F0.wireOp",EDGE,"E9.filletArc"),sQuery(id+"F0.wireOp",EDGE,"E10.filletArc"),sQuery(id+"F0.wireOp",EDGE,"E11.1.0"),sQuery(id+"F0.wireOp",EDGE,"E11.1.1"),sQuery(id+"F0.wireOp",EDGE,"E11.1.2"),sQuery(id+"F0.wireOp",EDGE,"E11.1.3"),sQuery(id+"F0.wireOp",EDGE,"E11.1.4"),sQuery(id+"F0.wireOp",EDGE,"E11.1.5"),sQuery(id+"F0.wireOp",EDGE,"E11.1.6"),sQuery(id+"F0.wireOp",EDGE,"E11.1.7"),sQuery(id+"F0.wireOp",EDGE,"E11.1.8"),sQuery(id+"F0.wireOp",EDGE,"E11.1.9"),sQuery(id+"F0.wireOp",EDGE,"E11.2.0"),sQuery(id+"F0.wireOp",EDGE,"E11.2.1"),sQuery(id+"F0.wireOp",EDGE,"E11.2.2"),sQuery(id+"F0.wireOp",EDGE,"E11.2.3"),sQuery(id+"F0.wireOp",EDGE,"E11.2.4"),sQuery(id+"F0.wireOp",EDGE,"E11.2.5"),sQuery(id+"F0.wireOp",EDGE,"E11.2.6"),sQuery(id+"F0.wireOp",EDGE,"E11.2.7"),sQuery(id+"F0.wireOp",EDGE,"E11.2.8"),sQuery(id+"F0.wireOp",EDGE,"E11.2.9"),sQuery(id+"F0.wireOp",EDGE,"E12.2.3.0"),sQuery(id+"F0.wireOp",EDGE,"E12.4.3.0"),sQuery(id+"F0.wireOp",EDGE,"E12.7.3.0"),sQuery(id+"F0.wireOp",EDGE,"E12.11.3.0"),sQuery(id+"F0.wireOp",EDGE,"E12.15.3.0"),sQuery(id+"F0.wireOp",EDGE,"E12.18.3.0"),sQuery(id+"F0.wireOp",EDGE,"E12.21.3.0"),sQuery(id+"F0.wireOp",EDGE,"E12.25.3.0"),sQuery(id+"F0.wireOp",EDGE,"E12.29.3.0"),sQuery(id+"F0.wireOp",EDGE,"E12.32.3.0"),sQuery(id+"F0.wireOp",EDGE,"E12.2.4.0"),sQuery(id+"F0.wireOp",EDGE,"E12.4.4.0"),sQuery(id+"F0.wireOp",EDGE,"E12.7.4.0"),sQuery(id+"F0.wireOp",EDGE,"E12.11.4.0"),sQuery(id+"F0.wireOp",EDGE,"E12.15.4.0"),sQuery(id+"F0.wireOp",EDGE,"E12.18.4.0"),sQuery(id+"F0.wireOp",EDGE,"E12.21.4.0"),sQuery(id+"F0.wireOp",EDGE,"E12.25.4.0"),sQuery(id+"F0.wireOp",EDGE,"E12.29.4.0"),sQuery(id+"F0.wireOp",EDGE,"E12.32.4.0"),sQuery(id+"F0.wireOp",EDGE,"E12.2.5.0"),sQuery(id+"F0.wireOp",EDGE,"E12.4.5.0"),sQuery(id+"F0.wireOp",EDGE,"E12.7.5.0"),sQuery(id+"F0.wireOp",EDGE,"E12.11.5.0"),sQuery(id+"F0.wireOp",EDGE,"E12.15.5.0"),sQuery(id+"F0.wireOp",EDGE,"E12.18.5.0"),sQuery(id+"F0.wireOp",EDGE,"E12.21.5.0"),sQuery(id+"F0.wireOp",EDGE,"E12.25.5.0"),sQuery(id+"F0.wireOp",EDGE,"E12.29.5.0"),sQuery(id+"F0.wireOp",EDGE,"E12.32.5.0"),sQuery(id+"F0.wireOp",EDGE,"E12.2.6.0"),sQuery(id+"F0.wireOp",EDGE,"E12.4.6.0"),sQuery(id+"F0.wireOp",EDGE,"E12.7.6.0"),sQuery(id+"F0.wireOp",EDGE,"E12.11.6.0"),sQuery(id+"F0.wireOp",EDGE,"E12.15.6.0"),sQuery(id+"F0.wireOp",EDGE,"E12.18.6.0"),sQuery(id+"F0.wireOp",EDGE,"E12.21.6.0"),sQuery(id+"F0.wireOp",EDGE,"E12.25.6.0"),sQuery(id+"F0.wireOp",EDGE,"E12.29.6.0"),sQuery(id+"F0.wireOp",EDGE,"E12.32.6.0"),sQuery(id+"F0.wireOp",EDGE,"E12.2.7.0"),sQuery(id+"F0.wireOp",EDGE,"E12.4.7.0"),sQuery(id+"F0.wireOp",EDGE,"E12.7.7.0"),sQuery(id+"F0.wireOp",EDGE,"E12.11.7.0"),sQuery(id+"F0.wireOp",EDGE,"E12.15.7.0"),sQuery(id+"F0.wireOp",EDGE,"E12.18.7.0"),sQuery(id+"F0.wireOp",EDGE,"E12.21.7.0"),sQuery(id+"F0.wireOp",EDGE,"E12.25.7.0"),sQuery(id+"F0.wireOp",EDGE,"E12.29.7.0"),sQuery(id+"F0.wireOp",EDGE,"E12.32.7.0"),sQuery(id+"F0.wireOp",EDGE,"E12.2.8.0"),sQuery(id+"F0.wireOp",EDGE,"E12.4.8.0"),sQuery(id+"F0.wireOp",EDGE,"E12.7.8.0"),sQuery(id+"F0.wireOp",EDGE,"E12.11.8.0"),sQuery(id+"F0.wireOp",EDGE,"E12.15.8.0"),sQuery(id+"F0.wireOp",EDGE,"E12.18.8.0"),sQuery(id+"F0.wireOp",EDGE,"E12.21.8.0"),sQuery(id+"F0.wireOp",EDGE,"E12.25.8.0"),sQuery(id+"F0.wireOp",EDGE,"E12.29.8.0"),sQuery(id+"F0.wireOp",EDGE,"E12.32.8.0"),sQuery(id+"F0.wireOp",EDGE,"E12.2.9.0"),sQuery(id+"F0.wireOp",EDGE,"E12.4.9.0"),sQuery(id+"F0.wireOp",EDGE,"E12.7.9.0"),sQuery(id+"F0.wireOp",EDGE,"E12.11.9.0"),sQuery(id+"F0.wireOp",EDGE,"E12.15.9.0"),sQuery(id+"F0.wireOp",EDGE,"E12.18.9.0"),sQuery(id+"F0.wireOp",EDGE,"E12.21.9.0"),sQuery(id+"F0.wireOp",EDGE,"E12.25.9.0"),sQuery(id+"F0.wireOp",EDGE,"E12.29.9.0"),sQuery(id+"F0.wireOp",EDGE,"E12.32.9.0"),sQuery(id+"F0.wireOp",EDGE,"E12.2.10.0"),sQuery(id+"F0.wireOp",EDGE,"E12.4.10.0"),sQuery(id+"F0.wireOp",EDGE,"E12.7.10.0"),sQuery(id+"F0.wireOp",EDGE,"E12.11.10.0"),sQuery(id+"F0.wireOp",EDGE,"E12.15.10.0"),sQuery(id+"F0.wireOp",EDGE,"E12.18.10.0"),sQuery(id+"F0.wireOp",EDGE,"E12.21.10.0"),sQuery(id+"F0.wireOp",EDGE,"E12.25.10.0"),sQuery(id+"F0.wireOp",EDGE,"E12.29.10.0"),sQuery(id+"F0.wireOp",EDGE,"E12.32.10.0"),sQuery(id+"F0.wireOp",EDGE,"E12.2.11.0"),sQuery(id+"F0.wireOp",EDGE,"E12.4.11.0"),sQuery(id+"F0.wireOp",EDGE,"E12.7.11.0"),sQuery(id+"F0.wireOp",EDGE,"E12.11.11.0"),sQuery(id+"F0.wireOp",EDGE,"E12.15.11.0"),sQuery(id+"F0.wireOp",EDGE,"E12.18.11.0"),sQuery(id+"F0.wireOp",EDGE,"E12.21.11.0"),sQuery(id+"F0.wireOp",EDGE,"E12.25.11.0"),sQuery(id+"F0.wireOp",EDGE,"E12.29.11.0"),sQuery(id+"F0.wireOp",EDGE,"E12.32.11.0"),sQuery(id+"F0.wireOp",EDGE,"E12.2.12.0"),sQuery(id+"F0.wireOp",EDGE,"E12.4.12.0"),sQuery(id+"F0.wireOp",EDGE,"E12.7.12.0"),sQuery(id+"F0.wireOp",EDGE,"E12.11.12.0"),sQuery(id+"F0.wireOp",EDGE,"E12.15.12.0"),sQuery(id+"F0.wireOp",EDGE,"E12.18.12.0"),sQuery(id+"F0.wireOp",EDGE,"E12.21.12.0"),sQuery(id+"F0.wireOp",EDGE,"E12.25.12.0"),sQuery(id+"F0.wireOp",EDGE,"E12.29.12.0"),sQuery(id+"F0.wireOp",EDGE,"E12.32.12.0"),sQuery(id+"F0.wireOp",EDGE,"E12.2.13.0"),sQuery(id+"F0.wireOp",EDGE,"E12.4.13.0"),sQuery(id+"F0.wireOp",EDGE,"E12.7.13.0"),sQuery(id+"F0.wireOp",EDGE,"E12.11.13.0"),sQuery(id+"F0.wireOp",EDGE,"E12.15.13.0"),sQuery(id+"F0.wireOp",EDGE,"E12.18.13.0"),sQuery(id+"F0.wireOp",EDGE,"E12.21.13.0"),sQuery(id+"F0.wireOp",EDGE,"E12.25.13.0"),sQuery(id+"F0.wireOp",EDGE,"E12.29.13.0"),sQuery(id+"F0.wireOp",EDGE,"E12.32.13.0"),sQuery(id+"F0.wireOp",EDGE,"E12.2.14.0"),sQuery(id+"F0.wireOp",EDGE,"E12.4.14.0"),sQuery(id+"F0.wireOp",EDGE,"E12.7.14.0"),sQuery(id+"F0.wireOp",EDGE,"E12.11.14.0"),sQuery(id+"F0.wireOp",EDGE,"E12.15.14.0"),sQuery(id+"F0.wireOp",EDGE,"E12.18.14.0"),sQuery(id+"F0.wireOp",EDGE,"E12.21.14.0"),sQuery(id+"F0.wireOp",EDGE,"E12.25.14.0"),sQuery(id+"F0.wireOp",EDGE,"E12.29.14.0"),sQuery(id+"F0.wireOp",EDGE,"E12.32.14.0"),sQuery(id+"F0.wireOp",EDGE,"E12.2.15.0"),sQuery(id+"F0.wireOp",EDGE,"E12.4.15.0"),sQuery(id+"F0.wireOp",EDGE,"E12.7.15.0"),sQuery(id+"F0.wireOp",EDGE,"E12.11.15.0"),sQuery(id+"F0.wireOp",EDGE,"E12.15.15.0"),sQuery(id+"F0.wireOp",EDGE,"E12.18.15.0"),sQuery(id+"F0.wireOp",EDGE,"E12.21.15.0"),sQuery(id+"F0.wireOp",EDGE,"E12.25.15.0"),sQuery(id+"F0.wireOp",EDGE,"E12.29.15.0"),sQuery(id+"F0.wireOp",EDGE,"E12.32.15.0"),sQuery(id+"F0.wireOp",EDGE,"E12.2.16.0"),sQuery(id+"F0.wireOp",EDGE,"E12.4.16.0"),sQuery(id+"F0.wireOp",EDGE,"E12.7.16.0"),sQuery(id+"F0.wireOp",EDGE,"E12.11.16.0"),sQuery(id+"F0.wireOp",EDGE,"E12.15.16.0"),sQuery(id+"F0.wireOp",EDGE,"E12.18.16.0"),sQuery(id+"F0.wireOp",EDGE,"E12.21.16.0"),sQuery(id+"F0.wireOp",EDGE,"E12.25.16.0"),sQuery(id+"F0.wireOp",EDGE,"E12.29.16.0"),sQuery(id+"F0.wireOp",EDGE,"E12.32.16.0"),sQuery(id+"F0.wireOp",EDGE,"E12.2.17.0"),sQuery(id+"F0.wireOp",EDGE,"E12.4.17.0"),sQuery(id+"F0.wireOp",EDGE,"E12.7.17.0"),sQuery(id+"F0.wireOp",EDGE,"E12.11.17.0"),sQuery(id+"F0.wireOp",EDGE,"E12.15.17.0"),sQuery(id+"F0.wireOp",EDGE,"E12.18.17.0"),sQuery(id+"F0.wireOp",EDGE,"E12.21.17.0"),sQuery(id+"F0.wireOp",EDGE,"E12.25.17.0"),sQuery(id+"F0.wireOp",EDGE,"E12.29.17.0"),sQuery(id+"F0.wireOp",EDGE,"E12.32.17.0"),sQuery(id+"F0.wireOp",EDGE,"E12.2.18.0"),sQuery(id+"F0.wireOp",EDGE,"E12.4.18.0"),sQuery(id+"F0.wireOp",EDGE,"E12.7.18.0"),sQuery(id+"F0.wireOp",EDGE,"E12.11.18.0"),sQuery(id+"F0.wireOp",EDGE,"E12.15.18.0"),sQuery(id+"F0.wireOp",EDGE,"E12.18.18.0"),sQuery(id+"F0.wireOp",EDGE,"E12.21.18.0"),sQuery(id+"F0.wireOp",EDGE,"E12.25.18.0"),sQuery(id+"F0.wireOp",EDGE,"E12.29.18.0"),sQuery(id+"F0.wireOp",EDGE,"E12.32.18.0"),sQuery(id+"F0.wireOp",EDGE,"E12.2.19.0"),sQuery(id+"F0.wireOp",EDGE,"E12.4.19.0"),sQuery(id+"F0.wireOp",EDGE,"E12.7.19.0"),sQuery(id+"F0.wireOp",EDGE,"E12.11.19.0"),sQuery(id+"F0.wireOp",EDGE,"E12.15.19.0"),sQuery(id+"F0.wireOp",EDGE,"E12.18.19.0"),sQuery(id+"F0.wireOp",EDGE,"E12.21.19.0"),sQuery(id+"F0.wireOp",EDGE,"E12.25.19.0"),sQuery(id+"F0.wireOp",EDGE,"E12.29.19.0"),sQuery(id+"F0.wireOp",EDGE,"E12.32.19.0"),sQuery(id+"F0.wireOp",EDGE,"E12.2.20.0"),sQuery(id+"F0.wireOp",EDGE,"E12.4.20.0"),sQuery(id+"F0.wireOp",EDGE,"E12.7.20.0"),sQuery(id+"F0.wireOp",EDGE,"E12.11.20.0"),sQuery(id+"F0.wireOp",EDGE,"E12.15.20.0"),sQuery(id+"F0.wireOp",EDGE,"E12.18.20.0"),sQuery(id+"F0.wireOp",EDGE,"E12.21.20.0"),sQuery(id+"F0.wireOp",EDGE,"E12.25.20.0"),sQuery(id+"F0.wireOp",EDGE,"E12.29.20.0"),sQuery(id+"F0.wireOp",EDGE,"E12.32.20.0"),sQuery(id+"F0.wireOp",EDGE,"E12.2.21.0"),sQuery(id+"F0.wireOp",EDGE,"E12.4.21.0"),sQuery(id+"F0.wireOp",EDGE,"E12.7.21.0"),sQuery(id+"F0.wireOp",EDGE,"E12.11.21.0"),sQuery(id+"F0.wireOp",EDGE,"E12.15.21.0"),sQuery(id+"F0.wireOp",EDGE,"E12.18.21.0"),sQuery(id+"F0.wireOp",EDGE,"E12.21.21.0"),sQuery(id+"F0.wireOp",EDGE,"E12.25.21.0"),sQuery(id+"F0.wireOp",EDGE,"E12.29.21.0"),sQuery(id+"F0.wireOp",EDGE,"E12.32.21.0"),sQuery(id+"F0.wireOp",EDGE,"E12.2.22.0"),sQuery(id+"F0.wireOp",EDGE,"E12.4.22.0"),sQuery(id+"F0.wireOp",EDGE,"E12.7.22.0"),sQuery(id+"F0.wireOp",EDGE,"E12.11.22.0"),sQuery(id+"F0.wireOp",EDGE,"E12.15.22.0"),sQuery(id+"F0.wireOp",EDGE,"E12.18.22.0"),sQuery(id+"F0.wireOp",EDGE,"E12.21.22.0"),sQuery(id+"F0.wireOp",EDGE,"E12.25.22.0"),sQuery(id+"F0.wireOp",EDGE,"E12.29.22.0"),sQuery(id+"F0.wireOp",EDGE,"E12.32.22.0"),sQuery(id+"F0.wireOp",EDGE,"E12.2.23.0"),sQuery(id+"F0.wireOp",EDGE,"E12.4.23.0"),sQuery(id+"F0.wireOp",EDGE,"E12.7.23.0"),sQuery(id+"F0.wireOp",EDGE,"E12.11.23.0"),sQuery(id+"F0.wireOp",EDGE,"E12.15.23.0"),sQuery(id+"F0.wireOp",EDGE,"E12.18.23.0"),sQuery(id+"F0.wireOp",EDGE,"E12.21.23.0"),sQuery(id+"F0.wireOp",EDGE,"E12.25.23.0"),sQuery(id+"F0.wireOp",EDGE,"E12.29.23.0"),sQuery(id+"F0.wireOp",EDGE,"E12.32.23.0"),sQuery(id+"F0.wireOp",EDGE,"E12.2.24.0"),sQuery(id+"F0.wireOp",EDGE,"E12.4.24.0"),sQuery(id+"F0.wireOp",EDGE,"E12.7.24.0"),sQuery(id+"F0.wireOp",EDGE,"E12.11.24.0"),sQuery(id+"F0.wireOp",EDGE,"E12.15.24.0"),sQuery(id+"F0.wireOp",EDGE,"E12.18.24.0"),sQuery(id+"F0.wireOp",EDGE,"E12.21.24.0"),sQuery(id+"F0.wireOp",EDGE,"E12.25.24.0"),sQuery(id+"F0.wireOp",EDGE,"E12.29.24.0"),sQuery(id+"F0.wireOp",EDGE,"E12.32.24.0"),sQuery(id+"F0.wireOp",EDGE,"E12.2.25.0"),sQuery(id+"F0.wireOp",EDGE,"E12.4.25.0"),sQuery(id+"F0.wireOp",EDGE,"E12.7.25.0"),sQuery(id+"F0.wireOp",EDGE,"E12.11.25.0"),sQuery(id+"F0.wireOp",EDGE,"E12.15.25.0"),sQuery(id+"F0.wireOp",EDGE,"E12.18.25.0"),sQuery(id+"F0.wireOp",EDGE,"E12.21.25.0"),sQuery(id+"F0.wireOp",EDGE,"E12.25.25.0"),sQuery(id+"F0.wireOp",EDGE,"E12.29.25.0"),sQuery(id+"F0.wireOp",EDGE,"E12.32.25.0"),sQuery(id+"F0.wireOp",EDGE,"E12.2.26.0"),sQuery(id+"F0.wireOp",EDGE,"E12.4.26.0"),sQuery(id+"F0.wireOp",EDGE,"E12.7.26.0"),sQuery(id+"F0.wireOp",EDGE,"E12.11.26.0"),sQuery(id+"F0.wireOp",EDGE,"E12.15.26.0"),sQuery(id+"F0.wireOp",EDGE,"E12.18.26.0"),sQuery(id+"F0.wireOp",EDGE,"E12.21.26.0"),sQuery(id+"F0.wireOp",EDGE,"E12.25.26.0"),sQuery(id+"F0.wireOp",EDGE,"E12.29.26.0"),sQuery(id+"F0.wireOp",EDGE,"E12.32.26.0"),sQuery(id+"F0.wireOp",EDGE,"E12.2.27.0"),sQuery(id+"F0.wireOp",EDGE,"E12.4.27.0"),sQuery(id+"F0.wireOp",EDGE,"E12.7.27.0"),sQuery(id+"F0.wireOp",EDGE,"E12.11.27.0"),sQuery(id+"F0.wireOp",EDGE,"E12.15.27.0"),sQuery(id+"F0.wireOp",EDGE,"E12.18.27.0"),sQuery(id+"F0.wireOp",EDGE,"E12.21.27.0"),sQuery(id+"F0.wireOp",EDGE,"E12.25.27.0"),sQuery(id+"F0.wireOp",EDGE,"E12.29.27.0"),sQuery(id+"F0.wireOp",EDGE,"E12.32.27.0"),sQuery(id+"F0.wireOp",EDGE,"E12.2.28.0"),sQuery(id+"F0.wireOp",EDGE,"E12.4.28.0"),sQuery(id+"F0.wireOp",EDGE,"E12.7.28.0"),sQuery(id+"F0.wireOp",EDGE,"E12.11.28.0"),sQuery(id+"F0.wireOp",EDGE,"E12.15.28.0"),sQuery(id+"F0.wireOp",EDGE,"E12.18.28.0"),sQuery(id+"F0.wireOp",EDGE,"E12.21.28.0"),sQuery(id+"F0.wireOp",EDGE,"E12.25.28.0"),sQuery(id+"F0.wireOp",EDGE,"E12.29.28.0"),sQuery(id+"F0.wireOp",EDGE,"E12.32.28.0"),sQuery(id+"F0.wireOp",EDGE,"E12.2.29.0"),sQuery(id+"F0.wireOp",EDGE,"E12.4.29.0"),sQuery(id+"F0.wireOp",EDGE,"E12.7.29.0"),sQuery(id+"F0.wireOp",EDGE,"E12.11.29.0"),sQuery(id+"F0.wireOp",EDGE,"E12.15.29.0"),sQuery(id+"F0.wireOp",EDGE,"E12.18.29.0"),sQuery(id+"F0.wireOp",EDGE,"E12.21.29.0"),sQuery(id+"F0.wireOp",EDGE,"E12.25.29.0"),sQuery(id+"F0.wireOp",EDGE,"E12.29.29.0"),sQuery(id+"F0.wireOp",EDGE,"E12.32.29.0"),sQuery(id+"F0.wireOp",EDGE,"E12.2.30.0"),sQuery(id+"F0.wireOp",EDGE,"E12.4.30.0"),sQuery(id+"F0.wireOp",EDGE,"E12.7.30.0"),sQuery(id+"F0.wireOp",EDGE,"E12.11.30.0"),sQuery(id+"F0.wireOp",EDGE,"E12.15.30.0"),sQuery(id+"F0.wireOp",EDGE,"E12.18.30.0"),sQuery(id+"F0.wireOp",EDGE,"E12.21.30.0"),sQuery(id+"F0.wireOp",EDGE,"E12.25.30.0"),sQuery(id+"F0.wireOp",EDGE,"E12.29.30.0"),sQuery(id+"F0.wireOp",EDGE,"E12.32.30.0"),sQuery(id+"F0.wireOp",EDGE,"E12.2.31.0"),sQuery(id+"F0.wireOp",EDGE,"E12.4.31.0"),sQuery(id+"F0.wireOp",EDGE,"E12.7.31.0"),sQuery(id+"F0.wireOp",EDGE,"E12.11.31.0"),sQuery(id+"F0.wireOp",EDGE,"E12.15.31.0"),sQuery(id+"F0.wireOp",EDGE,"E12.18.31.0"),sQuery(id+"F0.wireOp",EDGE,"E12.21.31.0"),sQuery(id+"F0.wireOp",EDGE,"E12.25.31.0"),sQuery(id+"F0.wireOp",EDGE,"E12.29.31.0"),sQuery(id+"F0.wireOp",EDGE,"E12.32.31.0"),sQuery(id+"F0.wireOp",EDGE,"E12.2.32.0"),sQuery(id+"F0.wireOp",EDGE,"E12.4.32.0"),sQuery(id+"F0.wireOp",EDGE,"E12.7.32.0"),sQuery(id+"F0.wireOp",EDGE,"E12.11.32.0"),sQuery(id+"F0.wireOp",EDGE,"E12.15.32.0"),sQuery(id+"F0.wireOp",EDGE,"E12.18.32.0"),sQuery(id+"F0.wireOp",EDGE,"E12.21.32.0"),sQuery(id+"F0.wireOp",EDGE,"E12.25.32.0"),sQuery(id+"F0.wireOp",EDGE,"E12.29.32.0"),sQuery(id+"F0.wireOp",EDGE,"E12.32.32.0"),sQuery(id+"F0.wireOp",EDGE,"E12.2.33.0"),sQuery(id+"F0.wireOp",EDGE,"E12.4.33.0"),sQuery(id+"F0.wireOp",EDGE,"E12.7.33.0"),sQuery(id+"F0.wireOp",EDGE,"E12.11.33.0"),sQuery(id+"F0.wireOp",EDGE,"E12.15.33.0"),sQuery(id+"F0.wireOp",EDGE,"E12.18.33.0"),sQuery(id+"F0.wireOp",EDGE,"E12.21.33.0"),sQuery(id+"F0.wireOp",EDGE,"E12.25.33.0"),sQuery(id+"F0.wireOp",EDGE,"E12.29.33.0"),sQuery(id+"F0.wireOp",EDGE,"E12.32.33.0"),sQuery(id+"F0.wireOp",EDGE,"E12.2.34.0"),sQuery(id+"F0.wireOp",EDGE,"E12.4.34.0"),sQuery(id+"F0.wireOp",EDGE,"E12.7.34.0"),sQuery(id+"F0.wireOp",EDGE,"E12.11.34.0"),sQuery(id+"F0.wireOp",EDGE,"E12.15.34.0"),sQuery(id+"F0.wireOp",EDGE,"E12.18.34.0"),sQuery(id+"F0.wireOp",EDGE,"E12.21.34.0"),sQuery(id+"F0.wireOp",EDGE,"E12.25.34.0"),sQuery(id+"F0.wireOp",EDGE,"E12.29.34.0"),sQuery(id+"F0.wireOp",EDGE,"E12.32.34.0"),sQuery(id+"F0.wireOp",EDGE,"E12.2.35.0"),sQuery(id+"F0.wireOp",EDGE,"E12.4.35.0"),sQuery(id+"F0.wireOp",EDGE,"E12.7.35.0"),sQuery(id+"F0.wireOp",EDGE,"E12.11.35.0"),sQuery(id+"F0.wireOp",EDGE,"E12.15.35.0"),sQuery(id+"F0.wireOp",EDGE,"E12.18.35.0"),sQuery(id+"F0.wireOp",EDGE,"E12.21.35.0"),sQuery(id+"F0.wireOp",EDGE,"E12.25.35.0"),sQuery(id+"F0.wireOp",EDGE,"E12.29.35.0"),sQuery(id+"F0.wireOp",EDGE,"E12.32.35.0"),sQuery(id+"F0.wireOp",EDGE,"E13.trimOffspring"),sQuery(id+"F0.wireOp",EDGE,"E14.trimOffspring"),sQuery(id+"F0.wireOp",EDGE,"E15.trimOffspring"),sQuery(id+"F0.wireOp",EDGE,"E16.trimOffspring"),sQuery(id+"F0.wireOp",EDGE,"E17.trimOffspring"),sQuery(id+"F0.wireOp",EDGE,"E18.trimOffspring"),sQuery(id+"F0.wireOp",EDGE,"E19.trimOffspring"),sQuery(id+"F0.wireOp",EDGE,"E20.trimOffspring"),sQuery(id+"F0.wireOp",EDGE,"E21.trimOffspring"),sQuery(id+"F0.wireOp",EDGE,"E22.trimOffspring"),sQuery(id+"F0.wireOp",EDGE,"E23.trimOffspring"),sQuery(id+"F0.wireOp",EDGE,"E24.trimOffspring"),sQuery(id+"F0.wireOp",EDGE,"E25.trimOffspring"),sQuery(id+"F0.wireOp",EDGE,"E26.trimOffspring"),sQuery(id+"F0.wireOp",EDGE,"E27.trimOffspring"),sQuery(id+"F0.wireOp",EDGE,"E28.trimOffspring"),sQuery(id+"F0.wireOp",EDGE,"E29.trimOffspring"),sQuery(id+"F0.wireOp",EDGE,"E30.trimOffspring"),sQuery(id+"F0.wireOp",EDGE,"E31.trimOffspring"),sQuery(id+"F0.wireOp",EDGE,"E32.trimOffspring"),sQuery(id+"F0.wireOp",EDGE,"E33.trimOffspring"),sQuery(id+"F0.wireOp",EDGE,"E34.trimOffspring"),sQuery(id+"F0.wireOp",EDGE,"E35.trimOffspring"),sQuery(id+"F0.wireOp",EDGE,"E36.trimOffspring"),sQuery(id+"F0.wireOp",EDGE,"E37.trimOffspring"),sQuery(id+"F0.wireOp",EDGE,"E38.trimOffspring"),sQuery(id+"F0.wireOp",EDGE,"E39.trimOffspring"),sQuery(id+"F0.wireOp",EDGE,"E40.trimOffspring"),sQuery(id+"F0.wireOp",EDGE,"E41.trimOffspring"),sQuery(id+"F0.wireOp",EDGE,"E42.trimOffspring"),sQuery(id+"F0.wireOp",EDGE,"E43.trimOffspring"),sQuery(id+"F0.wireOp",EDGE,"E44.trimOffspring"),sQuery(id+"F0.wireOp",EDGE,"E45.trimOffspring"),sQuery(id+"F0.wireOp",EDGE,"E46.trimOffspring"),sQuery(id+"F0.wireOp",EDGE,"E47.trimOffspring")])],"isStart":true}),makeQuery(id+"F7.hole-4.opRevolve","SWEPT_FACE",FACE,{"disambiguationData":[OSD([sQuery(id+"F7.hole-4.sketch.wireOp",EDGE,"core_line_2")])]})]});
            chamfer(context, id + "F10", {"entities" : qUnion([Q0, Q1, Q2, Q3, Q4, Q5, Q6, Q7, Q8, Q9, Q10, Q11, Q12, Q13, Q14, Q15, Q16, Q17, Q18, Q19, Q20, Q21, Q22, Q23, Q24, Q25, Q26, Q27, Q28]), "chamferType" : ChamferType.OFFSET_ANGLE, "width" : 0.38 * mm, "oppositeDirection" : false, "angle" : 45 * degree, "tangentPropagation" : true});
        }
    });
